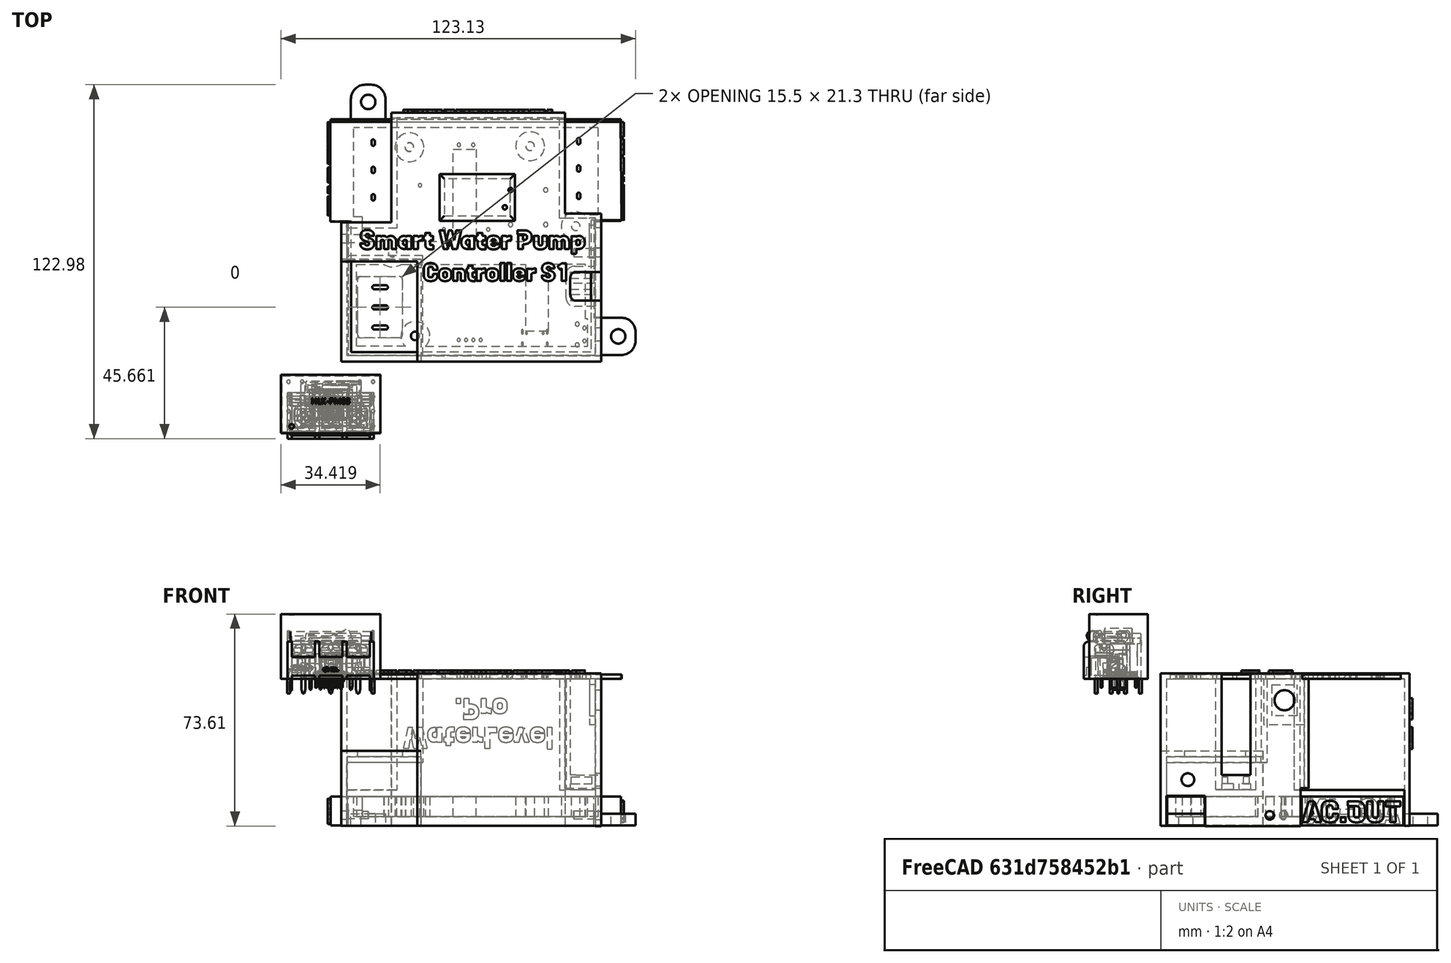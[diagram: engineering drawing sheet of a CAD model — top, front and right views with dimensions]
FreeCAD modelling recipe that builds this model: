
FCSTD DOCUMENT  (FreeCAD 0.21R33771 (Git))
Label: PumpControllerS1_case
License: GPLv3
LicenseURL: https://en.wikipedia.org/wiki/All_rights_reserved
objects: Part::Feature×416, App::Part×69, PartDesign::Pad×68, Sketcher::SketchObject×49, PartDesign::Pocket×38, Part::Part2DObjectPython×8, PartDesign::Fillet×5, PartDesign::Body×3, PartDesign::Boolean×1, PartDesign::Chamfer×1
note: 701 computed .brp shape members not serialized (recipe doc carries the construction recipe); baked Part::Feature solids carry a one-line shape summary decoded from their .brp

FEATURE [Sketcher::SketchObject] Sketch
  FullyConstrained = true
  MapMode = 5
  Support = -> [XY_Plane049]
  sketch-geometry (8):
    g0: LineSegment StartX=0 StartY=63.64 StartZ=0 EndX=0 EndY=97.92 EndZ=0
    g1: LineSegment StartX=0 StartY=97.92 StartZ=0 EndX=100.82 EndY=97.92 EndZ=0
    g2: LineSegment StartX=100.82 StartY=97.92 StartZ=0 EndX=100.82 EndY=63.64 EndZ=0
    g3: LineSegment StartX=100.82 StartY=63.64 StartZ=0 EndX=90.46 EndY=63.64 EndZ=0
    g4: LineSegment StartX=90.46 StartY=63.64 StartZ=0 EndX=90.46 EndY=17.97 EndZ=0
    g5: LineSegment StartX=90.46 StartY=17.97 StartZ=0 EndX=6.99 EndY=17.97 EndZ=0
    g6: LineSegment StartX=6.99 StartY=17.97 StartZ=0 EndX=6.99 EndY=63.64 EndZ=0
    g7: LineSegment StartX=6.99 StartY=63.64 StartZ=0 EndX=0 EndY=63.64 EndZ=0
  constraints (24):
    c: PointOnObject(g0,g-2)
    c: Coincident(g0,g1)
    c: Horizontal(g1)
    c: Coincident(g1,g2)
    c: Vertical(g2)
    c: Coincident(g2,g3)
    c: Horizontal(g3)
    c: Coincident(g3,g4)
    c: Vertical(g4)
    c: Coincident(g4,g5)
    c: Horizontal(g5)
    c: Coincident(g5,g6)
    c: Vertical(g6)
    c: Coincident(g6,g7)
    c: Coincident(g7,g0)
    c: Horizontal(g7)
    c: DistanceX(g0,g1) = 100.82
    c: DistanceX(g5,g4) = 83.47
    c: DistanceX(g3,g2) = 10.36
    c: DistanceY(g2,g1) = 34.28
    c: DistanceY(g4,g3) = 45.67
    c: DistanceY(g-1,g5) = 17.97
    c: Vertical(g0)
    c: Equal(g0,g2)
FEATURE [PartDesign::Pad] Pad
  Direction = (0,0,1)
  Length = 3
  Length2 = 10
  Profile = -> Sketch
  ReferenceAxis = -> Sketch [N_Axis]
  Refine = true
  Type = 0
FEATURE [Sketcher::SketchObject] Sketch001
  FullyConstrained = true
  MapMode = 5
  Placement = pos=(0,0,3) rot=(0,0,1;0rad)
  Support = -> [Pad]
  sketch-geometry (10):
    g0: Circle CenterX=29.39 CenterY=23.62 CenterZ=0 NormalX=0 NormalY=0 NormalZ=1 AngleXU=0 Radius=5
    g1: Circle CenterX=21.48 CenterY=52.55 CenterZ=0 NormalX=0 NormalY=0 NormalZ=1 AngleXU=0 Radius=5
    g2: Circle CenterX=85.08 CenterY=61.73 CenterZ=0 NormalX=0 NormalY=0 NormalZ=1 AngleXU=0 Radius=5
    g3: Circle CenterX=69.27 CenterY=89.53 CenterZ=0 NormalX=0 NormalY=0 NormalZ=1 AngleXU=0 Radius=5
    g4: Circle CenterX=27.31 CenterY=89.16 CenterZ=0 NormalX=0 NormalY=0 NormalZ=1 AngleXU=0 Radius=5
    g5: Circle CenterX=29.39 CenterY=23.62 CenterZ=0 NormalX=0 NormalY=0 NormalZ=1 AngleXU=0 Radius=1.5
    g6: Circle CenterX=21.48 CenterY=52.55 CenterZ=0 NormalX=0 NormalY=0 NormalZ=1 AngleXU=0 Radius=1.5
    g7: Circle CenterX=27.31 CenterY=89.16 CenterZ=0 NormalX=0 NormalY=0 NormalZ=1 AngleXU=0 Radius=1.5
    g8: Circle CenterX=69.27 CenterY=89.53 CenterZ=0 NormalX=0 NormalY=0 NormalZ=1 AngleXU=0 Radius=1.5
    g9: Circle CenterX=85.08 CenterY=61.73 CenterZ=0 NormalX=0 NormalY=0 NormalZ=1 AngleXU=0 Radius=1.5
  constraints (25):
    c: Diameter(g4) = 10
    c: Diameter(g1) = 10
    c: Diameter(g0) = 10
    c: Diameter(g2) = 10
    c: Diameter(g3) = 10
    c: DistanceX(g4,g3) = 41.96
    c: DistanceX(g1,g4) = 5.83
    c: DistanceX(g3,g2) = 15.81
    c: DistanceX(g1,g0) = 7.91
    c: DistanceX(g-1,g0) = 29.39
    c: DistanceY(g4,g3) = 0.37
    c: DistanceY(g2,g3) = 27.8
    c: DistanceY(g1,g4) = 36.61
    c: DistanceY(g0,g1) = 28.93
    c: DistanceY(g-1,g0) = 23.62
    c: Coincident(g5,g0)
    c: Diameter(g5) = 3
    c: Coincident(g6,g1)
    c: Coincident(g7,g4)
    c: Coincident(g8,g3)
    c: Coincident(g9,g2)
    c: Diameter(g7) = 3
    c: Diameter(g8) = 3
    c: Diameter(g9) = 3
    c: Diameter(g6) = 3
FEATURE [PartDesign::Pad] Pad001
  BaseFeature = -> Pad
  Direction = (0,0,1)
  Length = 7
  Length2 = 10
  Profile = -> Sketch001
  ReferenceAxis = -> Sketch001 [N_Axis]
  Refine = true
  Type = 0
FEATURE [Sketcher::SketchObject] Sketch002
  ExternalGeometry = -> [Pad001]
  FullyConstrained = false
  MapMode = 5
  Placement = pos=(0,0,3) rot=(0,0,1;0rad)
  Support = -> [Pad001]
  sketch-geometry (21):
    g0: LineSegment StartX=90.46 StartY=56.5 StartZ=0 EndX=90.46 EndY=48.4293 EndZ=0
    g1: LineSegment StartX=7 StartY=48.5 StartZ=0 EndX=7 EndY=56.5 EndZ=0
    g2: Circle CenterX=21.48 CenterY=52.55 CenterZ=0 NormalX=0 NormalY=0 NormalZ=1 AngleXU=0 Radius=1.5
    g3: LineSegment StartX=42.46 StartY=56.5 StartZ=0 EndX=42.46 EndY=88.5 EndZ=0
    g4: LineSegment StartX=42.46 StartY=88.5 StartZ=0 EndX=50.46 EndY=88.5 EndZ=0
    g5: LineSegment StartX=50.46 StartY=88.5 StartZ=0 EndX=50.46 EndY=56.5 EndZ=0
    g6: LineSegment StartX=67.69 StartY=48.5 StartZ=0 EndX=67.69 EndY=25.4293 EndZ=0
    g7: LineSegment StartX=67.69 StartY=25.4293 StartZ=0 EndX=75.69 EndY=25.4293 EndZ=0
    g8: LineSegment StartX=75.69 StartY=25.4293 StartZ=0 EndX=75.69 EndY=48.4293 EndZ=0
    g9: LineSegment StartX=8 StartY=97.92 StartZ=0 EndX=0 EndY=97.92 EndZ=0
    g10: LineSegment StartX=0 StartY=97.92 StartZ=0 EndX=0 EndY=63.64 EndZ=0
    g11: LineSegment StartX=0 StartY=63.64 StartZ=0 EndX=8 EndY=63.64 EndZ=0
    g12: LineSegment StartX=8 StartY=63.64 StartZ=0 EndX=8 EndY=97.92 EndZ=0
    g13: LineSegment StartX=100.82 StartY=97.92 StartZ=0 EndX=92.82 EndY=97.92 EndZ=0
    g14: LineSegment StartX=92.82 StartY=97.92 StartZ=0 EndX=92.82 EndY=63.64 EndZ=0
    g15: LineSegment StartX=92.82 StartY=63.64 StartZ=0 EndX=100.82 EndY=63.64 EndZ=0
    g16: LineSegment StartX=100.82 StartY=63.64 StartZ=0 EndX=100.82 EndY=97.92 EndZ=0
    g17: LineSegment StartX=7 StartY=56.5 StartZ=0 EndX=42.46 EndY=56.5 EndZ=0
    g18: LineSegment StartX=7 StartY=48.5 StartZ=0 EndX=67.69 EndY=48.5 EndZ=0
    g19: LineSegment StartX=50.46 StartY=56.5 StartZ=0 EndX=90.46 EndY=56.5 EndZ=0
    g20: LineSegment StartX=90.46 StartY=48.4293 StartZ=0 EndX=75.69 EndY=48.4293 EndZ=0
  constraints (58):
    c: Vertical(g0)
    c: Vertical(g1)
    c: DistanceY(g1,g1) = 8
    c: DistanceY(g-1,g1) = 48.5
    c: Coincident(g2,g-3)
    c: Diameter(g2) = 3
    c: Coincident(g3,g4)
    c: Coincident(g4,g5)
    c: Horizontal(g4)
    c: Vertical(g3)
    c: Vertical(g5)
    c: Coincident(g6,g7)
    c: Coincident(g7,g8)
    c: Horizontal(g7)
    c: Vertical(g6)
    c: Vertical(g8)
    c: DistanceX(g4,g4) = 8
    c: DistanceX(g7,g7) = 8
    c: Coincident(g9,g10)
    c: Coincident(g10,g11)
    c: Coincident(g11,g12)
    c: Coincident(g12,g9)
    c: Horizontal(g9)
    c: Horizontal(g11)
    c: Vertical(g10)
    c: Vertical(g12)
    c: PointOnObject(g9,g-4)
    c: Coincident(g10,g-8)
    c: Coincident(g13,g14)
    c: Coincident(g14,g15)
    c: Coincident(g15,g16)
    c: Coincident(g16,g13)
    c: Horizontal(g13)
    c: Horizontal(g15)
    c: Vertical(g14)
    c: Vertical(g16)
    c: Coincident(g13,g-7)
    c: PointOnObject(g14,g-6)
    c: DistanceX(g13,g13) = 8
    c: DistanceX(g9,g9) = 8
    c: DistanceY(g8,g8) = 23
    c: DistanceY(g5,g5) = 32
    c: DistanceX(g5,g0) = 40
    c: DistanceX(g-1,g1) = 7
    c: DistanceX(g1,g0) = 83.46
    c: DistanceX(g8,g0) = 14.77
    c: Coincident(g1,g17)
    c: Coincident(g17,g3)
    c: Horizontal(g17)
    c: Coincident(g1,g18)
    c: Coincident(g18,g6)
    c: Horizontal(g18)
    c: Coincident(g5,g19)
    c: Coincident(g19,g0)
    c: Horizontal(g19)
    c: Coincident(g0,g20)
    c: Coincident(g20,g8)
    c: Horizontal(g20)
FEATURE [PartDesign::Pad] Pad002
  BaseFeature = -> Pad001
  Direction = (0,0,1)
  Length = 7
  Length2 = 10
  Profile = -> Sketch002
  ReferenceAxis = -> Sketch002 [N_Axis]
  Refine = true
  Type = 0
FEATURE [Sketcher::SketchObject] Sketch003
  ExternalGeometry = -> [Pad002]
  FullyConstrained = true
  MapMode = 5
  Placement = pos=(0,0,3) rot=(0,0,1;0rad)
  Support = -> [Pad002]
  sketch-geometry (20):
    g0: LineSegment StartX=5 StartY=97.92 StartZ=0 EndX=94 EndY=97.92 EndZ=0
    g1: LineSegment StartX=94 StartY=97.92 StartZ=0 EndX=94 EndY=95.92 EndZ=0
    g2: LineSegment StartX=94 StartY=95.92 StartZ=0 EndX=5 EndY=95.92 EndZ=0
    g3: LineSegment StartX=5 StartY=95.92 StartZ=0 EndX=5 EndY=97.92 EndZ=0
    g4: LineSegment StartX=6.99 StartY=17.97 StartZ=0 EndX=8.99 EndY=17.97 EndZ=0
    g5: LineSegment StartX=8.99 StartY=17.97 StartZ=0 EndX=8.99 EndY=64.97 EndZ=0
    g6: LineSegment StartX=8.99 StartY=64.97 StartZ=0 EndX=6.99 EndY=64.97 EndZ=0
    g7: LineSegment StartX=6.99 StartY=64.97 StartZ=0 EndX=6.99 EndY=17.97 EndZ=0
    g8: LineSegment StartX=90.46 StartY=29.6 StartZ=0 EndX=88.46 EndY=29.6 EndZ=0
    g9: LineSegment StartX=88.46 StartY=29.6 StartZ=0 EndX=88.46 EndY=64.6 EndZ=0
    g10: LineSegment StartX=88.46 StartY=64.6 StartZ=0 EndX=90.46 EndY=64.6 EndZ=0
    g11: LineSegment StartX=90.46 StartY=64.6 StartZ=0 EndX=90.46 EndY=29.6 EndZ=0
    g12: LineSegment StartX=90.46 StartY=17.97 StartZ=0 EndX=89.21 EndY=17.97 EndZ=0
    g13: LineSegment StartX=89.21 StartY=17.97 StartZ=0 EndX=89.21 EndY=26.97 EndZ=0
    g14: LineSegment StartX=89.21 StartY=26.97 StartZ=0 EndX=90.46 EndY=26.97 EndZ=0
    g15: LineSegment StartX=90.46 StartY=26.97 StartZ=0 EndX=90.46 EndY=17.97 EndZ=0
    g16: LineSegment StartX=35.93 StartY=17.97 StartZ=0 EndX=75.93 EndY=17.97 EndZ=0
    g17: LineSegment StartX=75.93 StartY=17.97 StartZ=0 EndX=75.93 EndY=19.97 EndZ=0
    g18: LineSegment StartX=75.93 StartY=19.97 StartZ=0 EndX=35.93 EndY=19.97 EndZ=0
    g19: LineSegment StartX=35.93 StartY=19.97 StartZ=0 EndX=35.93 EndY=17.97 EndZ=0
  constraints (58):
    c: Coincident(g0,g1)
    c: Coincident(g1,g2)
    c: Coincident(g2,g3)
    c: Coincident(g3,g0)
    c: Horizontal(g0)
    c: Horizontal(g2)
    c: Vertical(g1)
    c: Vertical(g3)
    c: PointOnObject(g0,g-3)
    c: DistanceY(g1,g1) = 2
    c: DistanceX(g-1,g0) = 5
    c: DistanceX(g0,g0) = 89
    c: Coincident(g4,g5)
    c: Coincident(g5,g6)
    c: Coincident(g6,g7)
    c: Coincident(g7,g4)
    c: Horizontal(g4)
    c: Horizontal(g6)
    c: Vertical(g5)
    c: Vertical(g7)
    c: Coincident(g4,g-7)
    c: DistanceY(g5,g5) = 47
    c: DistanceX(g6,g5) = 2
    c: Coincident(g8,g9)
    c: Coincident(g9,g10)
    c: Coincident(g10,g11)
    c: Coincident(g11,g8)
    c: Horizontal(g8)
    c: Horizontal(g10)
    c: Vertical(g9)
    c: Vertical(g11)
    c: PointOnObject(g8,g-8)
    c: DistanceX(g9,g10) = 2
    c: DistanceY(g9,g9) = 35
    c: DistanceY(g-8,g8) = 11.63
    c: Coincident(g12,g13)
    c: Coincident(g13,g14)
    c: Coincident(g14,g15)
    c: Coincident(g15,g12)
    c: Horizontal(g12)
    c: Horizontal(g14)
    c: Vertical(g13)
    c: Vertical(g15)
    c: Coincident(g12,g-8)
    c: DistanceX(g14,g14) = 1.25
    c: DistanceY(g13,g13) = 9
    c: Coincident(g16,g17)
    c: Coincident(g17,g18)
    c: Coincident(g18,g19)
    c: Coincident(g19,g16)
    c: Horizontal(g16)
    c: Horizontal(g18)
    c: Vertical(g17)
    c: Vertical(g19)
    c: PointOnObject(g16,g-7)
    c: DistanceY(g17,g17) = 2
    c: DistanceX(g18,g18) = 40
    c: DistanceX(g-1,g16) = 35.93
FEATURE [PartDesign::Pad] Pad003
  BaseFeature = -> Pad002
  Direction = (0,0,1)
  Length = 7
  Length2 = 10
  Profile = -> Sketch003
  ReferenceAxis = -> Sketch003 [N_Axis]
  Refine = true
  Type = 0
FEATURE [PartDesign::Pad] Pad004
  BaseFeature = -> Pad003
  Direction = (0,1,0)
  Length = 4
  Length2 = 10
  Profile = -> Pad003 [Face33]
  Refine = true
  Type = 0
FEATURE [PartDesign::Pad] Pad005
  BaseFeature = -> Pad004
  Direction = (1,0,0)
  Length = 14
  Length2 = 10
  Profile = -> Pad004 [Face13]
  Refine = true
  Type = 0
FEATURE [PartDesign::Pad] Pad006
  BaseFeature = -> Pad005
  Direction = (-1,0,0)
  Length = 28
  Length2 = 10
  Profile = -> Pad005 [Face36]
  Refine = true
  Type = 0
FEATURE [Sketcher::SketchObject] Sketch004
  ExternalGeometry = -> [Pad006]
  FullyConstrained = true
  MapMode = 5
  Placement = pos=(92.82,0,0) rot=(0.57735,-0.57735,-0.57735;2.0944rad)
  Support = -> [Pad006]
  sketch-geometry (4):
    g0: LineSegment StartX=-63.64 StartY=3 StartZ=0 EndX=-65.64 EndY=3 EndZ=0
    g1: LineSegment StartX=-65.64 StartY=3 StartZ=0 EndX=-65.64 EndY=10 EndZ=0
    g2: LineSegment StartX=-65.64 StartY=10 StartZ=0 EndX=-63.64 EndY=10 EndZ=0
    g3: LineSegment StartX=-63.64 StartY=10 StartZ=0 EndX=-63.64 EndY=3 EndZ=0
  constraints (11):
    c: Coincident(g0,g1)
    c: Coincident(g1,g2)
    c: Coincident(g2,g3)
    c: Coincident(g3,g0)
    c: Horizontal(g0)
    c: Horizontal(g2)
    c: Vertical(g1)
    c: Vertical(g3)
    c: Coincident(g0,g-5)
    c: PointOnObject(g1,g-4)
    c: DistanceX(g1,g2) = 2
FEATURE [PartDesign::Pad] Pad007
  BaseFeature = -> Pad006
  Direction = (-1,0,0)
  Length = 10
  Length2 = 10
  Profile = -> Sketch004
  ReferenceAxis = -> Sketch004 [N_Axis]
  Refine = true
  Type = 0
FEATURE [Sketcher::SketchObject] Sketch005
  ExternalGeometry = -> [Pad007]
  FullyConstrained = true
  MapMode = 5
  Placement = pos=(90.46,0,0) rot=(0.57735,0.57735,0.57735;2.0944rad)
  Support = -> [Pad007]
  sketch-geometry (4):
    g0: LineSegment StartX=17.97 StartY=10 StartZ=0 EndX=29.97 EndY=10 EndZ=0
    g1: LineSegment StartX=29.97 StartY=10 StartZ=0 EndX=29.97 EndY=0 EndZ=0
    g2: LineSegment StartX=29.97 StartY=0 StartZ=0 EndX=17.97 EndY=0 EndZ=0
    g3: LineSegment StartX=17.97 StartY=0 StartZ=0 EndX=17.97 EndY=10 EndZ=0
  constraints (11):
    c: Coincident(g0,g1)
    c: Coincident(g1,g2)
    c: Coincident(g2,g3)
    c: Coincident(g3,g0)
    c: Horizontal(g0)
    c: Horizontal(g2)
    c: Vertical(g1)
    c: Vertical(g3)
    c: Coincident(g0,g-4)
    c: PointOnObject(g1,g-5)
    c: DistanceX(g0,g0) = 12
FEATURE [PartDesign::Pad] Pad008
  BaseFeature = -> Pad007
  Direction = (1,0,0)
  Length = 1.5
  Length2 = 10
  Profile = -> Sketch005
  ReferenceAxis = -> Sketch005 [N_Axis]
  Refine = true
  Type = 0
FEATURE [Sketcher::SketchObject] Sketch006
  ExternalGeometry = -> [Pad008]
  FullyConstrained = true
  MapMode = 5
  Placement = pos=(0,0,10) rot=(0,0,1;0rad)
  Support = -> [Pad008]
  sketch-geometry (4):
    g0: LineSegment StartX=90.46 StartY=29.97 StartZ=0 EndX=91.96 EndY=29.97 EndZ=0
    g1: LineSegment StartX=91.96 StartY=29.97 StartZ=0 EndX=91.96 EndY=17.97 EndZ=0
    g2: LineSegment StartX=91.96 StartY=17.97 StartZ=0 EndX=90.46 EndY=17.97 EndZ=0
    g3: LineSegment StartX=90.46 StartY=17.97 StartZ=0 EndX=90.46 EndY=29.97 EndZ=0
  constraints (10):
    c: Coincident(g0,g1)
    c: Coincident(g1,g2)
    c: Coincident(g2,g3)
    c: Coincident(g3,g0)
    c: Horizontal(g0)
    c: Horizontal(g2)
    c: Vertical(g1)
    c: Vertical(g3)
    c: Coincident(g0,g-3)
    c: Coincident(g1,g-5)
FEATURE [PartDesign::Pad] Pad009
  BaseFeature = -> Pad008
  Direction = (0,0,1)
  Length = 12
  Length2 = 10
  Profile = -> Sketch006
  ReferenceAxis = -> Sketch006 [N_Axis]
  Refine = true
  Type = 0
FEATURE [Sketcher::SketchObject] Sketch007
  FullyConstrained = false
  MapMode = 5
  Placement = pos=(91.96,0,0) rot=(0.57735,0.57735,0.57735;2.0944rad)
  Support = -> [Pad009]
  sketch-geometry (1):
    g0: Circle CenterX=24.1415 CenterY=15.9066 CenterZ=0 NormalX=0 NormalY=0 NormalZ=1 AngleXU=0 Radius=2.2
  constraints (1):
    c: Diameter(g0) = 4.4
FEATURE [PartDesign::Pocket] Pocket
  BaseFeature = -> Pad009
  Direction = (-1,0,0)
  Length = 5
  Length2 = 5
  Profile = -> Sketch007
  ReferenceAxis = -> Sketch007 [N_Axis]
  Refine = true
  Type = 0
FEATURE [PartDesign::Pad] Pad010
  BaseFeature = -> Pocket
  Direction = (0,1,0)
  Length = 1
  Length2 = 10
  Profile = -> Pocket [Face4]
  Refine = true
  Type = 0
FEATURE [PartDesign::Pad] Pad011
  BaseFeature = -> Pad010
  Direction = (0,-1,0)
  Length = 1
  Length2 = 10
  Profile = -> Pad010 [Face5]
  Refine = true
  Type = 0
FEATURE [PartDesign::Pad] Pad012
  BaseFeature = -> Pad011
  Direction = (-1,0,0)
  Length = 1
  Length2 = 10
  Profile = -> Pad011 [Face59]
  Refine = true
  Type = 0
FEATURE [PartDesign::Pad] Pad013
  BaseFeature = -> Pad012
  Direction = (1,0,0)
  Length = 1
  Length2 = 10
  Profile = -> Pad012 [Face5]
  Refine = true
  Type = 0
FEATURE [Sketcher::SketchObject] Sketch008
  FullyConstrained = true
  MapMode = 5
  Support = -> [XY_Plane050]
  sketch-geometry (10):
    g0: LineSegment StartX=21 StartY=100.55 StartZ=0 EndX=21 EndY=64.55 EndZ=0
    g1: LineSegment StartX=21 StartY=64.55 StartZ=0 EndX=4.2 EndY=64.55 EndZ=0
    g2: LineSegment StartX=93.5 StartY=15.2 StartZ=0 EndX=93.5 EndY=65.2 EndZ=0
    g3: LineSegment StartX=93.5 StartY=65.2 StartZ=0 EndX=80.9 EndY=65.2 EndZ=0
    g4: LineSegment StartX=80.9 StartY=65.2 StartZ=0 EndX=80.9 EndY=100.55 EndZ=0
    g5: LineSegment StartX=80.9 StartY=100.55 StartZ=0 EndX=21 EndY=100.55 EndZ=0
    g6: LineSegment StartX=93.5 StartY=15.2 StartZ=0 EndX=30 EndY=15.2 EndZ=0
    g7: LineSegment StartX=30 StartY=15.2 StartZ=0 EndX=30 EndY=49.55 EndZ=0
    g8: LineSegment StartX=30 StartY=49.55 StartZ=0 EndX=4.2 EndY=49.55 EndZ=0
    g9: LineSegment StartX=4.2 StartY=49.55 StartZ=0 EndX=4.2 EndY=64.55 EndZ=0
  constraints (30):
    c: Vertical(g0)
    c: Coincident(g0,g1)
    c: Horizontal(g1)
    c: Vertical(g2)
    c: Coincident(g2,g3)
    c: Coincident(g3,g4)
    c: Vertical(g4)
    c: Coincident(g4,g5)
    c: Coincident(g5,g0)
    c: Horizontal(g5)
    c: Horizontal(g3)
    c: Coincident(g2,g6)
    c: Horizontal(g6)
    c: Coincident(g6,g7)
    c: Vertical(g7)
    c: Coincident(g7,g8)
    c: Horizontal(g8)
    c: Coincident(g8,g9)
    c: Coincident(g9,g1)
    c: Vertical(g9)
    c: DistanceY(g-1,g6) = 15.2
    c: DistanceX(g-1,g6) = 30
    c: DistanceX(g8,g7) = 25.8
    c: DistanceX(g6,g6) = 63.5
    c: DistanceY(g2,g2) = 50
    c: DistanceY(g7,g7) = 34.35
    c: DistanceY(g9,g9) = 15
    c: DistanceY(g0,g0) = 36
    c: DistanceX(g5,g5) = 59.9
    c: DistanceX(g3,g3) = 12.6
FEATURE [PartDesign::Pad] Pad014
  Direction = (0,0,1)
  Length = 2
  Length2 = 10
  Profile = -> Sketch008
  ReferenceAxis = -> Sketch008 [N_Axis]
  Refine = true
  Type = 0
FEATURE [Sketcher::SketchObject] Sketch009
  FullyConstrained = false
  MapMode = 5
  Support = -> [XY_Plane051]
  sketch-geometry (4):
    g0: LineSegment StartX=4.34912 StartY=50.7797 StartZ=0 EndX=32.5138 EndY=50.7797 EndZ=0
    g1: LineSegment StartX=32.5138 StartY=50.7797 StartZ=0 EndX=32.5138 EndY=14.7356 EndZ=0
    g2: LineSegment StartX=32.5138 StartY=14.7356 StartZ=0 EndX=4.34912 EndY=14.7356 EndZ=0
    g3: LineSegment StartX=4.34912 StartY=14.7356 StartZ=0 EndX=4.34912 EndY=50.7797 EndZ=0
  constraints (8):
    c: Coincident(g0,g1)
    c: Coincident(g1,g2)
    c: Coincident(g2,g3)
    c: Coincident(g3,g0)
    c: Horizontal(g0)
    c: Horizontal(g2)
    c: Vertical(g1)
    c: Vertical(g3)
FEATURE [PartDesign::Pad] Pad015
  Direction = (0,0,1)
  Length = 2
  Length2 = 10
  Profile = -> Sketch009
  ReferenceAxis = -> Sketch009 [N_Axis]
  Refine = true
  Type = 0
FEATURE [Sketcher::SketchObject] Sketch010
  ExternalGeometry = -> [Pad015]
  FullyConstrained = true
  MapMode = 5
  Placement = pos=(0,0,0) rot=(1,0,0;3.14159rad)
  Support = -> [Pad015]
  sketch-geometry (6):
    g0: LineSegment StartX=4.34912 StartY=-50.7797 StartZ=0 EndX=4.34912 EndY=-14.7356 EndZ=0
    g1: LineSegment StartX=4.34912 StartY=-14.7356 StartZ=0 EndX=32.5138 EndY=-14.7356 EndZ=0
    g2: LineSegment StartX=32.5138 StartY=-14.7356 StartZ=0 EndX=32.5138 EndY=-16.2356 EndZ=0
    g3: LineSegment StartX=32.5138 StartY=-16.2356 StartZ=0 EndX=5.84912 EndY=-16.2356 EndZ=0
    g4: LineSegment StartX=5.84912 StartY=-16.2356 StartZ=0 EndX=5.84912 EndY=-50.7797 EndZ=0
    g5: LineSegment StartX=5.84912 StartY=-50.7797 StartZ=0 EndX=4.34912 EndY=-50.7797 EndZ=0
  constraints (15):
    c: Coincident(g-3,g0)
    c: Coincident(g0,g-4)
    c: Coincident(g0,g1)
    c: Coincident(g1,g-4)
    c: Coincident(g1,g2)
    c: Vertical(g2)
    c: Coincident(g2,g3)
    c: Horizontal(g3)
    c: Coincident(g3,g4)
    c: Vertical(g4)
    c: Coincident(g4,g5)
    c: Coincident(g5,g0)
    c: DistanceY(g2,g1) = 1.5
    c: DistanceX(g0,g4) = 1.5
    c: PointOnObject(g4,g-5)
FEATURE [PartDesign::Pad] Pad016
  BaseFeature = -> Pad015
  Direction = (0,0,-1)
  Length = 22
  Length2 = 10
  Profile = -> Sketch010
  ReferenceAxis = -> Sketch010 [N_Axis]
  Refine = true
  Type = 0
FEATURE [Sketcher::SketchObject] Sketch011
  ExternalGeometry = -> [Pad016]
  FullyConstrained = true
  MapMode = 5
  Placement = pos=(0,0,2) rot=(0,0,1;0rad)
  Support = -> [Pad016]
  sketch-geometry (4):
    g0: LineSegment StartX=9.59912 StartY=43.7856 StartZ=0 EndX=25.0991 EndY=43.7856 EndZ=0
    g1: LineSegment StartX=25.0991 StartY=43.7856 StartZ=0 EndX=25.0991 EndY=22.4856 EndZ=0
    g2: LineSegment StartX=25.0991 StartY=22.4856 StartZ=0 EndX=9.59912 EndY=22.4856 EndZ=0
    g3: LineSegment StartX=9.59912 StartY=22.4856 StartZ=0 EndX=9.59912 EndY=43.7856 EndZ=0
  constraints (12):
    c: Coincident(g0,g1)
    c: Coincident(g1,g2)
    c: Coincident(g2,g3)
    c: Coincident(g3,g0)
    c: Horizontal(g0)
    c: Horizontal(g2)
    c: Vertical(g1)
    c: Vertical(g3)
    c: DistanceX(g0,g0) = 15.5
    c: DistanceY(g1,g0) = 21.3
    c: DistanceY(g-4,g2) = 7.75
    c: DistanceX(g-4,g2) = 5.25
FEATURE [PartDesign::Pocket] Pocket001
  BaseFeature = -> Pad016
  Direction = (0,0,-1)
  Length = 5
  Length2 = 5
  Profile = -> Sketch011
  ReferenceAxis = -> Sketch011 [N_Axis]
  Refine = true
  Type = 0
FEATURE [Sketcher::SketchObject] Sketch012
  ExternalGeometry = -> [Pad014]
  FullyConstrained = true
  MapMode = 5
  Placement = pos=(0,0,0) rot=(1,0,0;3.14159rad)
  Support = -> [Pad014]
  sketch-geometry (8):
    g0: LineSegment StartX=30 StartY=-15.2 StartZ=0 EndX=93.5 EndY=-15.2 EndZ=0
    g1: LineSegment StartX=93.5 StartY=-15.2 StartZ=0 EndX=93.5 EndY=-16.7 EndZ=0
    g2: LineSegment StartX=93.5 StartY=-16.7 StartZ=0 EndX=30 EndY=-16.7 EndZ=0
    g3: LineSegment StartX=30 StartY=-16.7 StartZ=0 EndX=30 EndY=-15.2 EndZ=0
    g4: LineSegment StartX=21 StartY=-100.55 StartZ=0 EndX=80.9 EndY=-100.55 EndZ=0
    g5: LineSegment StartX=80.9 StartY=-100.55 StartZ=0 EndX=80.9 EndY=-99.35 EndZ=0
    g6: LineSegment StartX=80.9 StartY=-99.35 StartZ=0 EndX=21 EndY=-99.35 EndZ=0
    g7: LineSegment StartX=21 StartY=-99.35 StartZ=0 EndX=21 EndY=-100.55 EndZ=0
  constraints (22):
    c: Coincident(g0,g1)
    c: Coincident(g1,g2)
    c: Coincident(g2,g3)
    c: Coincident(g3,g0)
    c: Horizontal(g0)
    c: Horizontal(g2)
    c: Vertical(g1)
    c: Vertical(g3)
    c: Coincident(g0,g-4)
    c: PointOnObject(g1,g-5)
    c: DistanceY(g1,g1) = 1.5
    c: Coincident(g4,g5)
    c: Coincident(g5,g6)
    c: Coincident(g6,g7)
    c: Coincident(g7,g4)
    c: Horizontal(g4)
    c: Horizontal(g6)
    c: Vertical(g5)
    c: Vertical(g7)
    c: Coincident(g4,g-10)
    c: DistanceY(g5,g5) = 1.2
    c: PointOnObject(g5,g-11)
FEATURE [PartDesign::Pad] Pad017
  BaseFeature = -> Pad014
  Direction = (0,0,-1)
  Length = 51
  Length2 = 10
  Profile = -> Sketch012
  ReferenceAxis = -> Sketch012 [N_Axis]
  Refine = true
  Type = 0
FEATURE [PartDesign::Pad] Pad018
  BaseFeature = -> Pad017
  Direction = (0,1,0)
  Length = 0.6
  Length2 = 10
  Profile = -> Pad017 [Face16]
  Refine = true
  Type = 0
FEATURE [PartDesign::Pad] Pad019
  BaseFeature = -> Pad018
  Direction = (0,-1,0)
  Length = 0.5
  Length2 = 10
  Profile = -> Pad018 [Face4]
  Refine = true
  Type = 0
FEATURE [PartDesign::Pad] Pad020
  BaseFeature = -> Pocket001
  Direction = (0,-1,0)
  Length = 0.5
  Length2 = 10
  Profile = -> Pocket001 [Face5]
  Refine = true
  Type = 0
FEATURE [PartDesign::Pad] Pad021
  BaseFeature = -> Pad020
  Direction = (-1,0,0)
  Length = 0.5
  Length2 = 10
  Profile = -> Pad020 [Face11]
  Refine = true
  Type = 0
FEATURE [Sketcher::SketchObject] Sketch013
  ExternalGeometry = -> [Pad019]
  FullyConstrained = true
  MapMode = 5
  Placement = pos=(0,0,0) rot=(1,0,0;3.14159rad)
  Support = -> [Pad019]
  sketch-geometry (6):
    g0: LineSegment StartX=30 StartY=-16.7 StartZ=0 EndX=32 EndY=-16.7 EndZ=0
    g1: LineSegment StartX=32 StartY=-16.7 StartZ=0 EndX=32 EndY=-51.55 EndZ=0
    g2: LineSegment StartX=32 StartY=-51.55 StartZ=0 EndX=4.2 EndY=-51.55 EndZ=0
    g3: LineSegment StartX=4.2 StartY=-51.55 StartZ=0 EndX=4.2 EndY=-49.55 EndZ=0
    g4: LineSegment StartX=4.2 StartY=-49.55 StartZ=0 EndX=30 EndY=-49.55 EndZ=0
    g5: LineSegment StartX=30 StartY=-49.55 StartZ=0 EndX=30 EndY=-16.7 EndZ=0
  constraints (15):
    c: Coincident(g-4,g0)
    c: PointOnObject(g0,g-4)
    c: Coincident(g0,g1)
    c: Vertical(g1)
    c: Coincident(g1,g2)
    c: Horizontal(g2)
    c: Coincident(g2,g3)
    c: Coincident(g3,g-5)
    c: Coincident(g3,g4)
    c: Coincident(g4,g-5)
    c: Coincident(g4,g5)
    c: Coincident(g5,g0)
    c: Vertical(g3)
    c: DistanceY(g3,g3) = 2
    c: DistanceX(g0,g0) = 2
FEATURE [PartDesign::Pad] Pad022
  BaseFeature = -> Pad019
  Direction = (0,0,-1)
  Length = 29
  Length2 = 10
  Profile = -> Sketch013
  ReferenceAxis = -> Sketch013 [N_Axis]
  Refine = true
  Type = 0
FEATURE [Sketcher::SketchObject] Sketch014
  ExternalGeometry = -> [Pad022]
  FullyConstrained = true
  MapMode = 5
  Placement = pos=(0,0,0) rot=(1,0,0;3.14159rad)
  Support = -> [Pad022]
  sketch-geometry (4):
    g0: LineSegment StartX=4.2 StartY=-64.55 StartZ=0 EndX=6.2 EndY=-64.55 EndZ=0
    g1: LineSegment StartX=6.2 StartY=-64.55 StartZ=0 EndX=6.2 EndY=-51.55 EndZ=0
    g2: LineSegment StartX=6.2 StartY=-51.55 StartZ=0 EndX=4.2 EndY=-51.55 EndZ=0
    g3: LineSegment StartX=4.2 StartY=-51.55 StartZ=0 EndX=4.2 EndY=-64.55 EndZ=0
  constraints (11):
    c: Coincident(g0,g1)
    c: Coincident(g1,g2)
    c: Coincident(g2,g3)
    c: Coincident(g3,g0)
    c: Horizontal(g0)
    c: Horizontal(g2)
    c: Vertical(g1)
    c: Vertical(g3)
    c: Coincident(g0,g-4)
    c: PointOnObject(g1,g-5)
    c: DistanceX(g2,g2) = 2
FEATURE [PartDesign::Pad] Pad023
  BaseFeature = -> Pad022
  Direction = (0,0,-1)
  Length = 51
  Length2 = 10
  Profile = -> Sketch014
  ReferenceAxis = -> Sketch014 [N_Axis]
  Refine = true
  Type = 0
FEATURE [PartDesign::Pocket] Pocket002
  BaseFeature = -> Pad023
  Direction = (0,-1,0)
  Length = 1.5
  Length2 = 5
  Profile = -> Pad023 [Face21]
  Refine = true
  Type = 0
FEATURE [PartDesign::Pad] Pad024
  BaseFeature = -> Pocket002
  Direction = (-1,0,0)
  Length = 0.55
  Length2 = 10
  Profile = -> Pocket002 [Face18]
  Refine = true
  Type = 0
FEATURE [PartDesign::Pad] Pad025
  BaseFeature = -> Pad024
  Direction = (0,-1,0)
  Length = 1
  Length2 = 10
  Profile = -> Pad024 [Face19]
  Refine = true
  Type = 0
FEATURE [Sketcher::SketchObject] Sketch015
  ExternalGeometry = -> [Pad025]
  FullyConstrained = true
  MapMode = 5
  Placement = pos=(0,0,0) rot=(1,0,0;3.14159rad)
  Support = -> [Pad025]
  sketch-geometry (6):
    g0: LineSegment StartX=6.2 StartY=-63.05 StartZ=0 EndX=21 EndY=-63.05 EndZ=0
    g1: LineSegment StartX=21 StartY=-63.05 StartZ=0 EndX=21 EndY=-99.35 EndZ=0
    g2: LineSegment StartX=21 StartY=-99.35 StartZ=0 EndX=23 EndY=-99.35 EndZ=0
    g3: LineSegment StartX=23 StartY=-99.35 StartZ=0 EndX=23 EndY=-61.05 EndZ=0
    g4: LineSegment StartX=23 StartY=-61.05 StartZ=0 EndX=6.2 EndY=-61.05 EndZ=0
    g5: LineSegment StartX=6.2 StartY=-61.05 StartZ=0 EndX=6.2 EndY=-63.05 EndZ=0
  constraints (15):
    c: Coincident(g-4,g0)
    c: Coincident(g0,g-4)
    c: Coincident(g0,g1)
    c: Coincident(g1,g-3)
    c: Coincident(g1,g2)
    c: Horizontal(g2)
    c: Coincident(g2,g3)
    c: Vertical(g3)
    c: Coincident(g3,g4)
    c: Horizontal(g4)
    c: Coincident(g4,g5)
    c: Coincident(g5,g0)
    c: Vertical(g5)
    c: DistanceX(g2,g2) = 2
    c: DistanceY(g5,g5) = 2
FEATURE [PartDesign::Pad] Pad026
  BaseFeature = -> Pad025
  Direction = (0,0,-1)
  Length = 38.6
  Length2 = 10
  Profile = -> Sketch015
  ReferenceAxis = -> Sketch015 [N_Axis]
  Refine = true
  Type = 0
FEATURE [Sketcher::SketchObject] Sketch016
  ExternalGeometry = -> [Pad026]
  FullyConstrained = true
  MapMode = 5
  Placement = pos=(0,0,0) rot=(1,0,0;3.14159rad)
  Support = -> [Pad026]
  sketch-geometry (4):
    g0: LineSegment StartX=93.5 StartY=-65.2 StartZ=0 EndX=91.5 EndY=-65.2 EndZ=0
    g1: LineSegment StartX=91.5 StartY=-65.2 StartZ=0 EndX=91.5 EndY=-16.7 EndZ=0
    g2: LineSegment StartX=91.5 StartY=-16.7 StartZ=0 EndX=93.5 EndY=-16.7 EndZ=0
    g3: LineSegment StartX=93.5 StartY=-16.7 StartZ=0 EndX=93.5 EndY=-65.2 EndZ=0
  constraints (11):
    c: Coincident(g0,g1)
    c: Coincident(g1,g2)
    c: Coincident(g2,g3)
    c: Coincident(g3,g0)
    c: Horizontal(g0)
    c: Horizontal(g2)
    c: Vertical(g1)
    c: Vertical(g3)
    c: Coincident(g0,g-5)
    c: PointOnObject(g1,g-4)
    c: DistanceX(g0,g0) = 2
FEATURE [PartDesign::Pad] Pad027
  BaseFeature = -> Pad026
  Direction = (0,0,-1)
  Length = 28.7
  Length2 = 10
  Profile = -> Sketch016
  ReferenceAxis = -> Sketch016 [N_Axis]
  Refine = true
  Type = 0
FEATURE [Sketcher::SketchObject] Sketch017
  ExternalGeometry = -> [Pad027]
  FullyConstrained = true
  MapMode = 5
  Placement = pos=(0,0,-28.7) rot=(1,0,0;3.14159rad)
  Support = -> [Pad027]
  sketch-geometry (4):
    g0: LineSegment StartX=91.5 StartY=-65.2 StartZ=0 EndX=93.5 EndY=-65.2 EndZ=0
    g1: LineSegment StartX=93.5 StartY=-65.2 StartZ=0 EndX=93.5 EndY=-30.4 EndZ=0
    g2: LineSegment StartX=93.5 StartY=-30.4 StartZ=0 EndX=91.5 EndY=-30.4 EndZ=0
    g3: LineSegment StartX=91.5 StartY=-30.4 StartZ=0 EndX=91.5 EndY=-65.2 EndZ=0
  constraints (11):
    c: Coincident(g0,g1)
    c: Coincident(g1,g2)
    c: Coincident(g2,g3)
    c: Coincident(g3,g0)
    c: Horizontal(g0)
    c: Horizontal(g2)
    c: Vertical(g1)
    c: Vertical(g3)
    c: Coincident(g0,g-5)
    c: PointOnObject(g1,g-3)
    c: DistanceY(g1,g1) = 34.8
FEATURE [PartDesign::Pad] Pad028
  BaseFeature = -> Pad027
  Direction = (0,0,-1)
  Length = 22.4
  Length2 = 10
  Profile = -> Sketch017
  ReferenceAxis = -> Sketch017 [N_Axis]
  Refine = true
  Type = 0
FEATURE [PartDesign::Pocket] Pocket003
  BaseFeature = -> Pad028
  Direction = (0,-1,0)
  Length = 1.9
  Length2 = 5
  Profile = -> Pad028 [Face27]
  Refine = true
  Type = 0
FEATURE [Sketcher::SketchObject] Sketch018
  ExternalGeometry = -> [Pocket003]
  FullyConstrained = true
  MapMode = 5
  Placement = pos=(0,0,0) rot=(1,0,0;3.14159rad)
  Support = -> [Pocket003]
  sketch-geometry (4):
    g0: LineSegment StartX=80.9 StartY=-63.3 StartZ=0 EndX=78.9 EndY=-63.3 EndZ=0
    g1: LineSegment StartX=78.9 StartY=-63.3 StartZ=0 EndX=78.9 EndY=-99.35 EndZ=0
    g2: LineSegment StartX=78.9 StartY=-99.35 StartZ=0 EndX=80.9 EndY=-99.35 EndZ=0
    g3: LineSegment StartX=80.9 StartY=-99.35 StartZ=0 EndX=80.9 EndY=-63.3 EndZ=0
  constraints (11):
    c: Coincident(g0,g1)
    c: Coincident(g1,g2)
    c: Coincident(g2,g3)
    c: Coincident(g3,g0)
    c: Horizontal(g0)
    c: Horizontal(g2)
    c: Vertical(g1)
    c: Vertical(g3)
    c: Coincident(g0,g-3)
    c: PointOnObject(g1,g-4)
    c: DistanceX(g0,g0) = 2
FEATURE [PartDesign::Pad] Pad029
  BaseFeature = -> Pocket003
  Direction = (0,0,-1)
  Length = 38.6
  Length2 = 10
  Profile = -> Sketch018
  ReferenceAxis = -> Sketch018 [N_Axis]
  Refine = true
  Type = 0
FEATURE [Sketcher::SketchObject] Sketch019
  ExternalGeometry = -> [Pad029]
  FullyConstrained = true
  MapMode = 5
  Placement = pos=(0,63.3,0) rot=(0,0.707107,0.707107;3.14159rad)
  Support = -> [Pad029]
  sketch-geometry (4):
    g0: LineSegment StartX=-93.5 StartY=2 StartZ=0 EndX=-91.5 EndY=2 EndZ=0
    g1: LineSegment StartX=-91.5 StartY=2 StartZ=0 EndX=-91.5 EndY=-38 EndZ=0
    g2: LineSegment StartX=-91.5 StartY=-38 StartZ=0 EndX=-93.5 EndY=-38 EndZ=0
    g3: LineSegment StartX=-93.5 StartY=-38 StartZ=0 EndX=-93.5 EndY=2 EndZ=0
  constraints (11):
    c: Coincident(g0,g1)
    c: Coincident(g1,g2)
    c: Coincident(g2,g3)
    c: Coincident(g3,g0)
    c: Horizontal(g0)
    c: Horizontal(g2)
    c: Vertical(g1)
    c: Vertical(g3)
    c: Coincident(g0,g-4)
    c: PointOnObject(g1,g-6)
    c: DistanceY(g3,g3) = 40
FEATURE [PartDesign::Pad] Pad030
  BaseFeature = -> Pad029
  Direction = (0,1,-2e-16)
  Length = 2.8
  Length2 = 10
  Profile = -> Sketch019
  ReferenceAxis = -> Sketch019 [N_Axis]
  Refine = true
  Type = 0
FEATURE [Sketcher::SketchObject] Sketch020
  ExternalGeometry = -> [Pad030]
  FullyConstrained = true
  MapMode = 5
  Placement = pos=(91.5,0,0) rot=(0.57735,-0.57735,-0.57735;2.0944rad)
  Support = -> [Pad030]
  sketch-geometry (4):
    g0: LineSegment StartX=-66.1 StartY=-38 StartZ=0 EndX=-64.6 EndY=-38 EndZ=0
    g1: LineSegment StartX=-64.6 StartY=-38 StartZ=0 EndX=-64.6 EndY=2 EndZ=0
    g2: LineSegment StartX=-64.6 StartY=2 StartZ=0 EndX=-66.1 EndY=2 EndZ=0
    g3: LineSegment StartX=-66.1 StartY=2 StartZ=0 EndX=-66.1 EndY=-38 EndZ=0
  constraints (11):
    c: Coincident(g0,g1)
    c: Coincident(g1,g2)
    c: Coincident(g2,g3)
    c: Coincident(g3,g0)
    c: Horizontal(g0)
    c: Horizontal(g2)
    c: Vertical(g1)
    c: Vertical(g3)
    c: Coincident(g0,g-5)
    c: PointOnObject(g1,g-4)
    c: DistanceX(g2,g2) = 1.5
FEATURE [PartDesign::Pad] Pad031
  BaseFeature = -> Pad030
  Direction = (-1,0,0)
  Length = 11
  Length2 = 10
  Profile = -> Sketch020
  ReferenceAxis = -> Sketch020 [N_Axis]
  Refine = true
  Type = 0
FEATURE [PartDesign::Pad] Pad032
  BaseFeature = -> Pad031
  Direction = (0,1,0)
  Length = 2
  Length2 = 10
  Profile = -> Pad031 [Face11]
  Refine = true
  Type = 0
FEATURE [PartDesign::Pocket] Pocket004
  BaseFeature = -> Pad032
  Direction = (-1,0,0)
  Length = 0.6
  Length2 = 5
  Profile = -> Pad032 [Face4]
  Refine = true
  Type = 0
FEATURE [PartDesign::Pocket] Pocket005
  BaseFeature = -> Pocket004
  Direction = (1,0,0)
  Length = 0.4
  Length2 = 5
  Profile = -> Pocket004 [Face10]
  Refine = true
  Type = 0
FEATURE [PartDesign::Pad] Pad033
  BaseFeature = -> Pocket005
  Direction = (1,0,-1e-16)
  Length = 0.4
  Length2 = 10
  Profile = -> Pocket005 [Face21]
  Refine = true
  Type = 0
FEATURE [Sketcher::SketchObject] Sketch021
  ExternalGeometry = -> [Pad033]
  FullyConstrained = true
  MapMode = 5
  Placement = pos=(93.9,1.9e-15,-1.13e-14) rot=(0.57735,0.57735,0.57735;2.0944rad)
  Support = -> [Pad033]
  sketch-geometry (1):
    g0: Circle CenterX=52.6 CenterY=-47.4 CenterZ=0 NormalX=0 NormalY=0 NormalZ=1 AngleXU=0 Radius=1.5
  constraints (3):
    c: Diameter(g0) = 3
    c: DistanceY(g-4,g0) = 3.7
    c: DistanceX(g0,g-4) = 10.7
FEATURE [PartDesign::Pocket] Pocket006
  BaseFeature = -> Pad033
  Direction = (-1,1e-16,1e-16)
  Length = 5
  Length2 = 5
  Profile = -> Sketch021
  ReferenceAxis = -> Sketch021 [N_Axis]
  Refine = true
  Type = 0
FEATURE [Sketcher::SketchObject] Sketch022
  ExternalGeometry = -> [Pad013]
  FullyConstrained = true
  MapMode = 5
  Placement = pos=(91.46,0,0) rot=(0.57735,0.57735,0.57735;2.0944rad)
  Support = -> [Pad013]
  sketch-geometry (1):
    g0: Circle CenterX=52.52 CenterY=3.72 CenterZ=0 NormalX=0 NormalY=0 NormalZ=1 AngleXU=0 Radius=1.4
  constraints (3):
    c: Diameter(g0) = 2.8
    c: DistanceY(g-3,g0) = 3.72
    c: DistanceX(g0,g-3) = 11.12
FEATURE [PartDesign::Pocket] Pocket007
  BaseFeature = -> Pad013
  Direction = (-1,0,0)
  Length = 7
  Length2 = 5
  Profile = -> Sketch022
  ReferenceAxis = -> Sketch022 [N_Axis]
  Refine = true
  Type = 0
FEATURE [Sketcher::SketchObject] Sketch023
  ExternalGeometry = -> [Pocket006]
  FullyConstrained = true
  MapMode = 5
  Placement = pos=(3.65,0,0) rot=(0.57735,-0.57735,-0.57735;2.0944rad)
  Support = -> [Pocket006]
  sketch-geometry (1):
    g0: Circle CenterX=-57.43 CenterY=-47.38 CenterZ=0 NormalX=0 NormalY=0 NormalZ=1 AngleXU=0 Radius=1.5
  constraints (3):
    c: Diameter(g0) = 3
    c: DistanceY(g-3,g0) = 3.62
    c: DistanceX(g-3,g0) = 5.62
FEATURE [PartDesign::Pocket] Pocket008
  BaseFeature = -> Pocket006
  Direction = (1,0,0)
  Length = 5
  Length2 = 5
  Profile = -> Sketch023
  ReferenceAxis = -> Sketch023 [N_Axis]
  Refine = true
  Type = 0
FEATURE [Sketcher::SketchObject] Sketch024
  ExternalGeometry = -> [Pocket007]
  FullyConstrained = true
  MapMode = 5
  Placement = pos=(5.99,0,0) rot=(0.57735,-0.57735,-0.57735;2.0944rad)
  Support = -> [Pocket007]
  sketch-geometry (1):
    g0: Circle CenterX=-57.37 CenterY=3.74 CenterZ=0 NormalX=0 NormalY=0 NormalZ=1 AngleXU=0 Radius=1.4
  constraints (3):
    c: Diameter(g0) = 2.8
    c: DistanceY(g-3,g0) = 3.74
    c: DistanceX(g-3,g0) = 6.27
FEATURE [PartDesign::Pocket] Pocket009
  BaseFeature = -> Pocket007
  Direction = (1,0,0)
  Length = 7
  Length2 = 5
  Profile = -> Sketch024
  ReferenceAxis = -> Sketch024 [N_Axis]
  Refine = true
  Type = 0
FEATURE [PartDesign::Pad] Pad034
  BaseFeature = -> Pocket009
  Direction = (1,0,0)
  Length = 2
  Length2 = 10
  Profile = -> Pocket009 [Face16]
  Refine = true
  Type = 0
FEATURE [PartDesign::Pocket] Pocket010
  BaseFeature = -> Pocket008
  Direction = (1,0,0)
  Length = 0.5
  Length2 = 5
  Profile = -> Pocket008 [Face19]
  Refine = true
  Type = 0
FEATURE [PartDesign::Pocket] Pocket011
  BaseFeature = -> Pocket010
  Direction = (0,1,0)
  Length = 1.2
  Length2 = 5
  Profile = -> Pocket010 [Face1]
  Refine = true
  Type = 0
FEATURE [Sketcher::SketchObject] Sketch025
  ExternalGeometry = -> [Pocket011]
  FullyConstrained = true
  MapMode = 5
  Placement = pos=(0,1e-16,2) rot=(0,0,1;0rad)
  Support = -> [Pocket011]
  sketch-geometry (2):
    g0: Circle CenterX=85.55 CenterY=36.6 CenterZ=0 NormalX=0 NormalY=0 NormalZ=1 AngleXU=0 Radius=2.5
    g1: Circle CenterX=85.55 CenterY=44 CenterZ=0 NormalX=0 NormalY=0 NormalZ=1 AngleXU=0 Radius=2.5
  constraints (6):
    c: Diameter(g1) = 5
    c: Diameter(g0) = 5
    c: DistanceY(g0,g1) = 7.4
    c: DistanceY(g-4,g0) = 21.9
    c: DistanceX(g0,g-4) = 8.35
    c: DistanceX(g1,g0) = 0
FEATURE [PartDesign::Pocket] Pocket012
  BaseFeature = -> Pocket011
  Direction = (0,0,-1)
  Length = 5
  Length2 = 5
  Profile = -> Sketch025
  ReferenceAxis = -> Sketch025 [N_Axis]
  Refine = true
  Type = 0
FEATURE [Sketcher::SketchObject] Sketch026
  ExternalGeometry = -> [Pocket012]
  FullyConstrained = true
  MapMode = 5
  Placement = pos=(0,0,0) rot=(1,0,0;3.14159rad)
  Support = -> [Pocket012]
  sketch-geometry (4):
    g0: Circle CenterX=85.55 CenterY=-36.6 CenterZ=0 NormalX=0 NormalY=0 NormalZ=1 AngleXU=0 Radius=2.5
    g1: Circle CenterX=85.55 CenterY=-44 CenterZ=0 NormalX=0 NormalY=0 NormalZ=1 AngleXU=0 Radius=2.5
    g2: Circle CenterX=85.55 CenterY=-36.6 CenterZ=0 NormalX=0 NormalY=0 NormalZ=1 AngleXU=0 Radius=4
    g3: Circle CenterX=85.55 CenterY=-44 CenterZ=0 NormalX=0 NormalY=0 NormalZ=1 AngleXU=0 Radius=4
  constraints (8):
    c: Coincident(g0,g-3)
    c: Coincident(g1,g-4)
    c: Diameter(g0) = 5
    c: Diameter(g1) = 5
    c: Coincident(g2,g0)
    c: Coincident(g3,g1)
    c: Diameter(g2) = 8
    c: Diameter(g3) = 8
FEATURE [Sketcher::SketchObject] Sketch032
  ExternalGeometry = -> [Pad034]
  FullyConstrained = true
  MapMode = 5
  Placement = pos=(91.96,0,0) rot=(0.57735,0.57735,0.57735;2.0944rad)
  Support = -> [Pad034]
  sketch-geometry (4):
    g0: LineSegment StartX=16.97 StartY=0 StartZ=0 EndX=29.97 EndY=0 EndZ=0
    g1: LineSegment StartX=29.97 StartY=0 StartZ=0 EndX=29.97 EndY=11 EndZ=0
    g2: LineSegment StartX=29.97 StartY=11 StartZ=0 EndX=16.97 EndY=11 EndZ=0
    g3: LineSegment StartX=16.97 StartY=11 StartZ=0 EndX=16.97 EndY=0 EndZ=0
  constraints (11):
    c: Coincident(g0,g1)
    c: Coincident(g1,g2)
    c: Coincident(g2,g3)
    c: Coincident(g3,g0)
    c: Horizontal(g0)
    c: Horizontal(g2)
    c: Vertical(g1)
    c: Vertical(g3)
    c: Coincident(g0,g-4)
    c: PointOnObject(g1,g-5)
    c: DistanceY(g1,g1) = 11
FEATURE [PartDesign::Pad] Pad039
  BaseFeature = -> Pad034
  Direction = (1,0,0)
  Length = 1.9
  Length2 = 10
  Profile = -> Sketch032
  ReferenceAxis = -> Sketch032 [N_Axis]
  Refine = true
  Type = 0
FEATURE [Sketcher::SketchObject] Sketch033
  ExternalGeometry = -> [Pad039]
  FullyConstrained = true
  MapMode = 5
  Placement = pos=(93.86,0,0) rot=(0.57735,0.57735,0.57735;2.0944rad)
  Support = -> [Pad039]
  sketch-geometry (4):
    g0: LineSegment StartX=16.97 StartY=0 StartZ=0 EndX=29.97 EndY=0 EndZ=0
    g1: LineSegment StartX=29.97 StartY=0 StartZ=0 EndX=29.97 EndY=4 EndZ=0
    g2: LineSegment StartX=29.97 StartY=4 StartZ=0 EndX=16.97 EndY=4 EndZ=0
    g3: LineSegment StartX=16.97 StartY=4 StartZ=0 EndX=16.97 EndY=0 EndZ=0
  constraints (11):
    c: Coincident(g0,g1)
    c: Coincident(g1,g2)
    c: Coincident(g2,g3)
    c: Coincident(g3,g0)
    c: Horizontal(g0)
    c: Horizontal(g2)
    c: Vertical(g1)
    c: Vertical(g3)
    c: Coincident(g0,g-4)
    c: PointOnObject(g1,g-5)
    c: DistanceY(g3,g3) = 4
FEATURE [PartDesign::Pad] Pad040
  BaseFeature = -> Pad039
  Direction = (1,0,0)
  Length = 12
  Length2 = 10
  Profile = -> Sketch033
  ReferenceAxis = -> Sketch033 [N_Axis]
  Refine = true
  Type = 0
FEATURE [Sketcher::SketchObject] Sketch034
  ExternalGeometry = -> [Pad040]
  FullyConstrained = true
  MapMode = 5
  Placement = pos=(0,0,4) rot=(0,0,1;0rad)
  Support = -> [Pad040]
  sketch-geometry (1):
    g0: Circle CenterX=99.86 CenterY=23.47 CenterZ=0 NormalX=0 NormalY=0 NormalZ=1 AngleXU=0 Radius=2.5
  constraints (5):
    c: Diameter(g0) = 5
    c: DistanceY(g0,g-5) = 6.5
    c: DistanceY(g-5,g0) = 6.5
    c: DistanceX(g-3,g0) = 6
    c: DistanceX(g0,g-5) = 6
FEATURE [PartDesign::Pocket] Pocket016
  BaseFeature = -> Pad040
  Direction = (0,0,-1)
  Length = 5
  Length2 = 5
  Profile = -> Sketch034
  ReferenceAxis = -> Sketch034 [N_Axis]
  Refine = true
  Type = 0
FEATURE [PartDesign::Fillet] Fillet
  Base = -> Pocket016 [Edge68,Edge72]
  BaseFeature = -> Pocket016
  Radius = 5
  Refine = true
  SupportTransform = false
  UseAllEdges = false
FEATURE [Sketcher::SketchObject] Sketch035
  ExternalGeometry = -> [Fillet]
  FullyConstrained = true
  MapMode = 5
  Placement = pos=(0,98.92,0) rot=(0,0.707107,0.707107;3.14159rad)
  Support = -> [Fillet]
  sketch-geometry (4):
    g0: LineSegment StartX=-19 StartY=0 StartZ=0 EndX=-7 EndY=0 EndZ=0
    g1: LineSegment StartX=-7 StartY=0 StartZ=0 EndX=-7 EndY=4 EndZ=0
    g2: LineSegment StartX=-7 StartY=4 StartZ=0 EndX=-19 EndY=4 EndZ=0
    g3: LineSegment StartX=-19 StartY=4 StartZ=0 EndX=-19 EndY=0 EndZ=0
  constraints (12):
    c: Coincident(g0,g1)
    c: Coincident(g1,g2)
    c: Coincident(g2,g3)
    c: Coincident(g3,g0)
    c: Horizontal(g0)
    c: Horizontal(g2)
    c: Vertical(g1)
    c: Vertical(g3)
    c: PointOnObject(g0,g-3)
    c: DistanceX(g2,g2) = 12
    c: DistanceY(g1,g1) = 4
    c: DistanceX(g0,g-3) = 7
FEATURE [PartDesign::Pad] Pad041
  BaseFeature = -> Fillet
  Direction = (0,1,-2e-16)
  Length = 12
  Length2 = 10
  Profile = -> Sketch035
  ReferenceAxis = -> Sketch035 [N_Axis]
  Refine = true
  Type = 0
FEATURE [Sketcher::SketchObject] Sketch036
  ExternalGeometry = -> [Pad041]
  FullyConstrained = true
  MapMode = 5
  Placement = pos=(0,9e-16,4) rot=(0,0,1;0rad)
  Support = -> [Pad041]
  sketch-geometry (1):
    g0: Circle CenterX=13 CenterY=104.92 CenterZ=0 NormalX=0 NormalY=0 NormalZ=1 AngleXU=0 Radius=2.5
  constraints (5):
    c: Diameter(g0) = 5
    c: DistanceX(g-4,g0) = 6
    c: DistanceX(g0,g-5) = 6
    c: DistanceY(g0,g-4) = 6
    c: DistanceY(g-3,g0) = 6
FEATURE [PartDesign::Pocket] Pocket017
  BaseFeature = -> Pad041
  Direction = (0,-2e-16,-1)
  Length = 5
  Length2 = 5
  Profile = -> Sketch036
  ReferenceAxis = -> Sketch036 [N_Axis]
  Refine = true
  Type = 0
FEATURE [PartDesign::Fillet] Fillet001
  Base = -> Pocket017 [Edge102,Edge105]
  BaseFeature = -> Pocket017
  Radius = 5
  Refine = true
  SupportTransform = false
  UseAllEdges = false
FEATURE [Part::Part2DObjectPython] ShapeString  # Draft 2D object (typed FeaturePython)
  FontFile = <userpath>/Documents/FreeCad/Fonts/Stencil_tenada/Tenada.ttf
  MakeFace = true
  Placement = pos=(0,98.11,0.84) rot=(0.57735,-0.57735,-0.57735;2.0944rad)
  Size = 3.5
  String = AC-IN
  Tracking = 0
FEATURE [PartDesign::Pad] Pad042
  BaseFeature = -> Fillet001
  Direction = (-1,0,0)
  Length = 1
  Length2 = 10
  Profile = -> ShapeString
  ReferenceAxis = -> ShapeString [N_Axis]
  Refine = true
  Type = 0
FEATURE [Part::Part2DObjectPython] ShapeString001  # Draft 2D object (typed FeaturePython)
  FontFile = <userpath>/Documents/FreeCad/Fonts/Stencil_tenada/Tenada.ttf
  MakeFace = true
  Placement = pos=(100.82,63.75,1.31) rot=(0.57735,0.57735,0.57735;2.0944rad)
  Size = 3
  String = AC.OUT
  Tracking = 0
FEATURE [PartDesign::Pad] Pad043
  BaseFeature = -> Pad042
  Direction = (1,0,0)
  Length = 1
  Length2 = 10
  Profile = -> ShapeString001
  ReferenceAxis = -> ShapeString001 [N_Axis]
  Refine = true
  Type = 0
FEATURE [PartDesign::Pocket] Pocket020
  BaseFeature = -> Pad021
  Direction = (0,-1,-1e-16)
  Length = 1
  Length2 = 5
  Profile = -> Pad021 [Face9]
  Refine = true
  Type = 0
FEATURE [PartDesign::Pocket] Pocket021
  BaseFeature = -> Pocket020
  Direction = (-1,0,0)
  Length = 1
  Length2 = 5
  Profile = -> Pocket020 [Face1]
  Refine = true
  Type = 0
FEATURE [PartDesign::Fillet] Fillet002
  Base = -> Pocket021 [Edge27,Edge22,Edge25,Edge23]
  BaseFeature = -> Pocket021
  Radius = 1
  Refine = true
  SupportTransform = false
  UseAllEdges = false
FEATURE [PartDesign::Pad] Pad045
  BaseFeature = -> Fillet002
  Direction = (0,0,1)
  Length = 2
  Length2 = 10
  Profile = -> Fillet002 [Face14]
  Refine = true
  Type = 0
FEATURE [PartDesign::Pocket] Pocket022
  BaseFeature = -> Pad045
  Direction = (0,0,1)
  Length = 2
  Length2 = 5
  Profile = -> Pad045 [Face1]
  Refine = true
  Type = 0
FEATURE [PartDesign::Body] Body002  label="LidBoton"
  Group = -> [Sketch009,Pad015,Sketch010,Pad016,Sketch011,Pocket001,Pad020,Pad021,Pocket020,Pocket021,Fillet002,Pad045,Pocket022]
  Origin = -> Origin051
  Placement = pos=(-0.2,0.465,-28.99) rot=(0,0,1;0rad)
  Tip = -> Pocket022
FEATURE [PartDesign::Pad] Pad035
  BaseFeature = -> Pocket012
  Direction = (0,0,-1)
  Length = 38
  Length2 = 10
  Profile = -> Sketch026
  ReferenceAxis = -> Sketch026 [N_Axis]
  Refine = true
  Type = 0
FEATURE [Sketcher::SketchObject] Sketch027
  ExternalGeometry = -> [Pad035]
  FullyConstrained = true
  MapMode = 5
  Placement = pos=(91.9,0,0) rot=(0.57735,-0.57735,-0.57735;2.0944rad)
  Support = -> [Pad035]
  sketch-geometry (4):
    g0: LineSegment StartX=-62.1 StartY=-11.8 StartZ=0 EndX=-53.3 EndY=-11.8 EndZ=0
    g1: LineSegment StartX=-53.3 StartY=-11.8 StartZ=0 EndX=-53.3 EndY=-3 EndZ=0
    g2: LineSegment StartX=-53.3 StartY=-3 StartZ=0 EndX=-62.1 EndY=-3 EndZ=0
    g3: LineSegment StartX=-62.1 StartY=-3 StartZ=0 EndX=-62.1 EndY=-11.8 EndZ=0
  constraints (12):
    c: Coincident(g0,g1)
    c: Coincident(g1,g2)
    c: Coincident(g2,g3)
    c: Coincident(g3,g0)
    c: Horizontal(g0)
    c: Horizontal(g2)
    c: Vertical(g1)
    c: Vertical(g3)
    c: DistanceY(g3,g3) = 8.8
    c: DistanceX(g2,g2) = 8.8
    c: DistanceY(g1,g-4) = 5
    c: DistanceX(g-4,g2) = 4
FEATURE [PartDesign::Pocket] Pocket013
  BaseFeature = -> Pad035
  Direction = (1,0,0)
  Length = 1
  Length2 = 5
  Profile = -> Sketch027
  ReferenceAxis = -> Sketch027 [N_Axis]
  Refine = true
  Type = 0
FEATURE [Sketcher::SketchObject] Sketch028
  ExternalGeometry = -> [Pocket013]
  FullyConstrained = true
  MapMode = 5
  Placement = pos=(92.9,0,0) rot=(0.57735,-0.57735,-0.57735;2.0944rad)
  Support = -> [Pocket013]
  sketch-geometry (1):
    g0: Circle CenterX=-57.7 CenterY=-7.4 CenterZ=0 NormalX=0 NormalY=0 NormalZ=1 AngleXU=0 Radius=3.5
  constraints (5):
    c: Diameter(g0) = 7
    c: DistanceX(g0,g-5) = 4.4
    c: DistanceX(g-4,g0) = 4.4
    c: DistanceY(g0,g-5) = 4.4
    c: DistanceY(g-5,g0) = 4.4
FEATURE [PartDesign::Pocket] Pocket014
  BaseFeature = -> Pocket013
  Direction = (1,0,0)
  Length = 5
  Length2 = 5
  Profile = -> Sketch028
  ReferenceAxis = -> Sketch028 [N_Axis]
  Refine = true
  Type = 0
FEATURE [Sketcher::SketchObject] Sketch029
  ExternalGeometry = -> [Pocket014]
  FullyConstrained = true
  MapMode = 5
  Placement = pos=(91.9,0,0) rot=(0.57735,-0.57735,-0.57735;2.0944rad)
  Support = -> [Pocket014]
  sketch-geometry (8):
    g0: LineSegment StartX=-64.6 StartY=-16 StartZ=0 EndX=-50.6 EndY=-16 EndZ=0
    g1: LineSegment StartX=-50.6 StartY=-16 StartZ=0 EndX=-50.6 EndY=0 EndZ=0
    g2: LineSegment StartX=-50.6 StartY=0 StartZ=0 EndX=-64.6 EndY=0 EndZ=0
    g3: LineSegment StartX=-64.6 StartY=0 StartZ=0 EndX=-64.6 EndY=-16 EndZ=0
    g4: LineSegment StartX=-62.1 StartY=-11.8 StartZ=0 EndX=-53.3 EndY=-11.8 EndZ=0
    g5: LineSegment StartX=-53.3 StartY=-11.8 StartZ=0 EndX=-53.3 EndY=-3 EndZ=0
    g6: LineSegment StartX=-53.3 StartY=-3 StartZ=0 EndX=-62.1 EndY=-3 EndZ=0
    g7: LineSegment StartX=-62.1 StartY=-3 StartZ=0 EndX=-62.1 EndY=-11.8 EndZ=0
  constraints (21):
    c: Coincident(g0,g1)
    c: Coincident(g1,g2)
    c: Coincident(g2,g3)
    c: Coincident(g3,g0)
    c: Horizontal(g0)
    c: Horizontal(g2)
    c: Vertical(g1)
    c: Vertical(g3)
    c: Coincident(g2,g-4)
    c: DistanceX(g2,g2) = 14
    c: DistanceY(g1,g1) = 16
    c: Coincident(g4,g5)
    c: Coincident(g5,g6)
    c: Coincident(g6,g7)
    c: Coincident(g7,g4)
    c: Horizontal(g4)
    c: Horizontal(g6)
    c: Vertical(g5)
    c: Vertical(g7)
    c: Coincident(g4,g-8)
    c: Coincident(g5,g-7)
FEATURE [PartDesign::Pad] Pad036
  BaseFeature = -> Pocket014
  Direction = (-1,0,0)
  Length = 2
  Length2 = 10
  Profile = -> Sketch029
  ReferenceAxis = -> Sketch029 [N_Axis]
  Refine = true
  Type = 0
FEATURE [PartDesign::Pad] Pad037
  BaseFeature = -> Pad036
  Direction = (-1,0,0)
  Length = 1
  Length2 = 10
  Profile = -> Pad036 [Face48]
  Refine = true
  Type = 0
FEATURE [Sketcher::SketchObject] Sketch030
  ExternalGeometry = -> [Pad037]
  FullyConstrained = true
  MapMode = 5
  Placement = pos=(0,1e-16,2) rot=(0,0,1;0rad)
  Support = -> [Pad037]
  sketch-geometry (4):
    g0: LineSegment StartX=39.5 StartY=78.15 StartZ=0 EndX=62.3 EndY=78.15 EndZ=0
    g1: LineSegment StartX=62.3 StartY=78.15 StartZ=0 EndX=62.3 EndY=65.35 EndZ=0
    g2: LineSegment StartX=62.3 StartY=65.35 StartZ=0 EndX=39.5 EndY=65.35 EndZ=0
    g3: LineSegment StartX=39.5 StartY=65.35 StartZ=0 EndX=39.5 EndY=78.15 EndZ=0
  constraints (12):
    c: Coincident(g0,g1)
    c: Coincident(g1,g2)
    c: Coincident(g2,g3)
    c: Coincident(g3,g0)
    c: Horizontal(g0)
    c: Horizontal(g2)
    c: Vertical(g1)
    c: Vertical(g3)
    c: DistanceX(g0,g0) = 22.8
    c: DistanceY(g1,g1) = 12.8
    c: DistanceY(g0,g-3) = 23
    c: DistanceX(g-4,g0) = 18.5
FEATURE [PartDesign::Pocket] Pocket015
  BaseFeature = -> Pad037
  Direction = (0,0,-1)
  Length = 5
  Length2 = 5
  Profile = -> Sketch030
  ReferenceAxis = -> Sketch030 [N_Axis]
  Refine = true
  Type = 0
FEATURE [Sketcher::SketchObject] Sketch031
  ExternalGeometry = -> [Pocket015]
  FullyConstrained = true
  MapMode = 5
  Placement = pos=(0,0,0) rot=(1,0,0;3.14159rad)
  Support = -> [Pocket015]
  sketch-geometry (8):
    g0: LineSegment StartX=37 StartY=-55.85 StartZ=0 EndX=64.8 EndY=-55.85 EndZ=0
    g1: LineSegment StartX=64.8 StartY=-55.85 StartZ=0 EndX=64.8 EndY=-84.65 EndZ=0
    g2: LineSegment StartX=64.8 StartY=-84.65 StartZ=0 EndX=37 EndY=-84.65 EndZ=0
    g3: LineSegment StartX=37 StartY=-84.65 StartZ=0 EndX=37 EndY=-55.85 EndZ=0
    g4: LineSegment StartX=35 StartY=-53.85 StartZ=0 EndX=66.8 EndY=-53.85 EndZ=0
    g5: LineSegment StartX=66.8 StartY=-53.85 StartZ=0 EndX=66.8 EndY=-86.65 EndZ=0
    g6: LineSegment StartX=66.8 StartY=-86.65 StartZ=0 EndX=35 EndY=-86.65 EndZ=0
    g7: LineSegment StartX=35 StartY=-86.65 StartZ=0 EndX=35 EndY=-53.85 EndZ=0
  constraints (24):
    c: Coincident(g0,g1)
    c: Coincident(g1,g2)
    c: Coincident(g2,g3)
    c: Coincident(g3,g0)
    c: Horizontal(g0)
    c: Horizontal(g2)
    c: Vertical(g1)
    c: Vertical(g3)
    c: Coincident(g4,g5)
    c: Coincident(g5,g6)
    c: Coincident(g6,g7)
    c: Coincident(g7,g4)
    c: Horizontal(g4)
    c: Horizontal(g6)
    c: Vertical(g5)
    c: Vertical(g7)
    c: DistanceY(g2,g-3) = 6.5
    c: DistanceY(g-4,g0) = 9.5
    c: DistanceY(g6,g2) = 2
    c: DistanceY(g0,g4) = 2
    c: DistanceX(g-3,g1) = 2.5
    c: DistanceX(g2,g-3) = 2.5
    c: DistanceX(g1,g5) = 2
    c: DistanceX(g4,g0) = 2
FEATURE [PartDesign::Pad] Pad038
  BaseFeature = -> Pocket015
  Direction = (0,0,-1)
  Length = 3
  Length2 = 10
  Profile = -> Sketch031
  ReferenceAxis = -> Sketch031 [N_Axis]
  Refine = true
  Type = 0
FEATURE [Part::Part2DObjectPython] ShapeString002  # Draft 2D object (typed FeaturePython)
  AttachmentOffset = pos=(22,53,0) rot=(0,0,1;0rad)
  FontFile = <userpath>/Documents/FreeCad/Fonts/Stencil_tenada/Tenada.ttf
  MakeFace = true
  MapMode = 5
  Placement = pos=(22,14.7,53) rot=(1,0,0;1.5708rad)
  Size = 2.5
  String = WiFi Smart Pump
  Support = -> [Pad038]
  Tracking = 0
FEATURE [PartDesign::Pocket] Pocket018
  BaseFeature = -> Pad038
  Direction = (0,1,-2e-16)
  Length = 0.7
  Length2 = 5
  Profile = -> ShapeString002
  ReferenceAxis = -> ShapeString002 [N_Axis]
  Refine = true
  Type = 0
FEATURE [Part::Part2DObjectPython] ShapeString003  # Draft 2D object (typed FeaturePython)
  AttachmentOffset = pos=(33,43,0) rot=(0,0,1;0rad)
  FontFile = <userpath>/Documents/FreeCad/Fonts/Stencil_tenada/Tenada.ttf
  MakeFace = true
  MapMode = 5
  Placement = pos=(33,14.7,43) rot=(1,0,0;1.5708rad)
  Size = 2.4
  String = Controller S1
  Support = -> [Pocket018]
  Tracking = 0
FEATURE [PartDesign::Pocket] Pocket019
  BaseFeature = -> Pocket018
  Direction = (0,1,-2e-16)
  Length = 0.7
  Length2 = 5
  Profile = -> ShapeString003
  ReferenceAxis = -> ShapeString003 [N_Axis]
  Refine = true
  Type = 0
FEATURE [PartDesign::Pad] Pad044
  BaseFeature = -> Pocket019
  Direction = (0,-1,0)
  Length = 1
  Length2 = 10
  Profile = -> Pocket019 [Face29]
  Refine = true
  Type = 0
FEATURE [Sketcher::SketchObject] Sketch037
  ExternalGeometry = -> [Pad044]
  FullyConstrained = false
  MapMode = 5
  Placement = pos=(0,1e-16,2) rot=(0,0,1;0rad)
  Support = -> [Pad044]
  sketch-geometry (4):
    g0: LineSegment StartX=93.9 StartY=48.3611 StartZ=0 EndX=81.2 EndY=48.3611 EndZ=0
    g1: LineSegment StartX=81.2 StartY=48.3611 StartZ=0 EndX=81.2 EndY=32.3611 EndZ=0
    g2: LineSegment StartX=81.2 StartY=32.3611 StartZ=0 EndX=93.9 EndY=32.3611 EndZ=0
    g3: LineSegment StartX=93.9 StartY=32.3611 StartZ=0 EndX=93.9 EndY=48.3611 EndZ=0
  constraints (11):
    c: Coincident(g0,g1)
    c: Coincident(g1,g2)
    c: Coincident(g2,g3)
    c: Coincident(g3,g0)
    c: Horizontal(g0)
    c: Horizontal(g2)
    c: Vertical(g1)
    c: Vertical(g3)
    c: PointOnObject(g0,g-3)
    c: DistanceY(g1,g1) = 16
    c: DistanceX(g0,g0) = 12.7
FEATURE [PartDesign::Pocket] Pocket023
  BaseFeature = -> Pad044
  Direction = (0,0,-1)
  Length = 122
  Length2 = 5
  Profile = -> Sketch037
  ReferenceAxis = -> Sketch037 [N_Axis]
  Refine = true
  Type = 0
FEATURE [PartDesign::Pocket] Pocket024
  BaseFeature = -> Pocket023
  Direction = (0,0,1)
  Length = 1
  Length2 = 5
  Profile = -> Pocket023 [Face46]
  Refine = true
  Type = 0
FEATURE [PartDesign::Pocket] Pocket025
  BaseFeature = -> Pocket024
  Direction = (0,0,-1)
  Length = 1
  Length2 = 5
  Profile = -> Pocket024 [Face45]
  Refine = true
  Type = 0
FEATURE [PartDesign::Pad] Pad046
  BaseFeature = -> Pocket025
  Direction = (1,0,0)
  Length = 2
  Length2 = 10
  Profile = -> Pocket025 [Face13]
  Refine = true
  Type = 0
FEATURE [PartDesign::Pad] Pad047
  BaseFeature = -> Pad046
  Direction = (0,-1,0)
  Length = 2.5
  Length2 = 10
  Profile = -> Pad046 [Face1]
  Refine = true
  Type = 0
FEATURE [PartDesign::Pad] Pad048
  BaseFeature = -> Pad047
  Direction = (0,1,0)
  Length = 3.5
  Length2 = 10
  Profile = -> Pad047 [Face19]
  Refine = true
  Type = 0
FEATURE [Sketcher::SketchObject] Sketch038
  ExternalGeometry = -> [Pad048]
  FullyConstrained = true
  MapMode = 5
  Placement = pos=(0,0,0) rot=(1,0,0;3.14159rad)
  Support = -> [Pad048]
  sketch-geometry (4):
    g0: LineSegment StartX=83.2 StartY=-33.8611 StartZ=0 EndX=81.7 EndY=-33.8611 EndZ=0
    g1: LineSegment StartX=81.7 StartY=-33.8611 StartZ=0 EndX=81.7 EndY=-47.8611 EndZ=0
    g2: LineSegment StartX=81.7 StartY=-47.8611 StartZ=0 EndX=83.2 EndY=-47.8611 EndZ=0
    g3: LineSegment StartX=83.2 StartY=-47.8611 StartZ=0 EndX=83.2 EndY=-33.8611 EndZ=0
  constraints (12):
    c: Coincident(g0,g1)
    c: Coincident(g1,g2)
    c: Coincident(g2,g3)
    c: Coincident(g3,g0)
    c: Horizontal(g0)
    c: Horizontal(g2)
    c: Vertical(g1)
    c: Vertical(g3)
    c: PointOnObject(g0,g-3)
    c: DistanceY(g-3,g0) = 2
    c: DistanceY(g2,g-3) = 2
    c: DistanceX(g0,g0) = 1.5
FEATURE [PartDesign::Pad] Pad049
  BaseFeature = -> Pad048
  Direction = (0,0,-1)
  Length = 38.4
  Length2 = 10
  Profile = -> Sketch038
  ReferenceAxis = -> Sketch038 [N_Axis]
  Refine = true
  Type = 0
FEATURE [Sketcher::SketchObject] Sketch039
  ExternalGeometry = -> [Pad049]
  FullyConstrained = true
  MapMode = 5
  Placement = pos=(83.2,0,3.24e-14) rot=(0.57735,0.57735,0.57735;2.0944rad)
  Support = -> [Pad049]
  sketch-geometry (8):
    g0: LineSegment StartX=47.8611 StartY=-3.55e-14 StartZ=0 EndX=45.8611 EndY=-3.55e-14 EndZ=0
    g1: LineSegment StartX=45.8611 StartY=-3.55e-14 StartZ=0 EndX=45.8611 EndY=-38.4 EndZ=0
    g2: LineSegment StartX=45.8611 StartY=-38.4 StartZ=0 EndX=47.8611 EndY=-38.4 EndZ=0
    g3: LineSegment StartX=47.8611 StartY=-38.4 StartZ=0 EndX=47.8611 EndY=-3.55e-14 EndZ=0
    g4: LineSegment StartX=33.8611 StartY=0 StartZ=0 EndX=35.8611 EndY=0 EndZ=0
    g5: LineSegment StartX=35.8611 StartY=0 StartZ=0 EndX=35.8611 EndY=-38.4 EndZ=0
    g6: LineSegment StartX=35.8611 StartY=-38.4 StartZ=0 EndX=33.8611 EndY=-38.4 EndZ=0
    g7: LineSegment StartX=33.8611 StartY=-38.4 StartZ=0 EndX=33.8611 EndY=0 EndZ=0
  constraints (23):
    c: Coincident(g0,g1)
    c: Coincident(g1,g2)
    c: Coincident(g2,g3)
    c: Coincident(g3,g0)
    c: Horizontal(g0)
    c: Horizontal(g2)
    c: Vertical(g1)
    c: Vertical(g3)
    c: Coincident(g0,g-4)
    c: PointOnObject(g1,g-5)
    c: DistanceX(g2,g2) = 2
    c: Coincident(g4,g5)
    c: Coincident(g5,g6)
    c: Coincident(g6,g7)
    c: Coincident(g7,g4)
    c: Horizontal(g4)
    c: Horizontal(g6)
    c: Vertical(g5)
    c: Vertical(g7)
    c: PointOnObject(g4,g-3)
    c: DistanceX(g4,g4) = 2
    c: PointOnObject(g5,g-5)
    c: PointOnObject(g4,g-1)
FEATURE [PartDesign::Pad] Pad050
  BaseFeature = -> Pad049
  Direction = (1,0,4e-16)
  Length = 9
  Length2 = 10
  Profile = -> Sketch039
  ReferenceAxis = -> Sketch039 [N_Axis]
  Refine = true
  Type = 0
FEATURE [Sketcher::SketchObject] Sketch040
  ExternalGeometry = -> [Pad050]
  FullyConstrained = true
  MapMode = 5
  Placement = pos=(83.2,0,3.24e-14) rot=(0.57735,0.57735,0.57735;2.0944rad)
  Support = -> [Pad050]
  sketch-geometry (4):
    g0: LineSegment StartX=35.8611 StartY=-33.4 StartZ=0 EndX=45.8611 EndY=-33.4 EndZ=0
    g1: LineSegment StartX=45.8611 StartY=-33.4 StartZ=0 EndX=45.8611 EndY=-36.4 EndZ=0
    g2: LineSegment StartX=45.8611 StartY=-36.4 StartZ=0 EndX=35.8611 EndY=-36.4 EndZ=0
    g3: LineSegment StartX=35.8611 StartY=-36.4 StartZ=0 EndX=35.8611 EndY=-33.4 EndZ=0
  constraints (12):
    c: Coincident(g0,g1)
    c: Coincident(g1,g2)
    c: Coincident(g2,g3)
    c: Coincident(g3,g0)
    c: Horizontal(g0)
    c: Horizontal(g2)
    c: Vertical(g1)
    c: Vertical(g3)
    c: DistanceY(g-3,g2) = 2
    c: DistanceY(g3,g3) = 3
    c: PointOnObject(g0,g-5)
    c: PointOnObject(g0,g-4)
FEATURE [PartDesign::Pad] Pad051
  BaseFeature = -> Pad050
  Direction = (1,0,4e-16)
  Length = 10.7
  Length2 = 10
  Profile = -> Sketch040
  ReferenceAxis = -> Sketch040 [N_Axis]
  Refine = true
  Type = 0
FEATURE [Sketcher::SketchObject] Sketch041
  ExternalGeometry = -> [Pad051]
  FullyConstrained = true
  MapMode = 5
  Placement = pos=(0,45.8611,0) rot=(1,0,0;1.5708rad)
  Support = -> [Pad051]
  sketch-geometry (4):
    g0: LineSegment StartX=91.9 StartY=-51.1 StartZ=0 EndX=93.9 EndY=-51.1 EndZ=0
    g1: LineSegment StartX=93.9 StartY=-51.1 StartZ=0 EndX=93.9 EndY=-36.4 EndZ=0
    g2: LineSegment StartX=93.9 StartY=-36.4 StartZ=0 EndX=91.9 EndY=-36.4 EndZ=0
    g3: LineSegment StartX=91.9 StartY=-36.4 StartZ=0 EndX=91.9 EndY=-51.1 EndZ=0
  constraints (11):
    c: Coincident(g0,g1)
    c: Coincident(g1,g2)
    c: Coincident(g2,g3)
    c: Coincident(g3,g0)
    c: Horizontal(g0)
    c: Horizontal(g2)
    c: Vertical(g1)
    c: Vertical(g3)
    c: Coincident(g0,g-3)
    c: PointOnObject(g0,g-5)
    c: PointOnObject(g1,g-4)
FEATURE [PartDesign::Pad] Pad052
  BaseFeature = -> Pad051
  Direction = (0,-1,2e-16)
  Length = 10
  Length2 = 10
  Profile = -> Sketch041
  ReferenceAxis = -> Sketch041 [N_Axis]
  Refine = true
  Type = 0
FEATURE [PartDesign::Fillet] Fillet003
  Base = -> Pad052 [Edge32,Edge28]
  BaseFeature = -> Pad052
  Radius = 2
  Refine = true
  SupportTransform = false
  UseAllEdges = false
FEATURE [PartDesign::Fillet] Fillet004
  Base = -> Fillet003 [Edge166,Edge164]
  BaseFeature = -> Fillet003
  Radius = 3
  Refine = true
  SupportTransform = false
  UseAllEdges = false
FEATURE [Sketcher::SketchObject] Sketch042
  ExternalGeometry = -> [Fillet004]
  FullyConstrained = true
  MapMode = 5
  Placement = pos=(1.6e-14,0,-36.4) rot=(1,0,0;3.14159rad)
  Support = -> [Fillet004]
  sketch-geometry (8):
    g0: LineSegment StartX=83.51 StartY=-36.0511 StartZ=0 EndX=86.81 EndY=-36.0511 EndZ=0
    g1: LineSegment StartX=86.81 StartY=-36.0511 StartZ=0 EndX=86.81 EndY=-38.0511 EndZ=0
    g2: LineSegment StartX=86.81 StartY=-38.0511 StartZ=0 EndX=83.51 EndY=-38.0511 EndZ=0
    g3: LineSegment StartX=83.51 StartY=-38.0511 StartZ=0 EndX=83.51 EndY=-36.0511 EndZ=0
    g4: LineSegment StartX=83.51 StartY=-45.4811 StartZ=0 EndX=86.81 EndY=-45.4811 EndZ=0
    g5: LineSegment StartX=86.81 StartY=-45.4811 StartZ=0 EndX=86.81 EndY=-43.4811 EndZ=0
    g6: LineSegment StartX=86.81 StartY=-43.4811 StartZ=0 EndX=83.51 EndY=-43.4811 EndZ=0
    g7: LineSegment StartX=83.51 StartY=-43.4811 StartZ=0 EndX=83.51 EndY=-45.4811 EndZ=0
  constraints (24):
    c: Coincident(g0,g1)
    c: Coincident(g1,g2)
    c: Coincident(g2,g3)
    c: Coincident(g3,g0)
    c: Horizontal(g0)
    c: Horizontal(g2)
    c: Vertical(g1)
    c: Vertical(g3)
    c: Coincident(g4,g5)
    c: Coincident(g5,g6)
    c: Coincident(g6,g7)
    c: Coincident(g7,g4)
    c: Horizontal(g4)
    c: Horizontal(g6)
    c: Vertical(g5)
    c: Vertical(g7)
    c: DistanceX(g0,g0) = 3.3
    c: DistanceY(g1,g1) = 2
    c: DistanceY(g5,g5) = 2
    c: DistanceX(g6,g6) = 3.3
    c: DistanceX(g-3,g2) = 0.31
    c: DistanceX(g-3,g4) = 0.31
    c: DistanceY(g2,g-3) = 2.19
    c: DistanceY(g-3,g6) = 2.38
FEATURE [PartDesign::Pocket] Pocket026
  BaseFeature = -> Fillet004
  Direction = (-4e-16,0,1)
  Length = 2.4
  Length2 = 5
  Profile = -> Sketch042
  ReferenceAxis = -> Sketch042 [N_Axis]
  Refine = true
  Type = 0
FEATURE [Sketcher::SketchObject] Sketch043
  ExternalGeometry = -> [Pocket026]
  FullyConstrained = true
  MapMode = 5
  Placement = pos=(1.6e-14,0,-36.4) rot=(1,0,0;3.14159rad)
  Support = -> [Pocket026]
  sketch-geometry (4):
    g0: LineSegment StartX=83.2 StartY=-39.8611 StartZ=0 EndX=91.9 EndY=-39.8611 EndZ=0
    g1: LineSegment StartX=91.9 StartY=-39.8611 StartZ=0 EndX=91.9 EndY=-41.8611 EndZ=0
    g2: LineSegment StartX=91.9 StartY=-41.8611 StartZ=0 EndX=83.2 EndY=-41.8611 EndZ=0
    g3: LineSegment StartX=83.2 StartY=-41.8611 StartZ=0 EndX=83.2 EndY=-39.8611 EndZ=0
  constraints (13):
    c: Coincident(g0,g1)
    c: Coincident(g1,g2)
    c: Coincident(g2,g3)
    c: Coincident(g3,g0)
    c: Horizontal(g0)
    c: Horizontal(g2)
    c: Vertical(g1)
    c: Vertical(g3)
    c: PointOnObject(g0,g-3)
    c: PointOnObject(g1,g-4)
    c: DistanceY(g3,g3) = 2
    c: DistanceY(g0,g-3) = 4
    c: DistanceY(g-3,g2) = 4
FEATURE [PartDesign::Pad] Pad053
  BaseFeature = -> Pocket026
  Direction = (4e-16,0,-1)
  Length = 2
  Length2 = 10
  Profile = -> Sketch043
  ReferenceAxis = -> Sketch043 [N_Axis]
  Refine = true
  Type = 0
FEATURE [PartDesign::Pad] Pad054
  BaseFeature = -> Pad053
  Direction = (0,-1,0)
  Length = 0.3
  Length2 = 10
  Profile = -> Pad053 [Face26]
  Refine = true
  Type = 0
FEATURE [PartDesign::Pad] Pad055
  BaseFeature = -> Pad054
  Direction = (0,0,-1)
  Length = 0.1
  Length2 = 10
  Profile = -> Pad054 [Face25]
  Refine = true
  Type = 0
FEATURE [Sketcher::SketchObject] Sketch044
  ExternalGeometry = -> [Pad055]
  FullyConstrained = true
  MapMode = 5
  Placement = pos=(-2e-16,16.7,-1e-15) rot=(0,0.707107,0.707107;3.14159rad)
  Support = -> [Pad055]
  sketch-geometry (4):
    g0: LineSegment StartX=-93.9 StartY=-28.8 StartZ=0 EndX=-92.2 EndY=-28.8 EndZ=0
    g1: LineSegment StartX=-92.2 StartY=-28.8 StartZ=0 EndX=-92.2 EndY=-39.8 EndZ=0
    g2: LineSegment StartX=-92.2 StartY=-39.8 StartZ=0 EndX=-93.9 EndY=-39.8 EndZ=0
    g3: LineSegment StartX=-93.9 StartY=-39.8 StartZ=0 EndX=-93.9 EndY=-28.8 EndZ=0
  constraints (11):
    c: Coincident(g0,g1)
    c: Coincident(g1,g2)
    c: Coincident(g2,g3)
    c: Coincident(g3,g0)
    c: Horizontal(g0)
    c: Horizontal(g2)
    c: Vertical(g1)
    c: Vertical(g3)
    c: Coincident(g0,g-3)
    c: DistanceY(g3,g3) = 11
    c: DistanceX(g0,g0) = 1.7
FEATURE [PartDesign::Pad] Pad056
  BaseFeature = -> Pad055
  Direction = (0,1,-2e-16)
  Length = 2
  Length2 = 10
  Profile = -> Sketch044
  ReferenceAxis = -> Sketch044 [N_Axis]
  Refine = true
  Type = 0
FEATURE [Part::Part2DObjectPython] ShapeString004  # Draft 2D object (typed FeaturePython)
  AttachmentOffset = pos=(-25,-17,0) rot=(0,0,1;3.14159rad)
  FontFile = <userpath>/Documents/FreeCad/Fonts/Stencil_tenada/Tenada.ttf
  MakeFace = true
  MapMode = 5
  Placement = pos=(25,101.15,-17) rot=(1,0,0;4.71239rad)
  Size = 3
  String = WaterLevel
  Support = -> [Pad056]
  Tracking = 0
FEATURE [PartDesign::Pad] Pad057
  BaseFeature = -> Pad056
  Direction = (0,1,-2e-16)
  Length = 1
  Length2 = 10
  Profile = -> ShapeString004
  ReferenceAxis = -> ShapeString004 [N_Axis]
  Refine = true
  Type = 0
FEATURE [Part::Part2DObjectPython] ShapeString005  # Draft 2D object (typed FeaturePython)
  AttachmentOffset = pos=(-43,-7,0) rot=(0,0,1;3.14159rad)
  FontFile = <userpath>/Documents/FreeCad/Fonts/Stencil_tenada/Tenada.ttf
  MakeFace = true
  MapMode = 5
  Placement = pos=(43,101.15,-7) rot=(1,0,0;4.71239rad)
  Size = 3
  String = .Pro
  Support = -> [Pad057]
  Tracking = 0
FEATURE [PartDesign::Pad] Pad058
  BaseFeature = -> Pad057
  Direction = (0,1,-2e-16)
  Length = 1
  Length2 = 10
  Profile = -> ShapeString005
  ReferenceAxis = -> ShapeString005 [N_Axis]
  Refine = true
  Type = 0
FEATURE [Part::Part2DObjectPython] ShapeString006  # Draft 2D object (typed FeaturePython)
  FontFile = <userpath>/Documents/FreeCad/Fonts/Stencil_tenada/Tenada.ttf
  MakeFace = true
  Placement = pos=(9.94,53.93,2) rot=(0,0,1;0rad)
  Size = 2.7
  String = Smart Water Pump
  Tracking = 0
FEATURE [Part::Part2DObjectPython] ShapeString007  # Draft 2D object (typed FeaturePython)
  FontFile = <userpath>/Documents/FreeCad/Fonts/Stencil_tenada/Tenada.ttf
  MakeFace = true
  Placement = pos=(32,42.9,2) rot=(0,0,1;0rad)
  Size = 2.5
  String = Controller S1
  Tracking = 0
FEATURE [PartDesign::Pocket] Pocket027
  BaseFeature = -> Pad058
  Direction = (0,0,-1)
  Length = 0.7
  Length2 = 5
  Profile = -> ShapeString006
  ReferenceAxis = -> ShapeString006 [N_Axis]
  Refine = true
  Type = 0
FEATURE [PartDesign::Pocket] Pocket028
  BaseFeature = -> Pocket027
  Direction = (0,0,-1)
  Length = 0.7
  Length2 = 5
  Profile = -> ShapeString007
  ReferenceAxis = -> ShapeString007 [N_Axis]
  Refine = true
  Type = 0
FEATURE [PartDesign::Boolean] Boolean
  BaseFeature = -> Pocket028
  Group = -> [Body002]
  Refine = true
  Type = 0
FEATURE [PartDesign::Pad] Pad059
  BaseFeature = -> Pad043
  Direction = (1,0,0)
  Length = 0.4
  Length2 = 10
  Profile = -> Pad043 [Face131]
  Refine = true
  Type = 0
FEATURE [PartDesign::Pocket] Pocket029
  BaseFeature = -> Pad059
  Direction = (1,0,0)
  Length = 0.4
  Length2 = 5
  Profile = -> Pad059 [Face126]
  Refine = true
  Type = 0
FEATURE [PartDesign::Pocket] Pocket030
  BaseFeature = -> Boolean
  Direction = (0,-1,0)
  Length = 1.85
  Length2 = 5
  Profile = -> Boolean [Face74]
  Refine = true
  Type = 0
FEATURE [PartDesign::Pad] Pad060
  BaseFeature = -> Pocket029
  Direction = (1,0,0)
  Length = 1.5
  Length2 = 10
  Profile = -> Pocket029 [Face127]
  Refine = true
  Type = 0
FEATURE [PartDesign::Pad] Pad061
  BaseFeature = -> Pocket030
  Direction = (0,0,-1)
  Length = 0.01
  Length2 = 10
  Profile = -> Pocket030 [Face40]
  Refine = true
  Type = 0
FEATURE [Part::Feature] Part__Feature  label="TopSilk"
  Placement = pos=(0,0,1.62005) rot=(0,0,1;0rad)
  shape: bbox 1.968 x 2.555 x 2e-07 mm, 1 faces, 0 solids (baked)
FEATURE [Part::Feature] Part__Feature001  label="TopSilk001"
  Placement = pos=(0,0,1.62005) rot=(0,0,1;0rad)
  shape: bbox 1.872 x 2.555 x 2e-07 mm, 1 faces, 0 solids (baked)
FEATURE [Part::Feature] Part__Feature002  label="TopSilk002"
  Placement = pos=(0,0,1.62005) rot=(0,0,1;0rad)
  shape: bbox 1.676 x 2.555 x 2e-07 mm, 1 faces, 0 solids (baked)
FEATURE [Part::Feature] Part__Feature003  label="TopSilk003"
  Placement = pos=(0,0,1.62005) rot=(0,0,1;0rad)
  shape: bbox 0.3 x 1.875 x 2e-07 mm, 1 faces, 0 solids (baked)
FEATURE [Part::Feature] Part__Feature004  label="TopSilk004"
  Placement = pos=(0,0,1.62005) rot=(0,0,1;0rad)
  shape: bbox 1.349 x 1.875 x 2e-07 mm, 1 faces, 0 solids (baked)
FEATURE [Part::Feature] Part__Feature005  label="TopSilk005"
  Placement = pos=(0,0,1.62005) rot=(0,0,1;0rad)
  shape: bbox 16.25 x 30.25 x 2e-07 mm, 1 faces, 0 solids (baked)
FEATURE [Part::Feature] Part__Feature006  label="TopSilk006"
  Placement = pos=(0,0,1.62005) rot=(0,0,1;0rad)
  shape: bbox 1.649 x 0.3 x 2e-07 mm, 1 faces, 0 solids (baked)
FEATURE [Part::Feature] Part__Feature007  label="TopSilk007"
  Placement = pos=(0,0,1.62005) rot=(0,0,1;0rad)
  shape: bbox 1.499 x 1.875 x 2e-07 mm, 1 faces, 0 solids (baked)
FEATURE [Part::Feature] Part__Feature008  label="TopSilk008"
  Placement = pos=(0,0,1.62005) rot=(0,0,1;0rad)
  shape: bbox 1.425 x 1.875 x 2e-07 mm, 1 faces, 0 solids (baked)
FEATURE [Part::Feature] Part__Feature009  label="TopSilk009"
  Placement = pos=(0,0,1.62005) rot=(0,0,1;0rad)
  shape: bbox 1.126 x 1.492 x 2e-07 mm, 1 faces, 0 solids (baked)
FEATURE [Part::Feature] Part__Feature010  label="TopSilk010"
  Placement = pos=(0,0,1.62005) rot=(0,0,1;0rad)
  shape: bbox 15.25 x 21.25 x 2e-07 mm, 1 faces, 0 solids (baked)
FEATURE [Part::Feature] Part__Feature011  label="TopSilk011"
  Placement = pos=(0,0,1.62005) rot=(0,0,1;0rad)
  shape: bbox 2.154 x 15.45 x 2e-07 mm, 1 faces, 0 solids (baked)
FEATURE [Part::Feature] Part__Feature012  label="TopSilk012"
  Placement = pos=(0,0,1.62005) rot=(0,0,1;0rad)
  shape: bbox 2.286 x 2.286 x 2e-07 mm, 1 faces, 0 solids (baked)
FEATURE [Part::Feature] Part__Feature013  label="TopSilk013"
  Placement = pos=(0,0,1.62005) rot=(0,0,1;0rad)
  shape: bbox 0.6985 x 2.794 x 2e-07 mm, 1 faces, 0 solids (baked)
FEATURE [Part::Feature] Part__Feature014  label="TopSilk014"
  Placement = pos=(0,0,1.62005) rot=(0,0,1;0rad)
  shape: bbox 2.154 x 15.45 x 2e-07 mm, 1 faces, 0 solids (baked)
FEATURE [Part::Feature] Part__Feature015  label="TopSilk015"
  Placement = pos=(0,0,1.62005) rot=(0,0,1;0rad)
  shape: bbox 0.9715 x 1.129 x 2e-07 mm, 1 faces, 0 solids (baked)
FEATURE [Part::Feature] Part__Feature016  label="TopSilk016"
  Placement = pos=(0,0,1.62005) rot=(0,0,1;0rad)
  shape: bbox 1.543 x 1.129 x 2e-07 mm, 1 faces, 0 solids (baked)
FEATURE [Part::Feature] Part__Feature017  label="TopSilk017"
  Placement = pos=(0,0,1.62005) rot=(0,0,1;0rad)
  shape: bbox 1.025 x 1.492 x 2e-07 mm, 1 faces, 0 solids (baked)
FEATURE [Part::Feature] Part__Feature018  label="TopSilk018"
  Placement = pos=(0,0,1.62005) rot=(0,0,1;0rad)
  shape: bbox 1.182 x 1.492 x 2e-07 mm, 1 faces, 0 solids (baked)
FEATURE [Part::Feature] Part__Feature019  label="TopSilk019"
  Placement = pos=(0,0,1.62005) rot=(0,0,1;0rad)
  shape: bbox 0.8166 x 1.492 x 2e-07 mm, 1 faces, 0 solids (baked)
FEATURE [Part::Feature] Part__Feature020  label="TopSilk020"
  Placement = pos=(0,0,1.62005) rot=(0,0,1;0rad)
  shape: bbox 0.8166 x 1.129 x 2e-07 mm, 1 faces, 0 solids (baked)
FEATURE [Part::Feature] Part__Feature021  label="TopSilk021"
  Placement = pos=(0,0,1.62005) rot=(0,0,1;0rad)
  shape: bbox 0.1524 x 1.013 x 2e-07 mm, 1 faces, 0 solids (baked)
FEATURE [Part::Feature] Part__Feature022  label="TopSilk022"
  Placement = pos=(0,0,1.62005) rot=(0,0,1;0rad)
  shape: bbox 1.158 x 0.823 x 2e-07 mm, 1 faces, 0 solids (baked)
FEATURE [Part::Feature] Part__Feature023  label="TopSilk023"
  Placement = pos=(0,0,1.62005) rot=(0,0,1;0rad)
  shape: bbox 1.158 x 0.9195 x 2e-07 mm, 1 faces, 0 solids (baked)
FEATURE [Part::Feature] Part__Feature024  label="TopSilk024"
  Placement = pos=(0,0,1.62005) rot=(0,0,1;0rad)
  shape: bbox 1.158 x 0.1524 x 2e-07 mm, 1 faces, 0 solids (baked)
FEATURE [Part::Feature] Part__Feature025  label="TopSilk025"
  Placement = pos=(0,0,1.62005) rot=(0,0,1;0rad)
  shape: bbox 1.158 x 0.878 x 2e-07 mm, 1 faces, 0 solids (baked)
FEATURE [Part::Feature] Part__Feature026  label="TopSilk026"
  Placement = pos=(0,0,1.62005) rot=(0,0,1;0rad)
  shape: bbox 1.233 x 1.492 x 2e-07 mm, 1 faces, 0 solids (baked)
FEATURE [Part::Feature] Part__Feature027  label="TopSilk027"
  Placement = pos=(0,0,1.62005) rot=(0,0,1;0rad)
  shape: bbox 1.13 x 1.492 x 2e-07 mm, 1 faces, 0 solids (baked)
FEATURE [Part::Feature] Part__Feature028  label="TopSilk028"
  Placement = pos=(0,0,1.62005) rot=(0,0,1;0rad)
  shape: bbox 0.5041 x 0.5016 x 2e-07 mm, 1 faces, 0 solids (baked)
FEATURE [Part::Feature] Part__Feature029  label="TopSilk029"
  Placement = pos=(0,0,1.62005) rot=(0,0,1;0rad)
  shape: bbox 1.132 x 1.495 x 2e-07 mm, 1 faces, 0 solids (baked)
FEATURE [Part::Feature] Part__Feature030  label="TopSilk030"
  Placement = pos=(0,0,1.62005) rot=(0,0,1;0rad)
  shape: bbox 0.8136 x 0.5867 x 2e-07 mm, 1 faces, 0 solids (baked)
FEATURE [Part::Feature] Part__Feature031  label="TopSilk031"
  Placement = pos=(0,0,1.62005) rot=(0,0,1;0rad)
  shape: bbox 0.8026 x 0.5842 x 2e-07 mm, 1 faces, 0 solids (baked)
FEATURE [Part::Feature] Part__Feature032  label="TopSilk032"
  Placement = pos=(0,0,1.62005) rot=(0,0,1;0rad)
  shape: bbox 0.8026 x 0.7696 x 2e-07 mm, 1 faces, 0 solids (baked)
FEATURE [Part::Feature] Part__Feature033  label="TopSilk033"
  Placement = pos=(0,0,1.62005) rot=(0,0,1;0rad)
  shape: bbox 5.764 x 21.24 x 2e-07 mm, 1 faces, 0 solids (baked)
FEATURE [Part::Feature] Part__Feature034  label="TopSilk034"
  Placement = pos=(0,0,1.62005) rot=(0,0,1;0rad)
  shape: bbox 1.158 x 0.8712 x 2e-07 mm, 1 faces, 0 solids (baked)
FEATURE [Part::Feature] Part__Feature035  label="TopSilk035"
  Placement = pos=(0,0,1.62005) rot=(0,0,1;0rad)
  shape: bbox 1.158 x 0.8687 x 2e-07 mm, 1 faces, 0 solids (baked)
FEATURE [Part::Feature] Part__Feature036  label="TopSilk036"
  Placement = pos=(0,0,1.62005) rot=(0,0,1;0rad)
  shape: bbox 3.596 x 8.555 x 2e-07 mm, 1 faces, 0 solids (baked)
FEATURE [Part::Feature] Part__Feature037  label="TopSilk037"
  Placement = pos=(0,0,1.62005) rot=(0,0,1;0rad)
  shape: bbox 0.8136 x 0.5842 x 2e-07 mm, 1 faces, 0 solids (baked)
FEATURE [Part::Feature] Part__Feature038  label="TopSilk038"
  Placement = pos=(0,0,1.62005) rot=(0,0,1;0rad)
  shape: bbox 0.8045 x 0.5842 x 2e-07 mm, 1 faces, 0 solids (baked)
FEATURE [Part::Feature] Part__Feature039  label="TopSilk039"
  Placement = pos=(0,0,1.62005) rot=(0,0,1;0rad)
  shape: bbox 0.8026 x 0.5537 x 2e-07 mm, 1 faces, 0 solids (baked)
FEATURE [Part::Feature] Part__Feature040  label="TopSilk040"
  Placement = pos=(0,0,1.62005) rot=(0,0,1;0rad)
  shape: bbox 0.8026 x 0.5537 x 2e-07 mm, 1 faces, 0 solids (baked)
FEATURE [Part::Feature] Part__Feature041  label="TopSilk041"
  Placement = pos=(0,0,1.62005) rot=(0,0,1;0rad)
  shape: bbox 20.57 x 34.8 x 2e-07 mm, 1 faces, 0 solids (baked)
FEATURE [Part::Feature] Part__Feature042  label="TopSilk042"
  Placement = pos=(0,0,1.62005) rot=(0,0,1;0rad)
  shape: bbox 3.596 x 8.555 x 2e-07 mm, 1 faces, 0 solids (baked)
FEATURE [Part::Feature] Part__Feature043  label="TopSilk043"
  Placement = pos=(0,0,1.62005) rot=(0,0,1;0rad)
  shape: bbox 1.158 x 0.3912 x 2e-07 mm, 1 faces, 0 solids (baked)
FEATURE [Part::Feature] Part__Feature044  label="TopSilk044"
  Placement = pos=(0,0,1.62005) rot=(0,0,1;0rad)
  shape: bbox 1.158 x 0.8712 x 2e-07 mm, 1 faces, 0 solids (baked)
FEATURE [Part::Feature] Part__Feature045  label="TopSilk045"
  Placement = pos=(0,0,1.62005) rot=(0,0,1;0rad)
  shape: bbox 1.66 x 0.996 x 2e-07 mm, 1 faces, 0 solids (baked)
FEATURE [Part::Feature] Part__Feature046  label="TopSilk046"
  Placement = pos=(0,0,1.62005) rot=(0,0,1;0rad)
  shape: bbox 0.249 x 0.996 x 2e-07 mm, 1 faces, 0 solids (baked)
FEATURE [Part::Feature] Part__Feature047  label="TopSilk047"
  Placement = pos=(0,0,1.62005) rot=(0,0,1;0rad)
  shape: bbox 2.338 x 1.79 x 2e-07 mm, 1 faces, 0 solids (baked)
FEATURE [Part::Feature] Part__Feature048  label="TopSilk048"
  Placement = pos=(0,0,1.62005) rot=(0,0,1;0rad)
  shape: bbox 2.338 x 1.79 x 2e-07 mm, 1 faces, 0 solids (baked)
FEATURE [Part::Feature] Part__Feature049  label="TopSilk049"
  Placement = pos=(0,0,1.62005) rot=(0,0,1;0rad)
  shape: bbox 10.83 x 2.794 x 2e-07 mm, 1 faces, 0 solids (baked)
FEATURE [Part::Feature] Part__Feature050  label="TopSilk050"
  Placement = pos=(0,0,1.62005) rot=(0,0,1;0rad)
  shape: bbox 1.136 x 1.555 x 2e-07 mm, 1 faces, 0 solids (baked)
FEATURE [Part::Feature] Part__Feature051  label="TopSilk051"
  Placement = pos=(0,0,1.62005) rot=(0,0,1;0rad)
  shape: bbox 0.8704 x 1.15 x 2e-07 mm, 1 faces, 0 solids (baked)
FEATURE [Part::Feature] Part__Feature052  label="TopSilk052"
  Placement = pos=(0,0,1.62005) rot=(0,0,1;0rad)
  shape: bbox 0.823 x 1.158 x 2e-07 mm, 1 faces, 0 solids (baked)
FEATURE [Part::Feature] Part__Feature053  label="TopSilk053"
  Placement = pos=(0,0,1.62005) rot=(0,0,1;0rad)
  shape: bbox 1.095 x 1.15 x 2e-07 mm, 1 faces, 0 solids (baked)
FEATURE [Part::Feature] Part__Feature054  label="TopSilk054"
  Placement = pos=(0,0,1.62005) rot=(0,0,1;0rad)
  shape: bbox 0.7539 x 0.7539 x 2e-07 mm, 1 faces, 0 solids (baked)
FEATURE [Part::Feature] Part__Feature055  label="TopSilk055"
  Placement = pos=(0,0,1.62005) rot=(0,0,1;0rad)
  shape: bbox 0.8712 x 1.158 x 2e-07 mm, 1 faces, 0 solids (baked)
FEATURE [Part::Feature] Part__Feature056  label="TopSilk056"
  Placement = pos=(0,0,1.62005) rot=(0,0,1;0rad)
  shape: bbox 0.823 x 1.158 x 2e-07 mm, 1 faces, 0 solids (baked)
FEATURE [Part::Feature] Part__Feature057  label="TopSilk057"
  Placement = pos=(0,0,1.62005) rot=(0,0,1;0rad)
  shape: bbox 0.823 x 1.158 x 2e-07 mm, 1 faces, 0 solids (baked)
FEATURE [Part::Feature] Part__Feature058  label="TopSilk058"
  Placement = pos=(0,0,1.62005) rot=(0,0,1;0rad)
  shape: bbox 0.8704 x 1.15 x 2e-07 mm, 1 faces, 0 solids (baked)
FEATURE [Part::Feature] Part__Feature059  label="TopSilk059"
  Placement = pos=(0,0,1.62005) rot=(0,0,1;0rad)
  shape: bbox 13.65 x 12.95 x 2e-07 mm, 1 faces, 0 solids (baked)
FEATURE [Part::Feature] Part__Feature060  label="TopSilk060"
  Placement = pos=(0,0,1.62005) rot=(0,0,1;0rad)
  shape: bbox 1.095 x 1.15 x 2e-07 mm, 1 faces, 0 solids (baked)
FEATURE [Part::Feature] Part__Feature061  label="TopSilk061"
  Placement = pos=(0,0,1.62005) rot=(0,0,1;0rad)
  shape: bbox 0.878 x 1.158 x 2e-07 mm, 1 faces, 0 solids (baked)
FEATURE [Part::Feature] Part__Feature062  label="TopSilk062"
  Placement = pos=(0,0,1.62005) rot=(0,0,1;0rad)
  shape: bbox 1.197 x 1.555 x 2e-07 mm, 1 faces, 0 solids (baked)
FEATURE [Part::Feature] Part__Feature063  label="TopSilk063"
  Placement = pos=(0,0,1.62005) rot=(0,0,1;0rad)
  shape: bbox 0.823 x 1.158 x 2e-07 mm, 1 faces, 0 solids (baked)
FEATURE [Part::Feature] Part__Feature064  label="TopSilk064"
  Placement = pos=(0,0,1.62005) rot=(0,0,1;0rad)
  shape: bbox 0.823 x 1.158 x 2e-07 mm, 1 faces, 0 solids (baked)
FEATURE [Part::Feature] Part__Feature065  label="TopSilk065"
  Placement = pos=(0,0,1.62005) rot=(0,0,1;0rad)
  shape: bbox 0.7747 x 1.158 x 2e-07 mm, 1 faces, 0 solids (baked)
FEATURE [Part::Feature] Part__Feature066  label="TopSilk066"
  Placement = pos=(0,0,1.62005) rot=(0,0,1;0rad)
  shape: bbox 1.139 x 1.562 x 2e-07 mm, 1 faces, 0 solids (baked)
FEATURE [Part::Feature] Part__Feature067  label="TopSilk067"
  Placement = pos=(0,0,1.62005) rot=(0,0,1;0rad)
  shape: bbox 0.7747 x 1.158 x 2e-07 mm, 1 faces, 0 solids (baked)
FEATURE [Part::Feature] Part__Feature068  label="TopSilk068"
  Placement = pos=(0,0,1.62005) rot=(0,0,1;0rad)
  shape: bbox 0.823 x 1.158 x 2e-07 mm, 1 faces, 0 solids (baked)
FEATURE [Part::Feature] Part__Feature069  label="TopSilk069"
  Placement = pos=(0,0,1.62005) rot=(0,0,1;0rad)
  shape: bbox 1.197 x 1.555 x 2e-07 mm, 1 faces, 0 solids (baked)
FEATURE [Part::Feature] Part__Feature070  label="TopSilk070"
  Placement = pos=(0,0,1.62005) rot=(0,0,1;0rad)
  shape: bbox 0.823 x 1.158 x 2e-07 mm, 1 faces, 0 solids (baked)
FEATURE [Part::Feature] Part__Feature071  label="TopSilk071"
  Placement = pos=(0,0,1.62005) rot=(0,0,1;0rad)
  shape: bbox 0.823 x 1.158 x 2e-07 mm, 1 faces, 0 solids (baked)
FEATURE [Part::Feature] Part__Feature072  label="TopSilk072"
  Placement = pos=(0,0,1.62005) rot=(0,0,1;0rad)
  shape: bbox 2.252 x 0.2719 x 2e-07 mm, 1 faces, 0 solids (baked)
FEATURE [Part::Feature] Part__Feature073  label="TopSilk073"
  Placement = pos=(0,0,1.62005) rot=(0,0,1;0rad)
  shape: bbox 2.252 x 0.2719 x 2e-07 mm, 1 faces, 0 solids (baked)
FEATURE [Part::Feature] Part__Feature074  label="TopSilk074"
  Placement = pos=(0,0,1.62005) rot=(0,0,1;0rad)
  shape: bbox 0.5867 x 0.8026 x 2e-07 mm, 1 faces, 0 solids (baked)
FEATURE [Part::Feature] Part__Feature075  label="TopSilk075"
  Placement = pos=(0,0,1.62005) rot=(0,0,1;0rad)
  shape: bbox 0.5867 x 0.8026 x 2e-07 mm, 1 faces, 0 solids (baked)
FEATURE [Part::Feature] Part__Feature076  label="TopSilk076"
  Placement = pos=(0,0,1.62005) rot=(0,0,1;0rad)
  shape: bbox 0.7 x 0.8 x 2e-07 mm, 1 faces, 0 solids (baked)
FEATURE [Part::Feature] Part__Feature077  label="TopSilk077"
  Placement = pos=(0,0,1.62005) rot=(0,0,1;0rad)
  shape: bbox 0.5842 x 0.8026 x 2e-07 mm, 1 faces, 0 solids (baked)
FEATURE [Part::Feature] Part__Feature078  label="TopSilk078"
  Placement = pos=(0,0,1.62005) rot=(0,0,1;0rad)
  shape: bbox 4.357 x 0.8104 x 2e-07 mm, 1 faces, 0 solids (baked)
FEATURE [Part::Feature] Part__Feature079  label="TopSilk079"
  Placement = pos=(0,0,1.62005) rot=(0,0,1;0rad)
  shape: bbox 4.357 x 0.8104 x 2e-07 mm, 1 faces, 0 solids (baked)
FEATURE [Part::Feature] Part__Feature080  label="TopSilk080"
  Placement = pos=(0,0,1.62005) rot=(0,0,1;0rad)
  shape: bbox 0.6563 x 0.8026 x 2e-07 mm, 1 faces, 0 solids (baked)
FEATURE [Part::Feature] Part__Feature081  label="TopSilk081"
  Placement = pos=(0,0,1.62005) rot=(0,0,1;0rad)
  shape: bbox 1.276 x 2.074 x 2e-07 mm, 1 faces, 0 solids (baked)
FEATURE [Part::Feature] Part__Feature082  label="TopSilk082"
  Placement = pos=(0,0,1.62005) rot=(0,0,1;0rad)
  shape: bbox 0.6563 x 0.8026 x 2e-07 mm, 1 faces, 0 solids (baked)
FEATURE [Part::Feature] Part__Feature083  label="TopSilk083"
  Placement = pos=(0,0,1.62005) rot=(0,0,1;0rad)
  shape: bbox 2.054 x 2.054 x 2e-07 mm, 1 faces, 0 solids (baked)
FEATURE [Part::Feature] Part__Feature084  label="TopSilk084"
  Placement = pos=(0,0,1.62005) rot=(0,0,1;0rad)
  shape: bbox 0.5842 x 0.8026 x 2e-07 mm, 1 faces, 0 solids (baked)
FEATURE [Part::Feature] Part__Feature085  label="TopSilk085"
  Placement = pos=(0,0,1.62005) rot=(0,0,1;0rad)
  shape: bbox 1.038 x 2.074 x 2e-07 mm, 1 faces, 0 solids (baked)
FEATURE [Part::Feature] Part__Feature086  label="TopSilk086"
  Placement = pos=(0,0,1.62005) rot=(0,0,1;0rad)
  shape: bbox 20.46 x 15.85 x 2e-07 mm, 1 faces, 0 solids (baked)
FEATURE [Part::Feature] Part__Feature087  label="TopSilk087"
  Placement = pos=(0,0,1.62005) rot=(0,0,1;0rad)
  shape: bbox 0.1524 x 1.013 x 2e-07 mm, 1 faces, 0 solids (baked)
FEATURE [Part::Feature] Part__Feature088  label="TopSilk088"
  Placement = pos=(0,0,1.62005) rot=(0,0,1;0rad)
  shape: bbox 0.1524 x 1.013 x 2e-07 mm, 1 faces, 0 solids (baked)
FEATURE [Part::Feature] Part__Feature089  label="TopSilk089"
  Placement = pos=(0,0,1.62005) rot=(0,0,1;0rad)
  shape: bbox 1.038 x 2.074 x 2e-07 mm, 1 faces, 0 solids (baked)
FEATURE [Part::Feature] Part__Feature090  label="TopSilk090"
  Placement = pos=(0,0,1.62005) rot=(0,0,1;0rad)
  shape: bbox 0.5867 x 0.8026 x 2e-07 mm, 1 faces, 0 solids (baked)
FEATURE [Part::Feature] Part__Feature091  label="TopSilk091"
  Placement = pos=(0,0,1.62005) rot=(0,0,1;0rad)
  shape: bbox 0.5867 x 0.8026 x 2e-07 mm, 1 faces, 0 solids (baked)
FEATURE [Part::Feature] Part__Feature092  label="TopSilk092"
  Placement = pos=(0,0,1.62005) rot=(0,0,1;0rad)
  shape: bbox 0.254 x 1.016 x 2e-07 mm, 1 faces, 0 solids (baked)
FEATURE [Part::Feature] Part__Feature093  label="TopSilk093"
  Placement = pos=(0,0,1.62005) rot=(0,0,1;0rad)
  shape: bbox 0.3048 x 0.8026 x 2e-07 mm, 1 faces, 0 solids (baked)
FEATURE [Part::Feature] Part__Feature094  label="TopSilk094"
  Placement = pos=(0,0,1.62005) rot=(0,0,1;0rad)
  shape: bbox 1.254 x 1.254 x 2e-07 mm, 1 faces, 0 solids (baked)
FEATURE [Part::Feature] Part__Feature095  label="TopSilk095"
  Placement = pos=(0,0,1.62005) rot=(0,0,1;0rad)
  shape: bbox 1.651 x 0.2541 x 2e-07 mm, 1 faces, 0 solids (baked)
FEATURE [Part::Feature] Part__Feature096  label="TopSilk096"
  Placement = pos=(0,0,1.62005) rot=(0,0,1;0rad)
  shape: bbox 0.3048 x 0.8026 x 2e-07 mm, 1 faces, 0 solids (baked)
FEATURE [Part::Feature] Part__Feature097  label="TopSilk097"
  Placement = pos=(0,0,1.62005) rot=(0,0,1;0rad)
  shape: bbox 1.099 x 0.254 x 2e-07 mm, 1 faces, 0 solids (baked)
FEATURE [Part::Feature] Part__Feature098  label="TopSilk098"
  Placement = pos=(0,0,1.62005) rot=(0,0,1;0rad)
  shape: bbox 1.355 x 2.071 x 2e-07 mm, 1 faces, 0 solids (baked)
FEATURE [Part::Feature] Part__Feature099  label="TopSilk099"
  Placement = pos=(0,0,1.62005) rot=(0,0,1;0rad)
  shape: bbox 15.13 x 12.3 x 2e-07 mm, 1 faces, 0 solids (baked)
FEATURE [Part::Feature] Part__Feature100  label="TopSilk100"
  Placement = pos=(0,0,1.62005) rot=(0,0,1;0rad)
  shape: bbox 1.276 x 1.515 x 2e-07 mm, 1 faces, 0 solids (baked)
FEATURE [Part::Feature] Part__Feature101  label="TopSilk101"
  Placement = pos=(0,0,1.62005) rot=(0,0,1;0rad)
  shape: bbox 0.56 x 1.119 x 2e-07 mm, 1 faces, 0 solids (baked)
FEATURE [Part::Feature] Part__Feature102  label="TopSilk102"
  Placement = pos=(0,0,1.62005) rot=(0,0,1;0rad)
  shape: bbox 1.158 x 0.8712 x 2e-07 mm, 1 faces, 0 solids (baked)
FEATURE [Part::Feature] Part__Feature103  label="TopSilk103"
  Placement = pos=(0,0,1.62005) rot=(0,0,1;0rad)
  shape: bbox 1.158 x 0.823 x 2e-07 mm, 1 faces, 0 solids (baked)
FEATURE [Part::Feature] Part__Feature104  label="TopSilk104"
  Placement = pos=(0,0,1.62005) rot=(0,0,1;0rad)
  shape: bbox 3.418 x 1.587 x 2e-07 mm, 1 faces, 0 solids (baked)
FEATURE [Part::Feature] Part__Feature105  label="TopSilk105"
  Placement = pos=(0,0,1.62005) rot=(0,0,1;0rad)
  shape: bbox 3.418 x 1.587 x 2e-07 mm, 1 faces, 0 solids (baked)
FEATURE [Part::Feature] Part__Feature106  label="TopSilk106"
  Placement = pos=(0,0,1.62005) rot=(0,0,1;0rad)
  shape: bbox 1.835 x 2.948 x 2e-07 mm, 1 faces, 0 solids (baked)
FEATURE [Part::Feature] Part__Feature107  label="TopSilk107"
  Placement = pos=(0,0,1.62005) rot=(0,0,1;0rad)
  shape: bbox 2.338 x 1.79 x 2e-07 mm, 1 faces, 0 solids (baked)
FEATURE [Part::Feature] Part__Feature108  label="TopSilk108"
  Placement = pos=(0,0,1.62005) rot=(0,0,1;0rad)
  shape: bbox 2.338 x 1.79 x 2e-07 mm, 1 faces, 0 solids (baked)
FEATURE [Part::Feature] Part__Feature109  label="TopSilk109"
  Placement = pos=(0,0,1.62005) rot=(0,0,1;0rad)
  shape: bbox 0.5867 x 0.8026 x 2e-07 mm, 1 faces, 0 solids (baked)
FEATURE [Part::Feature] Part__Feature110  label="TopSilk110"
  Placement = pos=(0,0,1.62005) rot=(0,0,1;0rad)
  shape: bbox 1.474 x 1.111 x 2e-07 mm, 1 faces, 0 solids (baked)
FEATURE [Part::Feature] Part__Feature111  label="TopSilk111"
  Placement = pos=(0,0,1.62005) rot=(0,0,1;0rad)
  shape: bbox 1.474 x 1.111 x 2e-07 mm, 1 faces, 0 solids (baked)
FEATURE [Part::Feature] Part__Feature112  label="TopSilk112"
  Placement = pos=(0,0,1.62005) rot=(0,0,1;0rad)
  shape: bbox 9.326 x 1.876 x 2e-07 mm, 1 faces, 0 solids (baked)
FEATURE [Part::Feature] Part__Feature113  label="TopSilk113"
  Placement = pos=(0,0,1.62005) rot=(0,0,1;0rad)
  shape: bbox 0.254 x 2.242 x 2e-07 mm, 1 faces, 0 solids (baked)
FEATURE [Part::Feature] Part__Feature114  label="TopSilk114"
  Placement = pos=(0,0,1.62005) rot=(0,0,1;0rad)
  shape: bbox 1.835 x 2.948 x 2e-07 mm, 1 faces, 0 solids (baked)
FEATURE [Part::Feature] Part__Feature115  label="TopSilk115"
  Placement = pos=(0,0,1.62005) rot=(0,0,1;0rad)
  shape: bbox 0.8136 x 0.5842 x 2e-07 mm, 1 faces, 0 solids (baked)
FEATURE [Part::Feature] Part__Feature116  label="TopSilk116"
  Placement = pos=(0,0,1.62005) rot=(0,0,1;0rad)
  shape: bbox 0.8026 x 0.5867 x 2e-07 mm, 1 faces, 0 solids (baked)
FEATURE [Part::Feature] Part__Feature117  label="TopSilk117"
  Placement = pos=(0,0,1.62005) rot=(0,0,1;0rad)
  shape: bbox 0.5842 x 0.8136 x 2e-07 mm, 1 faces, 0 solids (baked)
FEATURE [Part::Feature] Part__Feature118  label="TopSilk118"
  Placement = pos=(0,0,1.62005) rot=(0,0,1;0rad)
  shape: bbox 0.5842 x 0.8026 x 2e-07 mm, 1 faces, 0 solids (baked)
FEATURE [Part::Feature] Part__Feature119  label="TopSilk119"
  Placement = pos=(0,0,1.62005) rot=(0,0,1;0rad)
  shape: bbox 1.158 x 0.823 x 2e-07 mm, 1 faces, 0 solids (baked)
FEATURE [Part::Feature] Part__Feature120  label="TopSilk120"
  Placement = pos=(0,0,1.62005) rot=(0,0,1;0rad)
  shape: bbox 1.158 x 0.823 x 2e-07 mm, 1 faces, 0 solids (baked)
FEATURE [Part::Feature] Part__Feature121  label="TopSilk121"
  Placement = pos=(0,0,1.62005) rot=(0,0,1;0rad)
  shape: bbox 1.474 x 1.067 x 2e-07 mm, 1 faces, 0 solids (baked)
FEATURE [Part::Feature] Part__Feature122  label="TopSilk122"
  Placement = pos=(0,0,1.62005) rot=(0,0,1;0rad)
  shape: bbox 1.474 x 1.066 x 2e-07 mm, 1 faces, 0 solids (baked)
FEATURE [Part::Feature] Part__Feature123  label="TopSilk123"
  Placement = pos=(0,0,1.62005) rot=(0,0,1;0rad)
  shape: bbox 0.5842 x 0.8026 x 2e-07 mm, 1 faces, 0 solids (baked)
FEATURE [Part::Feature] Part__Feature124  label="TopSilk124"
  Placement = pos=(0,0,1.62005) rot=(0,0,1;0rad)
  shape: bbox 0.8026 x 0.5232 x 2e-07 mm, 1 faces, 0 solids (baked)
FEATURE [Part::Feature] Part__Feature125  label="TopSilk125"
  Placement = pos=(0,0,1.62005) rot=(0,0,1;0rad)
  shape: bbox 0.8026 x 0.3048 x 2e-07 mm, 1 faces, 0 solids (baked)
FEATURE [Part::Feature] Part__Feature126  label="TopSilk126"
  Placement = pos=(0,0,1.62005) rot=(0,0,1;0rad)
  shape: bbox 1.675 x 1.515 x 2e-07 mm, 1 faces, 0 solids (baked)
FEATURE [Part::Feature] Part__Feature127  label="TopSilk127"
  Placement = pos=(0,0,1.62005) rot=(0,0,1;0rad)
  shape: bbox 1.158 x 0.3912 x 2e-07 mm, 1 faces, 0 solids (baked)
FEATURE [Part::Feature] Part__Feature128  label="TopSilk128"
  Placement = pos=(0,0,1.62005) rot=(0,0,1;0rad)
  shape: bbox 1.158 x 0.823 x 2e-07 mm, 1 faces, 0 solids (baked)
FEATURE [Part::Feature] Part__Feature129  label="TopSilk129"
  Placement = pos=(0,0,1.62005) rot=(0,0,1;0rad)
  shape: bbox 1.474 x 1.066 x 2e-07 mm, 1 faces, 0 solids (baked)
FEATURE [Part::Feature] Part__Feature130  label="TopSilk130"
  Placement = pos=(0,0,1.62005) rot=(0,0,1;0rad)
  shape: bbox 1.474 x 1.067 x 2e-07 mm, 1 faces, 0 solids (baked)
FEATURE [Part::Feature] Part__Feature131  label="TopSilk131"
  Placement = pos=(0,0,1.62005) rot=(0,0,1;0rad)
  shape: bbox 0.8026 x 0.5232 x 2e-07 mm, 1 faces, 0 solids (baked)
FEATURE [Part::Feature] Part__Feature132  label="TopSilk132"
  Placement = pos=(0,0,1.62005) rot=(0,0,1;0rad)
  shape: bbox 0.8026 x 0.5842 x 2e-07 mm, 1 faces, 0 solids (baked)
FEATURE [Part::Feature] Part__Feature133  label="TopSilk133"
  Placement = pos=(0,0,1.62005) rot=(0,0,1;0rad)
  shape: bbox 1.355 x 1.515 x 2e-07 mm, 1 faces, 0 solids (baked)
FEATURE [Part::Feature] Part__Feature134  label="TopSilk134"
  Placement = pos=(0,0,1.62005) rot=(0,0,1;0rad)
  shape: bbox 1.805 x 1.836 x 2e-07 mm, 1 faces, 0 solids (baked)
FEATURE [Part::Feature] Part__Feature135  label="TopSilk135"
  Placement = pos=(0,0,1.62005) rot=(0,0,1;0rad)
  shape: bbox 1.158 x 0.8712 x 2e-07 mm, 1 faces, 0 solids (baked)
FEATURE [Part::Feature] Part__Feature136  label="TopSilk136"
  Placement = pos=(0,0,1.62005) rot=(0,0,1;0rad)
  shape: bbox 1.158 x 0.823 x 2e-07 mm, 1 faces, 0 solids (baked)
FEATURE [Part::Feature] Part__Feature137  label="TopSilk137"
  Placement = pos=(0,0,1.62005) rot=(0,0,1;0rad)
  shape: bbox 1.474 x 1.111 x 2e-07 mm, 1 faces, 0 solids (baked)
FEATURE [Part::Feature] Part__Feature138  label="TopSilk138"
  Placement = pos=(0,0,1.62005) rot=(0,0,1;0rad)
  shape: bbox 1.474 x 1.111 x 2e-07 mm, 1 faces, 0 solids (baked)
FEATURE [Part::Feature] Part__Feature139  label="TopSilk139"
  Placement = pos=(0,0,1.62005) rot=(0,0,1;0rad)
  shape: bbox 1.038 x 2.074 x 2e-07 mm, 1 faces, 0 solids (baked)
FEATURE [Part::Feature] Part__Feature140  label="TopSilk140"
  Placement = pos=(0,0,1.62005) rot=(0,0,1;0rad)
  shape: bbox 3.596 x 8.555 x 2e-07 mm, 1 faces, 0 solids (baked)
FEATURE [Part::Feature] Part__Feature141  label="TopSilk141"
  Placement = pos=(0,0,1.62005) rot=(0,0,1;0rad)
  shape: bbox 0.8026 x 0.5867 x 2e-07 mm, 1 faces, 0 solids (baked)
FEATURE [Part::Feature] Part__Feature142  label="TopSilk142"
  Placement = pos=(0,0,1.62005) rot=(0,0,1;0rad)
  shape: bbox 0.8026 x 0.5582 x 2e-07 mm, 1 faces, 0 solids (baked)
FEATURE [Part::Feature] Part__Feature143  label="TopSilk143"
  Placement = pos=(0,0,1.62005) rot=(0,0,1;0rad)
  shape: bbox 1.355 x 1.515 x 2e-07 mm, 1 faces, 0 solids (baked)
FEATURE [Part::Feature] Part__Feature144  label="TopSilk144"
  Placement = pos=(0,0,1.62005) rot=(0,0,1;0rad)
  shape: bbox 0.254 x 2.482 x 2e-07 mm, 1 faces, 0 solids (baked)
FEATURE [Part::Feature] Part__Feature145  label="TopSilk145"
  Placement = pos=(0,0,1.62005) rot=(0,0,1;0rad)
  shape: bbox 0.3 x 4.245 x 2e-07 mm, 1 faces, 0 solids (baked)
FEATURE [Part::Feature] Part__Feature146  label="TopSilk146"
  Placement = pos=(0,0,1.62005) rot=(0,0,1;0rad)
  shape: bbox 0.254 x 2.248 x 2e-07 mm, 1 faces, 0 solids (baked)
FEATURE [Part::Feature] Part__Feature147  label="TopSilk147"
  Placement = pos=(0,0,1.62005) rot=(0,0,1;0rad)
  shape: bbox 1.038 x 1.515 x 2e-07 mm, 1 faces, 0 solids (baked)
FEATURE [Part::Feature] Part__Feature148  label="TopSilk148"
  Placement = pos=(0,0,1.62005) rot=(0,0,1;0rad)
  shape: bbox 0.8026 x 0.3048 x 2e-07 mm, 1 faces, 0 solids (baked)
FEATURE [Part::Feature] Part__Feature149  label="TopSilk149"
  Placement = pos=(0,0,1.62005) rot=(0,0,1;0rad)
  shape: bbox 0.8026 x 0.5867 x 2e-07 mm, 1 faces, 0 solids (baked)
FEATURE [Part::Feature] Part__Feature150  label="TopSilk150"
  Placement = pos=(0,0,1.62005) rot=(0,0,1;0rad)
  shape: bbox 0.8026 x 0.3048 x 2e-07 mm, 1 faces, 0 solids (baked)
FEATURE [Part::Feature] Part__Feature151  label="TopSilk151"
  Placement = pos=(0,0,1.62005) rot=(0,0,1;0rad)
  shape: bbox 3.418 x 1.587 x 2e-07 mm, 1 faces, 0 solids (baked)
FEATURE [Part::Feature] Part__Feature152  label="TopSilk152"
  Placement = pos=(0,0,1.62005) rot=(0,0,1;0rad)
  shape: bbox 3.418 x 1.587 x 2e-07 mm, 1 faces, 0 solids (baked)
FEATURE [Part::Feature] Part__Feature153  label="TopSilk153"
  Placement = pos=(0,0,1.62005) rot=(0,0,1;0rad)
  shape: bbox 0.4 x 2.074 x 2e-07 mm, 1 faces, 0 solids (baked)
FEATURE [Part::Feature] Part__Feature154  label="TopSilk154"
  Placement = pos=(0,0,1.62005) rot=(0,0,1;0rad)
  shape: bbox 3.596 x 8.555 x 2e-07 mm, 1 faces, 0 solids (baked)
FEATURE [Part::Feature] Part__Feature155  label="TopSilk155"
  Placement = pos=(0,0,1.62005) rot=(0,0,1;0rad)
  shape: bbox 1.355 x 1.515 x 2e-07 mm, 1 faces, 0 solids (baked)
FEATURE [Part::Feature] Part__Feature156  label="TopSilk156"
  Placement = pos=(0,0,1.62005) rot=(0,0,1;0rad)
  shape: bbox 1.66 x 0.996 x 2e-07 mm, 1 faces, 0 solids (baked)
FEATURE [Part::Feature] Part__Feature157  label="TopSilk157"
  Placement = pos=(0,0,1.62005) rot=(0,0,1;0rad)
  shape: bbox 0.9195 x 1.255 x 2e-07 mm, 1 faces, 0 solids (baked)
FEATURE [Part::Feature] Part__Feature158  label="TopSilk158"
  Placement = pos=(0,0,1.62005) rot=(0,0,1;0rad)
  shape: bbox 1.87 x 1.184 x 2e-07 mm, 1 faces, 0 solids (baked)
FEATURE [Part::Feature] Part__Feature159  label="TopSilk159"
  Placement = pos=(0,0,1.62005) rot=(0,0,1;0rad)
  shape: bbox 1.87 x 1.184 x 2e-07 mm, 1 faces, 0 solids (baked)
FEATURE [Part::Feature] Part__Feature160  label="TopSilk160"
  Placement = pos=(0,0,1.62005) rot=(0,0,1;0rad)
  shape: bbox 0.1524 x 1.063 x 2e-07 mm, 1 faces, 0 solids (baked)
FEATURE [Part::Feature] Part__Feature161  label="TopSilk161"
  Placement = pos=(0,0,1.62005) rot=(0,0,1;0rad)
  shape: bbox 0.249 x 0.996 x 2e-07 mm, 1 faces, 0 solids (baked)
FEATURE [Part::Feature] Part__Feature162  label="TopSilk162"
  Placement = pos=(0,0,1.62005) rot=(0,0,1;0rad)
  shape: bbox 0.6235 x 0.8026 x 2e-07 mm, 1 faces, 0 solids (baked)
FEATURE [Part::Feature] Part__Feature163  label="TopSilk163"
  Placement = pos=(0,0,1.62005) rot=(0,0,1;0rad)
  shape: bbox 1.364 x 1.674 x 2e-07 mm, 1 faces, 0 solids (baked)
FEATURE [Part::Feature] Part__Feature164  label="TopSilk164"
  Placement = pos=(0,0,1.62005) rot=(0,0,1;0rad)
  shape: bbox 0.3912 x 1.158 x 2e-07 mm, 1 faces, 0 solids (baked)
FEATURE [Part::Feature] Part__Feature165  label="TopSilk165"
  Placement = pos=(0,0,1.62005) rot=(0,0,1;0rad)
  shape: bbox 1.355 x 1.515 x 2e-07 mm, 1 faces, 0 solids (baked)
FEATURE [Part::Feature] Part__Feature166  label="TopSilk166"
  Placement = pos=(0,0,1.62005) rot=(0,0,1;0rad)
  shape: bbox 0.5583 x 0.8045 x 2e-07 mm, 1 faces, 0 solids (baked)
FEATURE [Part::Feature] Part__Feature167  label="TopSilk167"
  Placement = pos=(0,0,1.62005) rot=(0,0,1;0rad)
  shape: bbox 1.158 x 0.9195 x 2e-07 mm, 1 faces, 0 solids (baked)
FEATURE [Part::Feature] Part__Feature168  label="TopSilk168"
  Placement = pos=(0,0,1.62005) rot=(0,0,1;0rad)
  shape: bbox 1.158 x 0.878 x 2e-07 mm, 1 faces, 0 solids (baked)
FEATURE [Part::Feature] Part__Feature169  label="TopSilk169"
  Placement = pos=(0,0,1.62005) rot=(0,0,1;0rad)
  shape: bbox 1.158 x 0.9263 x 2e-07 mm, 1 faces, 0 solids (baked)
FEATURE [Part::Feature] Part__Feature170  label="TopSilk170"
  Placement = pos=(0,0,1.62005) rot=(0,0,1;0rad)
  shape: bbox 1.158 x 0.823 x 2e-07 mm, 1 faces, 0 solids (baked)
FEATURE [Part::Feature] Part__Feature171  label="TopSilk171"
  Placement = pos=(0,0,1.62005) rot=(0,0,1;0rad)
  shape: bbox 1.158 x 0.823 x 2e-07 mm, 1 faces, 0 solids (baked)
FEATURE [Part::Feature] Part__Feature172  label="TopSilk172"
  Placement = pos=(0,0,1.62005) rot=(0,0,1;0rad)
  shape: bbox 1.364 x 1.674 x 2e-07 mm, 1 faces, 0 solids (baked)
FEATURE [Part::Feature] Part__Feature173  label="TopSilk173"
  Placement = pos=(0,0,1.62005) rot=(0,0,1;0rad)
  shape: bbox 1.355 x 1.515 x 2e-07 mm, 1 faces, 0 solids (baked)
FEATURE [Part::Feature] Part__Feature174  label="TopSilk174"
  Placement = pos=(0,0,1.62005) rot=(0,0,1;0rad)
  shape: bbox 0.1524 x 1.013 x 2e-07 mm, 1 faces, 0 solids (baked)
FEATURE [Part::Feature] Part__Feature175  label="TopSilk175"
  Placement = pos=(0,0,1.62005) rot=(0,0,1;0rad)
  shape: bbox 16.25 x 30.25 x 2e-07 mm, 1 faces, 0 solids (baked)
FEATURE [Part::Feature] Part__Feature176  label="TopSilk176"
  Placement = pos=(0,0,1.62005) rot=(0,0,1;0rad)
  shape: bbox 0.4 x 2.074 x 2e-07 mm, 1 faces, 0 solids (baked)
FEATURE [Part::Feature] Part__Feature177  label="TopSilk177"
  Placement = pos=(0,0,1.62005) rot=(0,0,1;0rad)
  shape: bbox 0.5867 x 0.8026 x 2e-07 mm, 1 faces, 0 solids (baked)
FEATURE [Part::Feature] Part__Feature178  label="TopSilk178"
  Placement = pos=(0,0,1.62005) rot=(0,0,1;0rad)
  shape: bbox 1.587 x 3.418 x 2e-07 mm, 1 faces, 0 solids (baked)
FEATURE [Part::Feature] Part__Feature179  label="TopSilk179"
  Placement = pos=(0,0,1.62005) rot=(0,0,1;0rad)
  shape: bbox 0.56 x 0.56 x 2e-07 mm, 1 faces, 0 solids (baked)
FEATURE [Part::Feature] Part__Feature180  label="TopSilk180"
  Placement = pos=(0,0,1.62005) rot=(0,0,1;0rad)
  shape: bbox 1.158 x 0.823 x 2e-07 mm, 1 faces, 0 solids (baked)
FEATURE [Part::Feature] Part__Feature181  label="TopSilk181"
  Placement = pos=(0,0,1.62005) rot=(0,0,1;0rad)
  shape: bbox 1.158 x 0.823 x 2e-07 mm, 1 faces, 0 solids (baked)
FEATURE [Part::Feature] Part__Feature182  label="TopSilk182"
  Placement = pos=(0,0,1.62005) rot=(0,0,1;0rad)
  shape: bbox 1.158 x 0.823 x 2e-07 mm, 1 faces, 0 solids (baked)
FEATURE [Part::Feature] Part__Feature183  label="TopSilk183"
  Placement = pos=(0,0,1.62005) rot=(0,0,1;0rad)
  shape: bbox 0.4994 x 0.254 x 2e-07 mm, 1 faces, 0 solids (baked)
FEATURE [Part::Feature] Part__Feature184  label="TopSilk184"
  Placement = pos=(0,0,1.62005) rot=(0,0,1;0rad)
  shape: bbox 0.4994 x 0.254 x 2e-07 mm, 1 faces, 0 solids (baked)
FEATURE [Part::Feature] Part__Feature185  label="TopSilk185"
  Placement = pos=(0,0,1.62005) rot=(0,0,1;0rad)
  shape: bbox 0.3048 x 0.8026 x 2e-07 mm, 1 faces, 0 solids (baked)
FEATURE [Part::Feature] Part__Feature186  label="TopSilk186"
  Placement = pos=(0,0,1.62005) rot=(0,0,1;0rad)
  shape: bbox 0.5877 x 0.8063 x 2e-07 mm, 1 faces, 0 solids (baked)
FEATURE [Part::Feature] Part__Feature187  label="TopSilk187"
  Placement = pos=(0,0,1.62005) rot=(0,0,1;0rad)
  shape: bbox 1.355 x 2.071 x 2e-07 mm, 1 faces, 0 solids (baked)
FEATURE [Part::Feature] Part__Feature188  label="TopSilk188"
  Placement = pos=(0,0,1.62005) rot=(0,0,1;0rad)
  shape: bbox 0.5867 x 0.8026 x 2e-07 mm, 1 faces, 0 solids (baked)
FEATURE [Part::Feature] Part__Feature189  label="TopSilk189"
  Placement = pos=(0,0,1.62005) rot=(0,0,1;0rad)
  shape: bbox 1.5 x 1.65 x 2e-07 mm, 1 faces, 0 solids (baked)
FEATURE [Part::Feature] Part__Feature190  label="TopSilk190"
  Placement = pos=(0,0,1.62005) rot=(0,0,1;0rad)
  shape: bbox 1.5 x 1.65 x 2e-07 mm, 1 faces, 0 solids (baked)
FEATURE [Part::Feature] Part__Feature191  label="TopSilk191"
  Placement = pos=(0,0,1.62005) rot=(0,0,1;0rad)
  shape: bbox 0.5867 x 0.8136 x 2e-07 mm, 1 faces, 0 solids (baked)
FEATURE [Part::Feature] Part__Feature192  label="TopSilk192"
  Placement = pos=(0,0,1.62005) rot=(0,0,1;0rad)
  shape: bbox 0.7696 x 0.8026 x 2e-07 mm, 1 faces, 0 solids (baked)
FEATURE [Part::Feature] Part__Feature193  label="TopSilk193"
  Placement = pos=(0,0,1.62005) rot=(0,0,1;0rad)
  shape: bbox 0.7696 x 0.8026 x 2e-07 mm, 1 faces, 0 solids (baked)
FEATURE [Part::Feature] Part__Feature194  label="TopSilk194"
  Placement = pos=(0,0,1.62005) rot=(0,0,1;0rad)
  shape: bbox 0.1999 x 0.8 x 2e-07 mm, 1 faces, 0 solids (baked)
FEATURE [Part::Feature] Part__Feature195  label="TopSilk195"
  Placement = pos=(0,0,1.62005) rot=(0,0,1;0rad)
  shape: bbox 0.49 x 0.83 x 2e-07 mm, 1 faces, 0 solids (baked)
FEATURE [Part::Feature] Part__Feature196  label="TopSilk196"
  Placement = pos=(0,0,1.62005) rot=(0,0,1;0rad)
  shape: bbox 1.038 x 1.515 x 2e-07 mm, 1 faces, 0 solids (baked)
FEATURE [Part::Feature] Part__Feature197  label="TopSilk197"
  Placement = pos=(0,0,1.62005) rot=(0,0,1;0rad)
  shape: bbox 0.5842 x 0.8026 x 2e-07 mm, 1 faces, 0 solids (baked)
FEATURE [Part::Feature] Part__Feature198  label="TopSilk198"
  Placement = pos=(0,0,1.62005) rot=(0,0,1;0rad)
  shape: bbox 3.746 x 7.854 x 2e-07 mm, 1 faces, 0 solids (baked)
FEATURE [Part::Feature] Part__Feature199  label="TopSilk199"
  Placement = pos=(0,0,1.62005) rot=(0,0,1;0rad)
  shape: bbox 1.587 x 3.418 x 2e-07 mm, 1 faces, 0 solids (baked)
FEATURE [Part::Feature] Part__Feature200  label="TopSilk200"
  Placement = pos=(0,0,1.62005) rot=(0,0,1;0rad)
  shape: bbox 1.3 x 1.65 x 2e-07 mm, 1 faces, 0 solids (baked)
FEATURE [Part::Feature] Part__Feature201  label="TopSilk201"
  Placement = pos=(0,0,1.62005) rot=(0,0,1;0rad)
  shape: bbox 1.3 x 1.65 x 2e-07 mm, 1 faces, 0 solids (baked)
FEATURE [Part::Feature] Part__Feature202  label="TopSilk202"
  Placement = pos=(0,0,1.62005) rot=(0,0,1;0rad)
  shape: bbox 1.436 x 1.515 x 2e-07 mm, 1 faces, 0 solids (baked)
FEATURE [Part::Feature] Part__Feature203  label="TopSilk203"
  Placement = pos=(0,0,1.62005) rot=(0,0,1;0rad)
  shape: bbox 1.499 x 1.875 x 2e-07 mm, 1 faces, 0 solids (baked)
FEATURE [Part::Feature] Part__Feature204  label="TopSilk204"
  Placement = pos=(0,0,1.62005) rot=(0,0,1;0rad)
  shape: bbox 1.425 x 1.875 x 2e-07 mm, 1 faces, 0 solids (baked)
FEATURE [Part::Feature] Part__Feature205  label="TopSilk205"
  Placement = pos=(0,0,1.62005) rot=(0,0,1;0rad)
  shape: bbox 1.649 x 0.3 x 2e-07 mm, 1 faces, 0 solids (baked)
FEATURE [Part::Feature] Part__Feature206  label="TopSilk206"
  Placement = pos=(0,0,1.62005) rot=(0,0,1;0rad)
  shape: bbox 1.499 x 1.875 x 2e-07 mm, 1 faces, 0 solids (baked)
FEATURE [Part::Feature] Part__Feature207  label="TopSilk207"
  Placement = pos=(0,0,1.62005) rot=(0,0,1;0rad)
  shape: bbox 1.349 x 1.879 x 2e-07 mm, 1 faces, 0 solids (baked)
FEATURE [Part::Feature] Part__Feature208  label="TopSilk208"
  Placement = pos=(0,0,1.62005) rot=(0,0,1;0rad)
  shape: bbox 1.968 x 2.555 x 2e-07 mm, 1 faces, 0 solids (baked)
FEATURE [Part::Feature] Part__Feature209  label="TopSilk209"
  Placement = pos=(0,0,1.62005) rot=(0,0,1;0rad)
  shape: bbox 1.872 x 2.555 x 2e-07 mm, 1 faces, 0 solids (baked)
FEATURE [Part::Feature] Part__Feature210  label="TopSilk210"
  Placement = pos=(0,0,1.62005) rot=(0,0,1;0rad)
  shape: bbox 1.676 x 2.555 x 2e-07 mm, 1 faces, 0 solids (baked)
FEATURE [Part::Feature] Part__Feature211  label="TopSilk211"
  Placement = pos=(0,0,1.62005) rot=(0,0,1;0rad)
  shape: bbox 1.349 x 1.875 x 2e-07 mm, 1 faces, 0 solids (baked)
FEATURE [App::Part] TopSilk  label="TopSilk212"
  Group = -> [Part__Feature,Part__Feature001,Part__Feature002,Part__Feature003,Part__Feature004,Part__Feature005,Part__Feature006,Part__Feature007,Part__Feature008,Part__Feature009,Part__Feature010,Part__Feature011,Part__Feature012,Part__Feature013,Part__Feature014,Part__Feature015,Part__Feature016,Part__Feature017,Part__Feature018,Part__Feature019,Part__Feature020,Part__Feature021,Part__Feature022,+189 more]
  Origin = -> Origin
FEATURE [Part::Feature] Part__Feature212  label="BottomSilk"
  Placement = pos=(0,0,-0.02) rot=(0,0,1;0rad)
  shape: bbox 2.625 x 0.8753 x 2e-07 mm, 1 faces, 0 solids (baked)
FEATURE [Part::Feature] Part__Feature213  label="BottomSilk001"
  Placement = pos=(0,0,-0.02) rot=(0,0,1;0rad)
  shape: bbox 2.625 x 0.8753 x 2e-07 mm, 1 faces, 0 solids (baked)
FEATURE [Part::Feature] Part__Feature214  label="BottomSilk002"
  Placement = pos=(0,0,-0.02) rot=(0,0,1;0rad)
  shape: bbox 2.536 x 1.401 x 2e-07 mm, 1 faces, 0 solids (baked)
FEATURE [Part::Feature] Part__Feature215  label="BottomSilk003"
  Placement = pos=(0,0,-0.02) rot=(0,0,1;0rad)
  shape: bbox 2.536 x 1.924 x 2e-07 mm, 1 faces, 0 solids (baked)
FEATURE [Part::Feature] Part__Feature216  label="BottomSilk004"
  Placement = pos=(0,0,-0.02) rot=(0,0,1;0rad)
  shape: bbox 2.536 x 1.838 x 2e-07 mm, 1 faces, 0 solids (baked)
FEATURE [Part::Feature] Part__Feature217  label="BottomSilk005"
  Placement = pos=(0,0,-0.02) rot=(0,0,1;0rad)
  shape: bbox 2.536 x 1.401 x 2e-07 mm, 1 faces, 0 solids (baked)
FEATURE [Part::Feature] Part__Feature218  label="BottomSilk006"
  Placement = pos=(0,0,-0.02) rot=(0,0,1;0rad)
  shape: bbox 2.536 x 2.45 x 2e-07 mm, 1 faces, 0 solids (baked)
FEATURE [Part::Feature] Part__Feature219  label="BottomSilk007"
  Placement = pos=(0,0,-0.02) rot=(0,0,1;0rad)
  shape: bbox 2.536 x 2.45 x 2e-07 mm, 1 faces, 0 solids (baked)
FEATURE [Part::Feature] Part__Feature220  label="BottomSilk008"
  Placement = pos=(0,0,-0.02) rot=(0,0,1;0rad)
  shape: bbox 2.536 x 1.137 x 2e-07 mm, 1 faces, 0 solids (baked)
FEATURE [Part::Feature] Part__Feature221  label="BottomSilk009"
  Placement = pos=(0,0,-0.02) rot=(0,0,1;0rad)
  shape: bbox 2.536 x 1.924 x 2e-07 mm, 1 faces, 0 solids (baked)
FEATURE [Part::Feature] Part__Feature222  label="BottomSilk010"
  Placement = pos=(0,0,-0.02) rot=(0,0,1;0rad)
  shape: bbox 2.536 x 2.011 x 2e-07 mm, 1 faces, 0 solids (baked)
FEATURE [Part::Feature] Part__Feature223  label="BottomSilk011"
  Placement = pos=(0,0,-0.02) rot=(0,0,1;0rad)
  shape: bbox 2.536 x 1.924 x 2e-07 mm, 1 faces, 0 solids (baked)
FEATURE [Part::Feature] Part__Feature224  label="BottomSilk012"
  Placement = pos=(0,0,-0.02) rot=(0,0,1;0rad)
  shape: bbox 2.536 x 1.401 x 2e-07 mm, 1 faces, 0 solids (baked)
FEATURE [Part::Feature] Part__Feature225  label="BottomSilk013"
  Placement = pos=(0,0,-0.02) rot=(0,0,1;0rad)
  shape: bbox 2.536 x 0.7 x 2e-07 mm, 1 faces, 0 solids (baked)
FEATURE [Part::Feature] Part__Feature226  label="BottomSilk014"
  Placement = pos=(0,0,-0.02) rot=(0,0,1;0rad)
  shape: bbox 2.536 x 0.7 x 2e-07 mm, 1 faces, 0 solids (baked)
FEATURE [Part::Feature] Part__Feature227  label="BottomSilk015"
  Placement = pos=(0,0,-0.02) rot=(0,0,1;0rad)
  shape: bbox 1.924 x 1.401 x 2e-07 mm, 1 faces, 0 solids (baked)
FEATURE [Part::Feature] Part__Feature228  label="BottomSilk016"
  Placement = pos=(0,0,-0.02) rot=(0,0,1;0rad)
  shape: bbox 1.924 x 1.749 x 2e-07 mm, 1 faces, 0 solids (baked)
FEATURE [Part::Feature] Part__Feature229  label="BottomSilk017"
  Placement = pos=(0,0,-0.02) rot=(0,0,1;0rad)
  shape: bbox 1.924 x 1.663 x 2e-07 mm, 1 faces, 0 solids (baked)
FEATURE [Part::Feature] Part__Feature230  label="BottomSilk018"
  Placement = pos=(0,0,-0.02) rot=(0,0,1;0rad)
  shape: bbox 1.924 x 2.625 x 2e-07 mm, 1 faces, 0 solids (baked)
FEATURE [Part::Feature] Part__Feature231  label="BottomSilk019"
  Placement = pos=(0,0,-0.02) rot=(0,0,1;0rad)
  shape: bbox 1.924 x 1.749 x 2e-07 mm, 1 faces, 0 solids (baked)
FEATURE [Part::Feature] Part__Feature232  label="BottomSilk020"
  Placement = pos=(0,0,-0.02) rot=(0,0,1;0rad)
  shape: bbox 1.924 x 2.625 x 2e-07 mm, 1 faces, 0 solids (baked)
FEATURE [Part::Feature] Part__Feature233  label="BottomSilk021"
  Placement = pos=(0,0,-0.02) rot=(0,0,1;0rad)
  shape: bbox 1.924 x 1.401 x 2e-07 mm, 1 faces, 0 solids (baked)
FEATURE [Part::Feature] Part__Feature234  label="BottomSilk022"
  Placement = pos=(0,0,-0.02) rot=(0,0,1;0rad)
  shape: bbox 1.924 x 1.401 x 2e-07 mm, 1 faces, 0 solids (baked)
FEATURE [Part::Feature] Part__Feature235  label="BottomSilk023"
  Placement = pos=(0,0,-0.02) rot=(0,0,1;0rad)
  shape: bbox 1.924 x 1.838 x 2e-07 mm, 1 faces, 0 solids (baked)
FEATURE [Part::Feature] Part__Feature236  label="BottomSilk024"
  Placement = pos=(0,0,-0.02) rot=(0,0,1;0rad)
  shape: bbox 1.924 x 1.749 x 2e-07 mm, 1 faces, 0 solids (baked)
FEATURE [Part::Feature] Part__Feature237  label="BottomSilk025"
  Placement = pos=(0,0,-0.02) rot=(0,0,1;0rad)
  shape: bbox 2.536 x 1.749 x 2e-07 mm, 1 faces, 0 solids (baked)
FEATURE [Part::Feature] Part__Feature238  label="BottomSilk026"
  Placement = pos=(0,0,-0.02) rot=(0,0,1;0rad)
  shape: bbox 1.924 x 1.663 x 2e-07 mm, 1 faces, 0 solids (baked)
FEATURE [Part::Feature] Part__Feature239  label="BottomSilk027"
  Placement = pos=(0,0,-0.02) rot=(0,0,1;0rad)
  shape: bbox 1.924 x 1.838 x 2e-07 mm, 1 faces, 0 solids (baked)
FEATURE [Part::Feature] Part__Feature240  label="BottomSilk028"
  Placement = pos=(0,0,-0.02) rot=(0,0,1;0rad)
  shape: bbox 1.924 x 1.401 x 2e-07 mm, 1 faces, 0 solids (baked)
FEATURE [Part::Feature] Part__Feature241  label="BottomSilk029"
  Placement = pos=(0,0,-0.02) rot=(0,0,1;0rad)
  shape: bbox 1.924 x 1.749 x 2e-07 mm, 1 faces, 0 solids (baked)
FEATURE [Part::Feature] Part__Feature242  label="BottomSilk030"
  Placement = pos=(0,0,-0.02) rot=(0,0,1;0rad)
  shape: bbox 25 x 35 x 2e-07 mm, 1 faces, 0 solids (baked)
FEATURE [Part::Feature] Part__Feature243  label="BottomSilk031"
  Placement = pos=(0,0,-0.02) rot=(0,0,1;0rad)
  shape: bbox 2.211 x 2.606 x 2e-07 mm, 1 faces, 0 solids (baked)
FEATURE [Part::Feature] Part__Feature244  label="BottomSilk032"
  Placement = pos=(0,0,-0.02) rot=(0,0,1;0rad)
  shape: bbox 17.31 x 17.91 x 2e-07 mm, 1 faces, 0 solids (baked)
FEATURE [Part::Feature] Part__Feature245  label="BottomSilk033"
  Placement = pos=(0,0,-0.02) rot=(0,0,1;0rad)
  shape: bbox 1.37 x 2.502 x 2e-07 mm, 1 faces, 0 solids (baked)
FEATURE [Part::Feature] Part__Feature246  label="BottomSilk034"
  Placement = pos=(0,0,-0.02) rot=(0,0,1;0rad)
  shape: bbox 2.158 x 2.606 x 2e-07 mm, 1 faces, 0 solids (baked)
FEATURE [Part::Feature] Part__Feature247  label="BottomSilk035"
  Placement = pos=(0,0,-0.02) rot=(0,0,1;0rad)
  shape: bbox 2.139 x 2.537 x 2e-07 mm, 1 faces, 0 solids (baked)
FEATURE [Part::Feature] Part__Feature248  label="BottomSilk036"
  Placement = pos=(0,0,-0.02) rot=(0,0,1;0rad)
  shape: bbox 3.297 x 2.486 x 2e-07 mm, 1 faces, 0 solids (baked)
FEATURE [Part::Feature] Part__Feature249  label="BottomSilk037"
  Placement = pos=(0,0,-0.02) rot=(0,0,1;0rad)
  shape: bbox 2.206 x 2.64 x 2e-07 mm, 1 faces, 0 solids (baked)
FEATURE [Part::Feature] Part__Feature250  label="BottomSilk038"
  Placement = pos=(0,0,-0.02) rot=(0,0,1;0rad)
  shape: bbox 2.261 x 3.531 x 2e-07 mm, 1 faces, 0 solids (baked)
FEATURE [Part::Feature] Part__Feature251  label="BottomSilk039"
  Placement = pos=(0,0,-0.02) rot=(0,0,1;0rad)
  shape: bbox 2.258 x 3.43 x 2e-07 mm, 1 faces, 0 solids (baked)
FEATURE [Part::Feature] Part__Feature252  label="BottomSilk040"
  Placement = pos=(0,0,-0.02) rot=(0,0,1;0rad)
  shape: bbox 3.073 x 3.514 x 2e-07 mm, 1 faces, 0 solids (baked)
FEATURE [Part::Feature] Part__Feature253  label="BottomSilk041"
  Placement = pos=(0,0,-0.02) rot=(0,0,1;0rad)
  shape: bbox 1.37 x 2.502 x 2e-07 mm, 1 faces, 0 solids (baked)
FEATURE [Part::Feature] Part__Feature254  label="BottomSilk042"
  Placement = pos=(0,0,-0.02) rot=(0,0,1;0rad)
  shape: bbox 2.175 x 2.607 x 2e-07 mm, 1 faces, 0 solids (baked)
FEATURE [Part::Feature] Part__Feature255  label="BottomSilk043"
  Placement = pos=(0,0,-0.02) rot=(0,0,1;0rad)
  shape: bbox 2.574 x 3.334 x 2e-07 mm, 1 faces, 0 solids (baked)
FEATURE [Part::Feature] Part__Feature256  label="BottomSilk044"
  Placement = pos=(0,0,-0.02) rot=(0,0,1;0rad)
  shape: bbox 3.413 x 1.866 x 2e-07 mm, 1 faces, 0 solids (baked)
FEATURE [Part::Feature] Part__Feature257  label="BottomSilk045"
  Placement = pos=(0,0,-0.02) rot=(0,0,1;0rad)
  shape: bbox 33.69 x 11.68 x 2e-07 mm, 1 faces, 0 solids (baked)
FEATURE [Part::Feature] Part__Feature258  label="BottomSilk046"
  Placement = pos=(0,0,-0.02) rot=(0,0,1;0rad)
  shape: bbox 3.334 x 2.732 x 2e-07 mm, 1 faces, 0 solids (baked)
FEATURE [Part::Feature] Part__Feature259  label="BottomSilk047"
  Placement = pos=(0,0,-0.02) rot=(0,0,1;0rad)
  shape: bbox 2.176 x 1.861 x 2e-07 mm, 1 faces, 0 solids (baked)
FEATURE [Part::Feature] Part__Feature260  label="BottomSilk048"
  Placement = pos=(0,0,-0.02) rot=(0,0,1;0rad)
  shape: bbox 2.525 x 2.654 x 2e-07 mm, 1 faces, 0 solids (baked)
FEATURE [Part::Feature] Part__Feature261  label="BottomSilk049"
  Placement = pos=(0,0,-0.02) rot=(0,0,1;0rad)
  shape: bbox 1.982 x 1.856 x 2e-07 mm, 1 faces, 0 solids (baked)
FEATURE [Part::Feature] Part__Feature262  label="BottomSilk050"
  Placement = pos=(0,0,-0.02) rot=(0,0,1;0rad)
  shape: bbox 1.99 x 1.864 x 2e-07 mm, 1 faces, 0 solids (baked)
FEATURE [Part::Feature] Part__Feature263  label="BottomSilk051"
  Placement = pos=(0,0,-0.02) rot=(0,0,1;0rad)
  shape: bbox 1.745 x 1.861 x 2e-07 mm, 1 faces, 0 solids (baked)
FEATURE [Part::Feature] Part__Feature264  label="BottomSilk052"
  Placement = pos=(0,0,-0.02) rot=(0,0,1;0rad)
  shape: bbox 2.388 x 2.581 x 2e-07 mm, 1 faces, 0 solids (baked)
FEATURE [Part::Feature] Part__Feature265  label="BottomSilk053"
  Placement = pos=(0,0,-0.02) rot=(0,0,1;0rad)
  shape: bbox 2.242 x 1.811 x 2e-07 mm, 1 faces, 0 solids (baked)
FEATURE [Part::Feature] Part__Feature266  label="BottomSilk054"
  Placement = pos=(0,0,-0.02) rot=(0,0,1;0rad)
  shape: bbox 0.6978 x 0.6485 x 2e-07 mm, 1 faces, 0 solids (baked)
FEATURE [Part::Feature] Part__Feature267  label="BottomSilk055"
  Placement = pos=(0,0,-0.02) rot=(0,0,1;0rad)
  shape: bbox 1.109 x 1.791 x 2e-07 mm, 1 faces, 0 solids (baked)
FEATURE [Part::Feature] Part__Feature268  label="BottomSilk056"
  Placement = pos=(0,0,-0.02) rot=(0,0,1;0rad)
  shape: bbox 1.812 x 1.861 x 2e-07 mm, 1 faces, 0 solids (baked)
FEATURE [Part::Feature] Part__Feature269  label="BottomSilk057"
  Placement = pos=(0,0,-0.02) rot=(0,0,1;0rad)
  shape: bbox 2.267 x 1.862 x 2e-07 mm, 1 faces, 0 solids (baked)
FEATURE [Part::Feature] Part__Feature270  label="BottomSilk058"
  Placement = pos=(0,0,-0.02) rot=(0,0,1;0rad)
  shape: bbox 1.986 x 1.857 x 2e-07 mm, 1 faces, 0 solids (baked)
FEATURE [Part::Feature] Part__Feature271  label="BottomSilk059"
  Placement = pos=(0,0,-0.02) rot=(0,0,1;0rad)
  shape: bbox 1.998 x 1.863 x 2e-07 mm, 1 faces, 0 solids (baked)
FEATURE [Part::Feature] Part__Feature272  label="BottomSilk060"
  Placement = pos=(0,0,-0.02) rot=(0,0,1;0rad)
  shape: bbox 1.745 x 1.862 x 2e-07 mm, 1 faces, 0 solids (baked)
FEATURE [Part::Feature] Part__Feature273  label="BottomSilk061"
  Placement = pos=(0,0,-0.02) rot=(0,0,1;0rad)
  shape: bbox 2.394 x 2.58 x 2e-07 mm, 1 faces, 0 solids (baked)
FEATURE [App::Part] BottomSilk  label="BottomSilk062"
  Group = -> [Part__Feature212,Part__Feature213,Part__Feature214,Part__Feature215,Part__Feature216,Part__Feature217,Part__Feature218,Part__Feature219,Part__Feature220,Part__Feature221,Part__Feature222,Part__Feature223,Part__Feature224,Part__Feature225,Part__Feature226,Part__Feature227,Part__Feature228,Part__Feature229,Part__Feature230,Part__Feature231,Part__Feature232,Part__Feature233,Part__Feature234,+39 more]
  Origin = -> Origin052
FEATURE [Part::Feature] Part__Feature274  label="Board"
  shape: bbox 101.2 x 80.02 x 1.6 mm, 116 faces (baked)
FEATURE [Part::Feature] Part__Feature275  label="C1206"
  shape: bbox 0.762 x 0.762 x 0.762 mm, 6 faces (baked)
FEATURE [App::Part] pRkl_C1  label="pRkl-C1"
  Group = -> [Part__Feature275]
  Origin = -> Origin053
  Placement = pos=(41.4021,36.4491,1.60005) rot=(0,0,1;1.5708rad)
FEATURE [Part::Feature] Part__Feature276  label="C1207"
  shape: bbox 0.762 x 0.762 x 0.762 mm, 6 faces (baked)
FEATURE [App::Part] pRkl_C3  label="pRkl-C3"
  Group = -> [Part__Feature276]
  Origin = -> Origin054
  Placement = pos=(66.1671,49.5301,1.60005) rot=(0,0,1;1.5708rad)
FEATURE [Part::Feature] Part__Feature277  label="C0402"
  shape: bbox 0.762 x 0.762 x 0.762 mm, 6 faces (baked)
FEATURE [App::Part] pRkl_C5  label="pRkl-C5"
  Group = -> [Part__Feature277]
  Origin = -> Origin055
  Placement = pos=(45.8471,27.5591,1.60005) rot=(0,0,1;0rad)
FEATURE [Part::Feature] Part__Feature278  label="COMPOUND"
  shape: bbox 1.601 x 2.901 x 1.1 mm, 207 faces (baked)
FEATURE [Part::Feature] Part__Feature279  label="COMPOUND001"
  shape: bbox 0.6046 x 0.4 x 0.7911 mm, 51 faces (baked)
FEATURE [Part::Feature] Part__Feature280  label="COMPOUND002"
  shape: bbox 0.6046 x 0.4 x 0.7911 mm, 51 faces (baked)
FEATURE [Part::Feature] Part__Feature281  label="COMPOUND003"
  shape: bbox 0.6046 x 0.4 x 0.7911 mm, 51 faces (baked)
FEATURE [Part::Feature] Part__Feature282  label="COMPOUND004"
  shape: bbox 0.06101 x 0.03218 x 0.001 mm, 8 faces (baked)
FEATURE [Part::Feature] Part__Feature283  label="COMPOUND005"
  shape: bbox 0.06307 x 0.04568 x 0.001 mm, 16 faces (baked)
FEATURE [Part::Feature] Part__Feature284  label="COMPOUND006"
  shape: bbox 0.06101 x 0.03281 x 0.001 mm, 14 faces (baked)
FEATURE [Part::Feature] Part__Feature285  label="COMPOUND007"
  shape: bbox 0.06101 x 0.04967 x 0.001 mm, 16 faces (baked)
FEATURE [Part::Feature] Part__Feature286  label="COMPOUND008"
  shape: bbox 0.06101 x 0.0549 x 0.001 mm, 16 faces (baked)
FEATURE [Part::Feature] Part__Feature287  label="COMPOUND009"
  shape: bbox 0.06101 x 0.03281 x 0.001 mm, 14 faces (baked)
FEATURE [Part::Feature] Part__Feature288  label="COMPOUND010"
  shape: bbox 0.0456 x 0.03501 x 0.001 mm, 24 faces (baked)
FEATURE [Part::Feature] Part__Feature289  label="COMPOUND011"
  shape: bbox 0.0456 x 0.02943 x 0.001 mm, 23 faces (baked)
FEATURE [Part::Feature] Part__Feature290  label="COMPOUND012"
  shape: bbox 0.0641 x 0.04183 x 0.001 mm, 17 faces (baked)
FEATURE [Part::Feature] Part__Feature291  label="COMPOUND013"
  shape: bbox 0.06101 x 0.03281 x 0.001 mm, 14 faces (baked)
FEATURE [Part::Feature] Part__Feature292  label="COMPOUND014"
  shape: bbox 0.06101 x 0.04967 x 0.001 mm, 16 faces (baked)
FEATURE [Part::Feature] Part__Feature293  label="COMPOUND015"
  shape: bbox 0.06101 x 0.0549 x 0.001 mm, 16 faces (baked)
FEATURE [Part::Feature] Part__Feature294  label="COMPOUND016"
  shape: bbox 0.203 x 0.2768 x 0.001 mm, 37 faces (baked)
FEATURE [App::Part] COMPOUND  label="COMPOUND017"
  Group = -> [Part__Feature278,Part__Feature279,Part__Feature280,Part__Feature281,Part__Feature282,Part__Feature283,Part__Feature284,Part__Feature285,Part__Feature286,Part__Feature287,Part__Feature288,Part__Feature289,Part__Feature290,Part__Feature291,Part__Feature292,Part__Feature293,Part__Feature294]
  Origin = -> Origin056
FEATURE [App::Part] SOT_23_3_L3_0_W1_7_P0_95_LS2_9_BR  label="SOT-23-3_L3.0-W1.7-P0.95-LS2.9-BR"
  Group = -> [COMPOUND]
  Origin = -> Origin057
FEATURE [App::Part] pRkl_Q1  label="pRkl-Q1"
  Group = -> [SOT_23_3_L3_0_W1_7_P0_95_LS2_9_BR]
  Origin = -> Origin058
  Placement = pos=(79.6292,30.7341,1.60005) rot=(0,0,1;3.14159rad)
FEATURE [Part::Feature] Part__Feature295  label="SOLID"
  shape: bbox 3.1 x 2.601 x 0.55 mm, 250 faces (baked)
FEATURE [App::Part] R1210
  Group = -> [Part__Feature295]
  Origin = -> Origin059
FEATURE [App::Part] pRkl_R10  label="pRkl-R10"
  Group = -> [R1210]
  Origin = -> Origin060
  Placement = pos=(85.8941,49.6463,1.60005) rot=(0,0,1;0rad)
FEATURE [Part::Feature] Part__Feature296  label="SOLID001"
  shape: bbox 3.1 x 2.601 x 0.55 mm, 250 faces (baked)
FEATURE [App::Part] R1211
  Group = -> [Part__Feature296]
  Origin = -> Origin061
FEATURE [App::Part] pRkl_R11  label="pRkl-R11"
  Group = -> [R1211]
  Origin = -> Origin062
  Placement = pos=(78.4605,37.4543,1.60005) rot=(0,0,1;1.5708rad)
FEATURE [Part::Feature] Part__Feature297  label="SOLID002"
  shape: bbox 3.1 x 2.601 x 0.55 mm, 250 faces (baked)
FEATURE [App::Part] R1212
  Group = -> [Part__Feature297]
  Origin = -> Origin063
FEATURE [App::Part] pRkl_R2  label="pRkl-R2"
  Group = -> [R1212]
  Origin = -> Origin064
  Placement = pos=(65.6591,35.1791,1.60005) rot=(0,0,-1;1.5708rad)
FEATURE [Part::Feature] Part__Feature298  label="R0402"
  shape: bbox 0.762 x 0.762 x 0.762 mm, 6 faces (baked)
FEATURE [App::Part] pRkl_R3  label="pRkl-R3"
  Group = -> [Part__Feature298]
  Origin = -> Origin065
  Placement = pos=(45.3391,31.7501,1.60005) rot=(0,0,1;0rad)
FEATURE [Part::Feature] Part__Feature299  label="SOLID003"
  shape: bbox 34.54 x 20.32 x 27.51 mm, 472 faces (baked)
FEATURE [App::Part] PWRM_TH_HLK_PM03  label="PWRM-TH_HLK-PM03"
  Group = -> [Part__Feature299]
  Origin = -> Origin066
FEATURE [App::Part] pRkl_AC_DC_CONV  label="pRkl-AC-DC-CONV"
  Group = -> [PWRM_TH_HLK_PM03]
  Origin = -> Origin067
  Placement = pos=(46.9901,75.3112,1.60005) rot=(0,0,-1;1.5708rad)
FEATURE [Part::Feature] Part__Feature300  label="R0603"
  shape: bbox 1.62 x 0.81 x 0.762 mm, 6 faces (baked)
FEATURE [App::Part] pRkl_R8  label="pRkl-R8"
  Group = -> [Part__Feature300]
  Origin = -> Origin068
  Placement = pos=(66.9291,29.7181,1.60005) rot=(0,0,-1;1.5708rad)
FEATURE [Part::Feature] Part__Feature301  label="R1213"
  shape: bbox 1.62 x 0.81 x 0.762 mm, 6 faces (baked)
FEATURE [App::Part] pRkl_R9  label="pRkl-R9"
  Group = -> [Part__Feature301]
  Origin = -> Origin069
  Placement = pos=(72.7711,31.1151,1.60005) rot=(0,0,-1;1.5708rad)
FEATURE [Part::Feature] Part__Feature302  label="COMPOUND018"
  shape: bbox 6 x 5.5 x 10.3 mm, 117 faces (baked)
FEATURE [Part::Feature] Part__Feature303  label="COMPOUND019"
  shape: bbox 8.21 x 6.528 x 10.7 mm, 321 faces (baked)
FEATURE [App::Part] COMPOUND001  label="COMPOUND020"
  Group = -> [Part__Feature302,Part__Feature303]
  Origin = -> Origin070
FEATURE [App::Part] KEY_TH_K2_1102AQ_D4CW_01  label="KEY-TH_K2-1102AQ-D4CW-01"
  Group = -> [COMPOUND001]
  Origin = -> Origin071
FEATURE [App::Part] pRkl_BTN  label="pRkl-BTN"
  Group = -> [KEY_TH_K2_1102AQ_D4CW_01]
  Origin = -> Origin072
  Placement = pos=(86.8682,24.13,1.60005) rot=(0,0,1;1.5708rad)
FEATURE [Part::Feature] Part__Feature304  label="SOLID004"
  shape: bbox 10 x 8.659 x 10.05 mm, 286 faces (baked)
FEATURE [App::Part] CAP_SMD_BD8_0_L8_3_W8_3_FD  label="CAP-SMD_BD8.0-L8.3-W8.3-FD"
  Group = -> [Part__Feature304]
  Origin = -> Origin073
FEATURE [App::Part] pRkl_C4  label="pRkl-C4"
  Group = -> [CAP_SMD_BD8_0_L8_3_W8_3_FD]
  Origin = -> Origin074
  Placement = pos=(37.8461,26.7971,1.60005) rot=(0,0,1;1.5708rad)
FEATURE [Part::Feature] Part__Feature305  label="SOLID005"
  shape: bbox 10 x 8.659 x 10.05 mm, 286 faces (baked)
FEATURE [App::Part] CAP_SMD_BD8_0_L8_3_W8_3_FD001  label="CAP-SMD_BD8.0-L8.3-W8.3-FD001"
  Group = -> [Part__Feature305]
  Origin = -> Origin075
FEATURE [App::Part] pRkl_C2  label="pRkl-C2"
  Group = -> [CAP_SMD_BD8_0_L8_3_W8_3_FD001]
  Origin = -> Origin076
  Placement = pos=(76.9622,48.5141,1.60005) rot=(0,0,1;1.5708rad)
FEATURE [Part::Feature] Part__Feature306  label="COMPOUND021"
  shape: bbox 30 x 14.6 x 3 mm, 27 faces (baked)
FEATURE [Part::Feature] Part__Feature307  label="COMPOUND022"
  shape: bbox 30 x 16 x 21.8 mm, 984 faces (baked)
FEATURE [App::Part] COMPOUND002  label="COMPOUND023"
  Group = -> [Part__Feature306,Part__Feature307]
  Origin = -> Origin077
FEATURE [App::Part] CONN_TH_3P_P9_50_HB9500_9_5_3P  label="CONN-TH_3P-P9.50_HB9500-9.5-3P"
  Group = -> [COMPOUND002]
  Origin = -> Origin078
FEATURE [App::Part] pRkl_AC_OUT  label="pRkl-AC_OUT"
  Group = -> [CONN_TH_3P_P9_50_HB9500_9_5_3P]
  Origin = -> Origin079
  Placement = pos=(86.1062,81.7882,1.60005) rot=(0,0,1;1.5708rad)
FEATURE [Part::Feature] Part__Feature308  label="COMPOUND024"
  shape: bbox 30 x 14.6 x 3 mm, 27 faces (baked)
FEATURE [Part::Feature] Part__Feature309  label="COMPOUND025"
  shape: bbox 30 x 16 x 21.8 mm, 984 faces (baked)
FEATURE [App::Part] COMPOUND003  label="COMPOUND026"
  Group = -> [Part__Feature308,Part__Feature309]
  Origin = -> Origin080
FEATURE [App::Part] CONN_TH_3P_P9_50_HB9500_9_5_3P001  label="CONN-TH_3P-P9.50_HB9500-9.5-3P001"
  Group = -> [COMPOUND003]
  Origin = -> Origin081
FEATURE [App::Part] pRkl_AC_IN  label="pRkl-AC_IN"
  Group = -> [CONN_TH_3P_P9_50_HB9500_9_5_3P001]
  Origin = -> Origin082
  Placement = pos=(14.732,81.2802,1.60005) rot=(0,0,-1;1.5708rad)
FEATURE [Part::Feature] Part__Feature310  label="SOLID006"
  shape: bbox 3.302 x 1.732 x 1.732 mm, 256 faces (baked)
FEATURE [App::Part] SOD_80_L3_5_W1_5_RD  label="SOD-80_L3.5-W1.5-RD"
  Group = -> [Part__Feature310]
  Origin = -> Origin083
FEATURE [App::Part] pRkl_D1  label="pRkl-D1"
  Group = -> [SOD_80_L3_5_W1_5_RD]
  Origin = -> Origin084
  Placement = pos=(71.6281,39.2431,1.60005) rot=(0,0,1;1.5708rad)
FEATURE [Part::Feature] Part__Feature311  label="COMPOUND027"
  shape: bbox 14.8 x 9.5 x 5.11 mm, 23 faces (baked)
FEATURE [Part::Feature] Part__Feature312  label="COMPOUND028"
  shape: bbox 21.4 x 15.16 x 14 mm, 101 faces (baked)
FEATURE [Part::Feature] Part__Feature313  label="COMPOUND029"
  shape: bbox 0.8 x 4.8 x 4 mm, 12 faces (baked)
FEATURE [Part::Feature] Part__Feature314  label="COMPOUND030"
  shape: bbox 0.8 x 4.8 x 4 mm, 12 faces (baked)
FEATURE [Part::Feature] Part__Feature315  label="COMPOUND031"
  shape: bbox 0.8 x 4.8 x 4 mm, 12 faces (baked)
FEATURE [Part::Feature] Part__Feature316  label="COMPOUND032"
  shape: bbox 0.3222 x 0.001 x 0.6124 mm, 8 faces (baked)
FEATURE [Part::Feature] Part__Feature317  label="COMPOUND033"
  shape: bbox 0.4596 x 0.001 x 0.6317 mm, 16 faces (baked)
FEATURE [Part::Feature] Part__Feature318  label="COMPOUND034"
  shape: bbox 0.3286 x 0.001 x 0.6124 mm, 14 faces (baked)
FEATURE [Part::Feature] Part__Feature319  label="COMPOUND035"
  shape: bbox 0.4996 x 0.001 x 0.612 mm, 16 faces (baked)
FEATURE [Part::Feature] Part__Feature320  label="COMPOUND036"
  shape: bbox 0.549 x 0.001 x 0.6124 mm, 16 faces (baked)
FEATURE [Part::Feature] Part__Feature321  label="COMPOUND037"
  shape: bbox 0.3286 x 0.001 x 0.6124 mm, 14 faces (baked)
FEATURE [Part::Feature] Part__Feature322  label="COMPOUND038"
  shape: bbox 0.3524 x 0.001 x 0.4565 mm, 24 faces (baked)
FEATURE [Part::Feature] Part__Feature323  label="COMPOUND039"
  shape: bbox 0.2952 x 0.001 x 0.4564 mm, 23 faces (baked)
FEATURE [Part::Feature] Part__Feature324  label="COMPOUND040"
  shape: bbox 0.4183 x 0.001 x 0.6419 mm, 17 faces (baked)
FEATURE [Part::Feature] Part__Feature325  label="COMPOUND041"
  shape: bbox 0.3286 x 0.001 x 0.6124 mm, 14 faces (baked)
FEATURE [Part::Feature] Part__Feature326  label="COMPOUND042"
  shape: bbox 0.4996 x 0.001 x 0.612 mm, 16 faces (baked)
FEATURE [Part::Feature] Part__Feature327  label="COMPOUND043"
  shape: bbox 0.549 x 0.001 x 0.6124 mm, 16 faces (baked)
FEATURE [Part::Feature] Part__Feature328  label="COMPOUND044"
  shape: bbox 2.768 x 0.001 x 2.029 mm, 37 faces (baked)
FEATURE [App::Part] COMPOUND004  label="COMPOUND045"
  Group = -> [Part__Feature311,Part__Feature312,Part__Feature313,Part__Feature314,Part__Feature315,Part__Feature316,Part__Feature317,Part__Feature318,Part__Feature319,Part__Feature320,Part__Feature321,Part__Feature322,Part__Feature323,Part__Feature324,Part__Feature325,Part__Feature326,Part__Feature327,Part__Feature328]
  Origin = -> Origin085
FEATURE [App::Part] SW_TH_SS11_BBIWQ_R30_R  label="SW-TH_SS11-BBIWQ-R30-R"
  Group = -> [COMPOUND004]
  Origin = -> Origin086
FEATURE [App::Part] pRkl_SW2  label="pRkl-SW2"
  Group = -> [SW_TH_SS11_BBIWQ_R30_R]
  Origin = -> Origin087
  Placement = pos=(17.145,33.5281,1.60005) rot=(0,0,-1;1.5708rad)
FEATURE [Part::Feature] Part__Feature329  label="COMPOUND046"
  shape: bbox 0.9 x 1.4 x 0.1 mm, 6 faces (baked)
FEATURE [Part::Feature] Part__Feature330  label="COMPOUND047"
  shape: bbox 0.9 x 1.4 x 0.1 mm, 6 faces (baked)
FEATURE [Part::Feature] Part__Feature331  label="COMPOUND048"
  shape: bbox 3.9 x 2.9 x 1.85 mm, 250 faces (baked)
FEATURE [Part::Feature] Part__Feature332  label="COMPOUND049"
  shape: bbox 0.06445 x 0.1225 x 0.001 mm, 8 faces (baked)
FEATURE [Part::Feature] Part__Feature333  label="COMPOUND050"
  shape: bbox 0.09192 x 0.1263 x 0.001 mm, 16 faces (baked)
FEATURE [Part::Feature] Part__Feature334  label="COMPOUND051"
  shape: bbox 0.06573 x 0.1225 x 0.001 mm, 14 faces (baked)
FEATURE [Part::Feature] Part__Feature335  label="COMPOUND052"
  shape: bbox 0.09992 x 0.1224 x 0.001 mm, 16 faces (baked)
FEATURE [Part::Feature] Part__Feature336  label="COMPOUND053"
  shape: bbox 0.1098 x 0.1225 x 0.001 mm, 16 faces (baked)
FEATURE [Part::Feature] Part__Feature337  label="COMPOUND054"
  shape: bbox 0.06573 x 0.1225 x 0.001 mm, 14 faces (baked)
FEATURE [Part::Feature] Part__Feature338  label="COMPOUND055"
  shape: bbox 0.07047 x 0.09129 x 0.001 mm, 24 faces (baked)
FEATURE [Part::Feature] Part__Feature339  label="COMPOUND056"
  shape: bbox 0.05905 x 0.09127 x 0.001 mm, 23 faces (baked)
FEATURE [Part::Feature] Part__Feature340  label="COMPOUND057"
  shape: bbox 0.08366 x 0.1284 x 0.001 mm, 17 faces (baked)
FEATURE [Part::Feature] Part__Feature341  label="COMPOUND058"
  shape: bbox 0.06573 x 0.1225 x 0.001 mm, 14 faces (baked)
FEATURE [Part::Feature] Part__Feature342  label="COMPOUND059"
  shape: bbox 0.09992 x 0.1224 x 0.001 mm, 16 faces (baked)
FEATURE [Part::Feature] Part__Feature343  label="COMPOUND060"
  shape: bbox 0.1098 x 0.1225 x 0.001 mm, 16 faces (baked)
FEATURE [Part::Feature] Part__Feature344  label="COMPOUND061"
  shape: bbox 0.5536 x 0.4058 x 0.001 mm, 37 faces (baked)
FEATURE [App::Part] COMPOUND005  label="COMPOUND062"
  Group = -> [Part__Feature329,Part__Feature330,Part__Feature331,Part__Feature332,Part__Feature333,Part__Feature334,Part__Feature335,Part__Feature336,Part__Feature337,Part__Feature338,Part__Feature339,Part__Feature340,Part__Feature341,Part__Feature342,Part__Feature343,Part__Feature344]
  Origin = -> Origin088
FEATURE [App::Part] SW_SMD_L3_9_W3_0_P4_45  label="SW-SMD_L3.9-W3.0-P4.45"
  Group = -> [COMPOUND005]
  Origin = -> Origin089
FEATURE [App::Part] pRkl_BOOT  label="pRkl-BOOT"
  Group = -> [SW_SMD_L3_9_W3_0_P4_45]
  Origin = -> Origin090
  Placement = pos=(57.2771,31.8771,1.60005) rot=(0,0,1;0rad)
FEATURE [Part::Feature] Part__Feature345  label="COMPOUND063"
  shape: bbox 2.5 x 1.25 x 0.95 mm, 123 faces (baked)
FEATURE [Part::Feature] Part__Feature346  label="COMPOUND064"
  shape: bbox 0.03003 x 0.00596 x 0.05682 mm, 8 faces (baked)
FEATURE [Part::Feature] Part__Feature347  label="COMPOUND065"
  shape: bbox 0.04264 x 0.006127 x 0.05873 mm, 16 faces (baked)
FEATURE [Part::Feature] Part__Feature348  label="COMPOUND066"
  shape: bbox 0.03063 x 0.00596 x 0.05682 mm, 14 faces (baked)
FEATURE [Part::Feature] Part__Feature349  label="COMPOUND067"
  shape: bbox 0.04636 x 0.00596 x 0.05682 mm, 16 faces (baked)
FEATURE [Part::Feature] Part__Feature350  label="COMPOUND068"
  shape: bbox 0.05124 x 0.00596 x 0.05682 mm, 16 faces (baked)
FEATURE [Part::Feature] Part__Feature351  label="COMPOUND069"
  shape: bbox 0.03063 x 0.00596 x 0.05682 mm, 14 faces (baked)
FEATURE [Part::Feature] Part__Feature352  label="COMPOUND070"
  shape: bbox 0.03268 x 0.004706 x 0.04249 mm, 24 faces (baked)
FEATURE [Part::Feature] Part__Feature353  label="COMPOUND071"
  shape: bbox 0.02747 x 0.004706 x 0.04249 mm, 23 faces (baked)
FEATURE [Part::Feature] Part__Feature354  label="COMPOUND072"
  shape: bbox 0.03904 x 0.006211 x 0.05969 mm, 17 faces (baked)
FEATURE [Part::Feature] Part__Feature355  label="COMPOUND073"
  shape: bbox 0.03063 x 0.00596 x 0.05682 mm, 14 faces (baked)
FEATURE [Part::Feature] Part__Feature356  label="COMPOUND074"
  shape: bbox 0.04636 x 0.00596 x 0.05682 mm, 16 faces (baked)
FEATURE [Part::Feature] Part__Feature357  label="COMPOUND075"
  shape: bbox 0.05124 x 0.00596 x 0.05682 mm, 16 faces (baked)
FEATURE [Part::Feature] Part__Feature358  label="COMPOUND076"
  shape: bbox 0.2583 x 0.01751 x 0.1888 mm, 37 faces (baked)
FEATURE [App::Part] COMPOUND006  label="COMPOUND077"
  Group = -> [Part__Feature345,Part__Feature346,Part__Feature347,Part__Feature348,Part__Feature349,Part__Feature350,Part__Feature351,Part__Feature352,Part__Feature353,Part__Feature354,Part__Feature355,Part__Feature356,Part__Feature357,Part__Feature358]
  Origin = -> Origin091
FEATURE [App::Part] SOD_323_L1_7_W1_3_LS2_5_RD  label="SOD-323_L1.7-W1.3-LS2.5-RD"
  Group = -> [COMPOUND006]
  Origin = -> Origin092
FEATURE [App::Part] pRkl_D2  label="pRkl-D2"
  Group = -> [SOD_323_L1_7_W1_3_LS2_5_RD]
  Origin = -> Origin093
  Placement = pos=(54.9911,26.2891,1.60005) rot=(0,0,1;0rad)
FEATURE [Part::Feature] Part__Feature359  label="SOLID007"
  shape: bbox 2.082 x 1.041 x 1.041 mm, 357 faces (baked)
FEATURE [App::Part] C0603
  Group = -> [Part__Feature359]
  Origin = -> Origin094
FEATURE [App::Part] pRkl_C6  label="pRkl-C6"
  Group = -> [C0603]
  Origin = -> Origin095
  Placement = pos=(80.8992,23.495,1.60005) rot=(0,0,1;0rad)
FEATURE [Part::Feature] Part__Feature360  label="COMPOUND078"
  shape: bbox 2.9 x 2.9 x 1.1 mm, 161 faces (baked)
FEATURE [Part::Feature] Part__Feature361  label="COMPOUND079"
  shape: bbox 0.06101 x 0.03218 x 0.001 mm, 8 faces (baked)
FEATURE [Part::Feature] Part__Feature362  label="COMPOUND080"
  shape: bbox 0.06307 x 0.04568 x 0.001 mm, 16 faces (baked)
FEATURE [Part::Feature] Part__Feature363  label="COMPOUND081"
  shape: bbox 0.06101 x 0.03281 x 0.001 mm, 14 faces (baked)
FEATURE [Part::Feature] Part__Feature364  label="COMPOUND082"
  shape: bbox 0.06101 x 0.04967 x 0.001 mm, 16 faces (baked)
FEATURE [Part::Feature] Part__Feature365  label="COMPOUND083"
  shape: bbox 0.06101 x 0.0549 x 0.001 mm, 16 faces (baked)
FEATURE [Part::Feature] Part__Feature366  label="COMPOUND084"
  shape: bbox 0.06101 x 0.03281 x 0.001 mm, 14 faces (baked)
FEATURE [Part::Feature] Part__Feature367  label="COMPOUND085"
  shape: bbox 0.0456 x 0.03501 x 0.001 mm, 24 faces (baked)
FEATURE [Part::Feature] Part__Feature368  label="COMPOUND086"
  shape: bbox 0.0456 x 0.02943 x 0.001 mm, 23 faces (baked)
FEATURE [Part::Feature] Part__Feature369  label="COMPOUND087"
  shape: bbox 0.0641 x 0.04183 x 0.001 mm, 17 faces (baked)
FEATURE [Part::Feature] Part__Feature370  label="COMPOUND088"
  shape: bbox 0.06101 x 0.03281 x 0.001 mm, 14 faces (baked)
FEATURE [Part::Feature] Part__Feature371  label="COMPOUND089"
  shape: bbox 0.06101 x 0.04967 x 0.001 mm, 16 faces (baked)
FEATURE [Part::Feature] Part__Feature372  label="COMPOUND090"
  shape: bbox 0.06101 x 0.0549 x 0.001 mm, 16 faces (baked)
FEATURE [Part::Feature] Part__Feature373  label="COMPOUND091"
  shape: bbox 0.203 x 0.2768 x 0.001 mm, 37 faces (baked)
FEATURE [App::Part] COMPOUND007  label="COMPOUND092"
  Group = -> [Part__Feature360,Part__Feature361,Part__Feature362,Part__Feature363,Part__Feature364,Part__Feature365,Part__Feature366,Part__Feature367,Part__Feature368,Part__Feature369,Part__Feature370,Part__Feature371,Part__Feature372,Part__Feature373]
  Origin = -> Origin096
FEATURE [App::Part] SOT_23_5_L2_9_W1_6_P0_95_LS2_8_BR  label="SOT-23-5_L2.9-W1.6-P0.95-LS2.8-BR"
  Group = -> [COMPOUND007]
  Origin = -> Origin097
FEATURE [App::Part] pRkl_U1  label="pRkl-U1"
  Group = -> [SOT_23_5_L2_9_W1_6_P0_95_LS2_8_BR]
  Origin = -> Origin098
  Placement = pos=(60.1981,23.622,1.60005) rot=(0,0,1;0rad)
FEATURE [Part::Feature] Part__Feature374  label="SOLID008"
  shape: bbox 10.57 x 2.5 x 11.7 mm, 358 faces (baked)
FEATURE [App::Part] HDR_TH_4P_P2_54_V_F  label="HDR-TH_4P-P2.54-V-F"
  Group = -> [Part__Feature374]
  Origin = -> Origin099
FEATURE [App::Part] pRkl_SCREEN  label="pRkl-SCREEN"
  Group = -> [HDR_TH_4P_P2_54_V_F]
  Origin = -> Origin100
  Placement = pos=(48.2601,22.225,1.60005) rot=(0,0,1;3.14159rad)
FEATURE [Part::Feature] Part__Feature375  label="COMPOUND093"
  shape: bbox 1.2 x 0.8001 x 0.4007 mm, 18 faces (baked)
FEATURE [Part::Feature] Part__Feature376  label="COMPOUND094"
  shape: bbox 0.46 x 0.8 x 0.22 mm, 26 faces (baked)
FEATURE [Part::Feature] Part__Feature377  label="COMPOUND095"
  shape: bbox 0.31 x 0.8 x 0.22 mm, 18 faces (baked)
FEATURE [Part::Feature] Part__Feature378  label="COMPOUND096"
  shape: bbox 1.6 x 0.81 x 0.5 mm, 294 faces (baked)
FEATURE [App::Part] COMPOUND008  label="COMPOUND097"
  Group = -> [Part__Feature375,Part__Feature376,Part__Feature377,Part__Feature378]
  Origin = -> Origin101
FEATURE [App::Part] LED0603_RD_RED  label="LED0603-RD_RED"
  Group = -> [COMPOUND008]
  Origin = -> Origin102
FEATURE [App::Part] pRkl_PWR  label="pRkl-PWR"
  Group = -> [LED0603_RD_RED]
  Origin = -> Origin103
  Placement = pos=(86.6142,37.0841,1.60005) rot=(0,0,1;0rad)
FEATURE [Part::Feature] Part__Feature379  label="COMPOUND098"
  shape: bbox 8.94 x 7.33 x 4.16 mm, 174 faces (baked)
FEATURE [Part::Feature] Part__Feature380  label="COMPOUND099"
  shape: bbox 8.94 x 6.75 x 3.61 mm, 133 faces (baked)
FEATURE [Part::Feature] Part__Feature381  label="COMPOUND100"
  shape: bbox 0.1073 x 0.2034 x 0.001 mm, 8 faces (baked)
FEATURE [Part::Feature] Part__Feature382  label="COMPOUND101"
  shape: bbox 0.1523 x 0.2102 x 0.001 mm, 16 faces (baked)
FEATURE [Part::Feature] Part__Feature383  label="COMPOUND102"
  shape: bbox 0.1094 x 0.2034 x 0.001 mm, 14 faces (baked)
FEATURE [Part::Feature] Part__Feature384  label="COMPOUND103"
  shape: bbox 0.1656 x 0.2034 x 0.001 mm, 16 faces (baked)
FEATURE [Part::Feature] Part__Feature385  label="COMPOUND104"
  shape: bbox 0.183 x 0.2034 x 0.001 mm, 16 faces (baked)
FEATURE [Part::Feature] Part__Feature386  label="COMPOUND105"
  shape: bbox 0.1094 x 0.2034 x 0.001 mm, 14 faces (baked)
FEATURE [Part::Feature] Part__Feature387  label="COMPOUND106"
  shape: bbox 0.1167 x 0.152 x 0.001 mm, 24 faces (baked)
FEATURE [Part::Feature] Part__Feature388  label="COMPOUND107"
  shape: bbox 0.0981 x 0.152 x 0.001 mm, 23 faces (baked)
FEATURE [Part::Feature] Part__Feature389  label="COMPOUND108"
  shape: bbox 0.1394 x 0.2137 x 0.001 mm, 17 faces (baked)
FEATURE [Part::Feature] Part__Feature390  label="COMPOUND109"
  shape: bbox 0.1094 x 0.2034 x 0.001 mm, 14 faces (baked)
FEATURE [Part::Feature] Part__Feature391  label="COMPOUND110"
  shape: bbox 0.1656 x 0.2034 x 0.001 mm, 16 faces (baked)
FEATURE [Part::Feature] Part__Feature392  label="COMPOUND111"
  shape: bbox 0.183 x 0.2034 x 0.001 mm, 16 faces (baked)
FEATURE [Part::Feature] Part__Feature393  label="COMPOUND112"
  shape: bbox 0.9225 x 0.6767 x 0.001 mm, 37 faces (baked)
FEATURE [App::Part] COMPOUND009  label="COMPOUND113"
  Group = -> [Part__Feature379,Part__Feature380,Part__Feature381,Part__Feature382,Part__Feature383,Part__Feature384,Part__Feature385,Part__Feature386,Part__Feature387,Part__Feature388,Part__Feature389,Part__Feature390,Part__Feature391,Part__Feature392,Part__Feature393]
  Origin = -> Origin104
FEATURE [App::Part] USB_C_SMD_TYPE_C_6PIN_2MD_073  label="USB-C-SMD_TYPE-C-6PIN-2MD-073"
  Group = -> [COMPOUND009]
  Origin = -> Origin105
FEATURE [App::Part] pRkl_USB2  label="pRkl-USB2"
  Group = -> [USB_C_SMD_TYPE_C_6PIN_2MD_073]
  Origin = -> Origin106
  Placement = pos=(70.8661,23.241,1.60005) rot=(0,0,1;0rad)
FEATURE [Part::Feature] Part__Feature394  label="COMPOUND114"
  shape: bbox 13.2 x 12.5 x 2.42 mm, 413 faces (baked)
FEATURE [Part::Feature] Part__Feature395  label="COMPOUND115"
  shape: bbox 0.1502 x 0.2847 x 0.001 mm, 8 faces (baked)
FEATURE [Part::Feature] Part__Feature396  label="COMPOUND116"
  shape: bbox 0.2132 x 0.2943 x 0.001 mm, 16 faces (baked)
FEATURE [Part::Feature] Part__Feature397  label="COMPOUND117"
  shape: bbox 0.1531 x 0.2847 x 0.001 mm, 14 faces (baked)
FEATURE [Part::Feature] Part__Feature398  label="COMPOUND118"
  shape: bbox 0.2318 x 0.2847 x 0.001 mm, 16 faces (baked)
FEATURE [Part::Feature] Part__Feature399  label="COMPOUND119"
  shape: bbox 0.2562 x 0.2847 x 0.001 mm, 16 faces (baked)
FEATURE [Part::Feature] Part__Feature400  label="COMPOUND120"
  shape: bbox 0.1531 x 0.2847 x 0.001 mm, 14 faces (baked)
FEATURE [Part::Feature] Part__Feature401  label="COMPOUND121"
  shape: bbox 0.1634 x 0.2128 x 0.001 mm, 24 faces (baked)
FEATURE [Part::Feature] Part__Feature402  label="COMPOUND122"
  shape: bbox 0.1373 x 0.2128 x 0.001 mm, 23 faces (baked)
FEATURE [Part::Feature] Part__Feature403  label="COMPOUND123"
  shape: bbox 0.1952 x 0.2991 x 0.001 mm, 17 faces (baked)
FEATURE [Part::Feature] Part__Feature404  label="COMPOUND124"
  shape: bbox 0.1531 x 0.2847 x 0.001 mm, 14 faces (baked)
FEATURE [Part::Feature] Part__Feature405  label="COMPOUND125"
  shape: bbox 0.2318 x 0.2847 x 0.001 mm, 16 faces (baked)
FEATURE [Part::Feature] Part__Feature406  label="COMPOUND126"
  shape: bbox 0.2562 x 0.2847 x 0.001 mm, 16 faces (baked)
FEATURE [Part::Feature] Part__Feature407  label="COMPOUND127"
  shape: bbox 1.292 x 0.9474 x 0.001 mm, 37 faces (baked)
FEATURE [App::Part] COMPOUND010  label="COMPOUND128"
  Group = -> [Part__Feature394,Part__Feature395,Part__Feature396,Part__Feature397,Part__Feature398,Part__Feature399,Part__Feature400,Part__Feature401,Part__Feature402,Part__Feature403,Part__Feature404,Part__Feature405,Part__Feature406,Part__Feature407]
  Origin = -> Origin107
FEATURE [App::Part] WIFIM_SMD_ESP32_C3_MINI_MINI_1U  label="WIFIM-SMD_ESP32-C3-MINI-MINI-1U"
  Group = -> [COMPOUND010]
  Origin = -> Origin108
FEATURE [App::Part] pRkl_U3  label="pRkl-U3"
  Group = -> [WIFIM_SMD_ESP32_C3_MINI_MINI_1U]
  Origin = -> Origin109
  Placement = pos=(52.7051,42.1641,1.60005) rot=(0,0,1;0rad)
FEATURE [Part::Feature] Part__Feature408  label="L0603"
  shape: bbox 0.762 x 0.762 x 0.762 mm, 6 faces (baked)
FEATURE [App::Part] pRkl_L1  label="pRkl-L1"
  Group = -> [Part__Feature408]
  Origin = -> Origin110
  Placement = pos=(68.7071,29.8451,1.60005) rot=(0,0,-1;1.5708rad)
FEATURE [Part::Feature] Part__Feature409  label="L0604"
  shape: bbox 0.762 x 0.762 x 0.762 mm, 6 faces (baked)
FEATURE [App::Part] pRkl_L2  label="pRkl-L2"
  Group = -> [Part__Feature409]
  Origin = -> Origin111
  Placement = pos=(70.7391,29.5911,1.60005) rot=(0,0,-1;1.5708rad)
FEATURE [Part::Feature] Part__Feature410  label="SOLID009"
  shape: bbox 29.25 x 5.953 x 9.727 mm, 258 faces (baked)
FEATURE [App::Part] FUSE_TH_BD5_5_L21_0_P28_00_D1_00  label="FUSE-TH_BD5.5-L21.0-P28.00-D1.00"
  Group = -> [Part__Feature410]
  Origin = -> Origin112
FEATURE [App::Part] pRkl_FUSE  label="pRkl-FUSE"
  Group = -> [FUSE_TH_BD5_5_L21_0_P28_00_D1_00]
  Origin = -> Origin113
  Placement = pos=(30.9881,61.9761,1.60005) rot=(0,0,-1;1.5708rad)
FEATURE [Part::Feature] Part__Feature411  label="SOLID010"
  shape: bbox 19.2 x 15.81 x 18.85 mm, 333 faces (baked)
FEATURE [App::Part] RELAY_TH_SRD_XXVDC_XL_C  label="RELAY-TH_SRD-XXVDC-XL-C"
  Group = -> [Part__Feature411]
  Origin = -> Origin114
FEATURE [App::Part] pRkl_K1  label="pRkl-K1"
  Group = -> [RELAY_TH_SRD_XXVDC_XL_C]
  Origin = -> Origin115
  Placement = pos=(67.5641,68.3261,1.60005) rot=(0,0,1;0rad)
FEATURE [Part::Feature] Part__Feature412  label="COMPOUND129"
  shape: bbox 1.2 x 0.8 x 0.33 mm, 18 faces (baked)
FEATURE [Part::Feature] Part__Feature413  label="COMPOUND130"
  shape: bbox 0.31 x 0.8 x 0.28 mm, 14 faces (baked)
FEATURE [Part::Feature] Part__Feature414  label="COMPOUND131"
  shape: bbox 0.51 x 0.8 x 0.28 mm, 20 faces (baked)
FEATURE [Part::Feature] Part__Feature415  label="COMPOUND132"
  shape: bbox 1.6 x 0.81 x 0.36 mm, 294 faces (baked)
FEATURE [App::Part] COMPOUND011  label="COMPOUND133"
  Group = -> [Part__Feature412,Part__Feature413,Part__Feature414,Part__Feature415]
  Origin = -> Origin116
FEATURE [App::Part] LED0603_RD_GREEN  label="LED0603-RD_GREEN"
  Group = -> [COMPOUND011]
  Origin = -> Origin117
FEATURE [App::Part] pRkl_SW  label="pRkl-SW"
  Group = -> [LED0603_RD_GREEN]
  Origin = -> Origin118
  Placement = pos=(86.6142,44.4501,1.60005) rot=(0,0,1;0rad)
FEATURE [App::Part] PCBModel
  Group = -> [TopSilk,BottomSilk,Part__Feature274,pRkl_C1,pRkl_C3,pRkl_C5,pRkl_Q1,pRkl_R10,pRkl_R11,pRkl_R2,pRkl_R3,pRkl_AC_DC_CONV,pRkl_R8,pRkl_R9,pRkl_BTN,pRkl_C4,pRkl_C2,pRkl_AC_OUT,pRkl_AC_IN,pRkl_D1,pRkl_SW2,pRkl_BOOT,pRkl_D2,pRkl_C6,pRkl_U1,pRkl_SCREEN,pRkl_PWR,pRkl_USB2,pRkl_U3,pRkl_L1,pRkl_L2,pRkl_FUSE,pRkl_K1,pRkl_SW]
  Origin = -> Origin119
  Placement = pos=(0,0,-40.5) rot=(0,0,1;0rad)
FEATURE [PartDesign::Pocket] Pocket031
  BaseFeature = -> Pad061
  Direction = (1,0,4e-16)
  Length = 4
  Length2 = 5
  Profile = -> Pad061 [Face65,Face62]
  Refine = true
  Type = 0
FEATURE [Sketcher::SketchObject] Sketch045
  ExternalGeometry = -> [Pocket031]
  FullyConstrained = true
  MapMode = 5
  Placement = pos=(0,0,0) rot=(1,0,0;3.14159rad)
  Support = -> [Pocket031]
  sketch-geometry (8):
    g0: LineSegment StartX=39.5 StartY=-65.35 StartZ=0 EndX=62.3 EndY=-65.35 EndZ=0
    g1: LineSegment StartX=62.3 StartY=-65.35 StartZ=0 EndX=62.3 EndY=-78.15 EndZ=0
    g2: LineSegment StartX=62.3 StartY=-78.15 StartZ=0 EndX=39.5 EndY=-78.15 EndZ=0
    g3: LineSegment StartX=39.5 StartY=-78.15 StartZ=0 EndX=39.5 EndY=-65.35 EndZ=0
    g4: LineSegment StartX=38.5 StartY=-64.35 StartZ=0 EndX=63.3 EndY=-64.35 EndZ=0
    g5: LineSegment StartX=63.3 StartY=-64.35 StartZ=0 EndX=63.3 EndY=-79.15 EndZ=0
    g6: LineSegment StartX=63.3 StartY=-79.15 StartZ=0 EndX=38.5 EndY=-79.15 EndZ=0
    g7: LineSegment StartX=38.5 StartY=-79.15 StartZ=0 EndX=38.5 EndY=-64.35 EndZ=0
  constraints (22):
    c: Coincident(g0,g1)
    c: Coincident(g1,g2)
    c: Coincident(g2,g3)
    c: Coincident(g3,g0)
    c: Horizontal(g0)
    c: Horizontal(g2)
    c: Vertical(g1)
    c: Vertical(g3)
    c: Coincident(g0,g-4)
    c: Coincident(g1,g-6)
    c: Coincident(g4,g5)
    c: Coincident(g5,g6)
    c: Coincident(g6,g7)
    c: Coincident(g7,g4)
    c: Horizontal(g4)
    c: Horizontal(g6)
    c: Vertical(g5)
    c: Vertical(g7)
    c: DistanceX(g0,g4) = 1
    c: DistanceX(g6,g2) = 1
    c: DistanceY(g0,g4) = 1
    c: DistanceY(g5,g1) = 1
FEATURE [PartDesign::Pad] Pad062
  BaseFeature = -> Pocket031
  Direction = (0,0,-1)
  Length = 1
  Length2 = 10
  Profile = -> Sketch045
  ReferenceAxis = -> Sketch045 [N_Axis]
  Refine = true
  Type = 0
FEATURE [PartDesign::Pocket] Pocket032
  BaseFeature = -> Pad060
  Direction = (0,0,-1)
  Length = 12
  Length2 = 5
  Profile = -> Pad060 [Face330]
  Refine = true
  Type = 0
FEATURE [PartDesign::Body] Body  label="Base"
  Group = -> [Sketch,Pad,Sketch001,Pad001,Sketch002,Pad002,Sketch003,Pad003,Pad004,Pad005,Pad006,Sketch004,Pad007,Sketch005,Pad008,Sketch006,Pad009,Sketch007,Pocket,Pad010,Pad011,Pad012,Pad013,Sketch022,Pocket007,Sketch024,Pocket009,Pad034,Sketch032,Pad039,Sketch033,Pad040,Sketch034,Pocket016,Fillet,Sketch035,Pad041,Sketch036,Pocket017,Fillet001,ShapeString,Pad042,ShapeString001,Pad043,Pad059,Pocket029,Pad060,+1 more]
  Origin = -> Origin049
  Placement = pos=(0,0,-50.89) rot=(0,0,1;0rad)
  Tip = -> Pocket032
FEATURE [PartDesign::Pad] Pad063
  BaseFeature = -> Pad062
  Direction = (0,0,-1)
  Length = 11.8
  Length2 = 10
  Profile = -> Pad062 [Face37]
  Refine = true
  Type = 0
FEATURE [PartDesign::Pad] Pad064
  BaseFeature = -> Pad063
  Direction = (0,-1,0)
  Length = 1
  Length2 = 10
  Profile = -> Pad063 [Face80]
  Refine = true
  Type = 0
FEATURE [Sketcher::SketchObject] Sketch046
  ExternalGeometry = -> [Pad064]
  FullyConstrained = true
  MapMode = 5
  Placement = pos=(93.9,9e-16,-5.6e-15) rot=(0.57735,0.57735,0.57735;2.0944rad)
  Support = -> [Pad064]
  sketch-geometry (1):
    g0: Circle CenterX=24.13 CenterY=-34.99 CenterZ=0 NormalX=0 NormalY=0 NormalZ=1 AngleXU=0 Radius=2.2
  constraints (3):
    c: Diameter(g0) = 4.4
    c: DistanceY(g-3,g0) = 5.61
    c: DistanceX(g0,g-3) = 5.97
FEATURE [PartDesign::Pocket] Pocket033
  BaseFeature = -> Pad064
  Direction = (-1,0,0)
  Length = 5
  Length2 = 5
  Profile = -> Sketch046
  ReferenceAxis = -> Sketch046 [N_Axis]
  Refine = true
  Type = 0
FEATURE [PartDesign::Pad] Pad065
  BaseFeature = -> Pocket033
  Direction = (0,0,1)
  Length = 1.7
  Length2 = 10
  Profile = -> Pocket033 [Face1089,Face1090,Face1091,Face1092,Face1093,Face1094,Face1095,Face1096,Face1105,Face1106,Face1107,Face1108,Face1110,Face1111,Face1109,Face1104,Face1103,Face1102,Face1099,Face1101,Face1100,Face1097,Face1098,Face1088,Face1087,Face1086,Face1085]
  Refine = true
  Type = 0
FEATURE [PartDesign::Pocket] Pocket034
  BaseFeature = -> Pad065
  Direction = (0,0,1)
  Length = 1
  Length2 = 5
  Profile = -> Pad065 [Face1129]
  Refine = true
  Type = 0
FEATURE [PartDesign::Pocket] Pocket035
  BaseFeature = -> Pocket034
  Direction = (0,0,1)
  Length = 1
  Length2 = 5
  Profile = -> Pocket034 [Face1110]
  Refine = true
  Type = 0
FEATURE [Sketcher::SketchObject] Sketch047
  ExternalGeometry = -> [Pocket035]
  FullyConstrained = true
  MapMode = 5
  Placement = pos=(0,0,-3) rot=(1,0,0;3.14159rad)
  Support = -> [Pocket035]
  sketch-geometry (4):
    g0: LineSegment StartX=35 StartY=-55.85 StartZ=0 EndX=66.8 EndY=-55.85 EndZ=0
    g1: LineSegment StartX=66.8 StartY=-55.85 StartZ=0 EndX=66.8 EndY=-84.65 EndZ=0
    g2: LineSegment StartX=66.8 StartY=-84.65 StartZ=0 EndX=35 EndY=-84.65 EndZ=0
    g3: LineSegment StartX=35 StartY=-84.65 StartZ=0 EndX=35 EndY=-55.85 EndZ=0
  constraints (12):
    c: Coincident(g0,g1)
    c: Coincident(g1,g2)
    c: Coincident(g2,g3)
    c: Coincident(g3,g0)
    c: Horizontal(g0)
    c: Horizontal(g2)
    c: Vertical(g1)
    c: Vertical(g3)
    c: PointOnObject(g0,g-4)
    c: PointOnObject(g1,g-5)
    c: PointOnObject(g-6,g0)
    c: PointOnObject(g-3,g2)
FEATURE [PartDesign::Pocket] Pocket036
  BaseFeature = -> Pocket035
  Direction = (0,0,1)
  Length = 2.99
  Length2 = 5
  Profile = -> Sketch047
  ReferenceAxis = -> Sketch047 [N_Axis]
  Refine = true
  Type = 0
FEATURE [PartDesign::Pad] Pad066
  BaseFeature = -> Pocket036
  Direction = (0,0,-1)
  Length = 1
  Length2 = 10
  Profile = -> Pocket036 [Face3]
  Refine = true
  Type = 0
FEATURE [Sketcher::SketchObject] Sketch048
  FullyConstrained = false
  MapMode = 5
  Placement = pos=(0,0,-3) rot=(1,0,0;3.14159rad)
  Support = -> [Pad066]
  sketch-geometry (4):
    g0: LineSegment StartX=33.8449 StartY=-52.6367 StartZ=0 EndX=67.8776 EndY=-52.6367 EndZ=0
    g1: LineSegment StartX=67.8776 StartY=-52.6367 StartZ=0 EndX=67.8776 EndY=-88.3475 EndZ=0
    g2: LineSegment StartX=67.8776 StartY=-88.3475 StartZ=0 EndX=33.8449 EndY=-88.3475 EndZ=0
    g3: LineSegment StartX=33.8449 StartY=-88.3475 StartZ=0 EndX=33.8449 EndY=-52.6367 EndZ=0
  constraints (8):
    c: Coincident(g0,g1)
    c: Coincident(g1,g2)
    c: Coincident(g2,g3)
    c: Coincident(g3,g0)
    c: Horizontal(g0)
    c: Horizontal(g2)
    c: Vertical(g1)
    c: Vertical(g3)
FEATURE [PartDesign::Pocket] Pocket037
  BaseFeature = -> Pad066
  Direction = (0,0,1)
  Length = 3
  Length2 = 5
  Profile = -> Sketch048
  ReferenceAxis = -> Sketch048 [N_Axis]
  Refine = true
  Type = 0
FEATURE [PartDesign::Chamfer] Chamfer
  Angle = 45
  Base = -> Pocket037 [Edge874,Edge872,Edge873,Edge875]
  BaseFeature = -> Pocket037
  ChamferType = 0
  FlipDirection = false
  Refine = true
  Size = 1.7
  Size2 = 1
  SupportTransform = false
  UseAllEdges = false
FEATURE [PartDesign::Pad] Pad067
  BaseFeature = -> Chamfer
  Direction = (1,0,0)
  Length = 0.5
  Length2 = 10
  Profile = -> Chamfer [Face18]
  Refine = true
  Type = 0
FEATURE [PartDesign::Body] Body001  label="LidTop"
  Group = -> [Sketch008,Pad014,Sketch012,Pad017,Pad018,Pad019,Sketch013,Pad022,Sketch014,Pad023,Pocket002,Pad024,Pad025,Sketch015,Pad026,Sketch016,Pad027,Sketch017,Pad028,Pocket003,Sketch018,Pad029,Sketch019,Pad030,Sketch020,Pad031,Pad032,Pocket004,Pocket005,Pad033,Sketch021,Pocket006,Sketch023,Pocket008,Pocket010,Pocket011,Sketch025,Pocket012,Sketch026,Pad035,Sketch027,Pocket013,Sketch028,Pocket014,Sketch029,+64 more]
  Origin = -> Origin050
  Tip = -> Pad067
